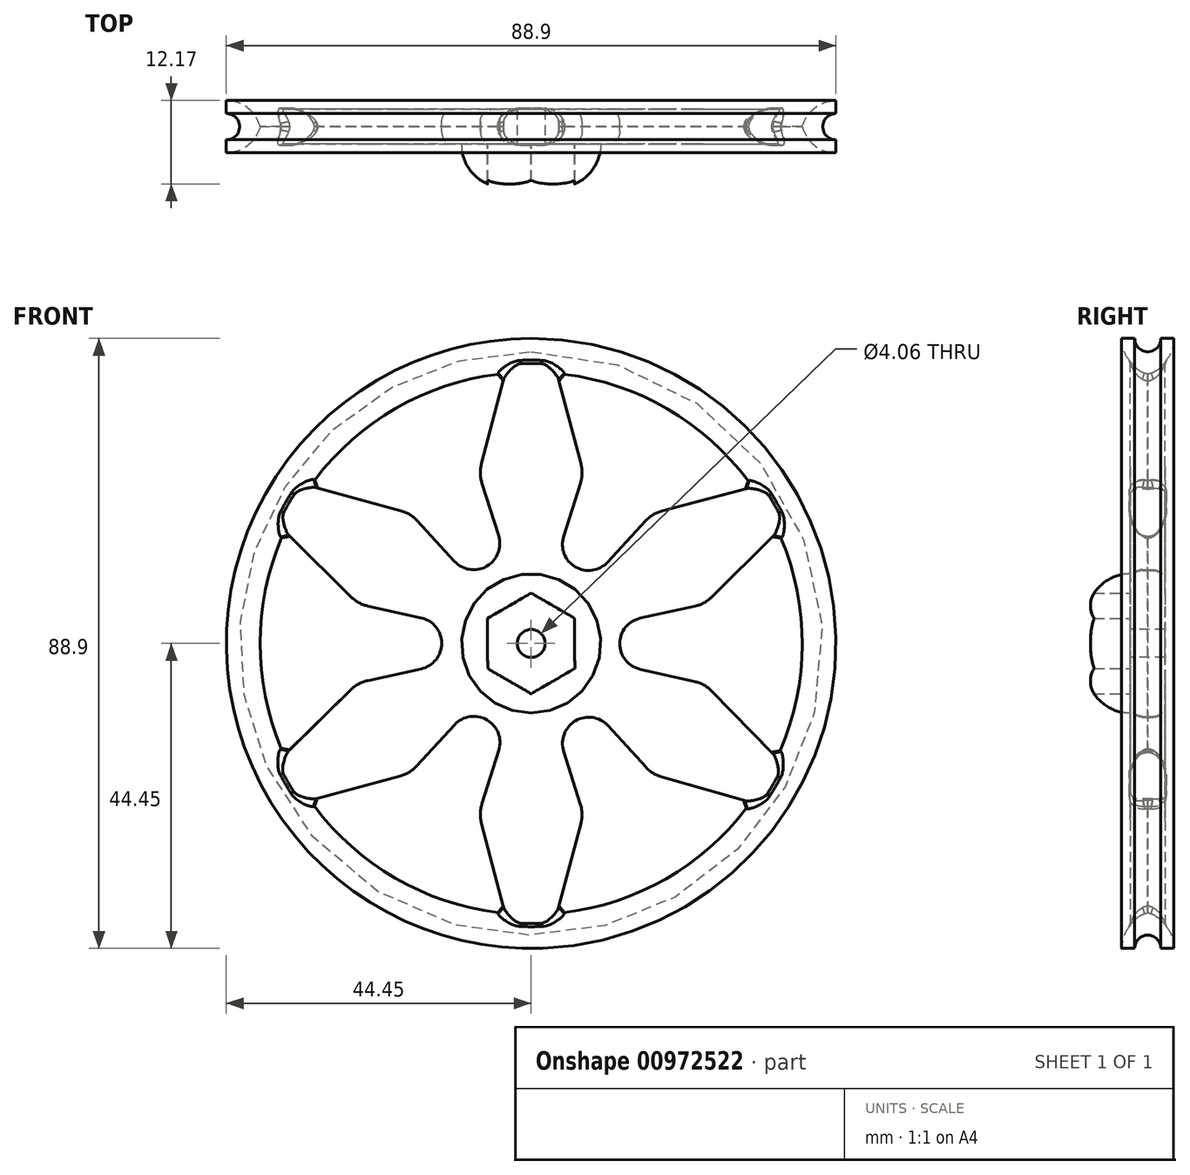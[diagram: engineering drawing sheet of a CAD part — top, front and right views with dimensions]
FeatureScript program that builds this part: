
annotation { "Feature Type Name" : "Feature", "Feature Type Description" : "" }
export const myFeature = defineFeature(function(context is Context, id is Id, definition is map)
    precondition{}
    {
        {
            var Q0;
            Q0=qCreatedBy(makeId("Top.planeOp"),FACE);
            var sketch = newSketch(context, id + "F0", { "sketchPlane" : qUnion([Q0])});
            skLineSegment(sketch, "E0", {"start": v(0, 0) * mm, "end": v(0, 3.8) * mm});
            skLineSegment(sketch, "E1", {"start": v(0, 3.8) * mm, "end": v(0, 0) * mm});
            skLineSegment(sketch, "E2", {"start": v(0, 0) * mm, "end": v(0, -3.8) * mm});
            skLineSegment(sketch, "E3", {"start": v(39.37, 3.8) * mm, "end": v(44.45, 3.8) * mm});
            skLineSegment(sketch, "E4", {"start": v(44.45, -3.8) * mm, "end": v(39.37, -3.8) * mm});
            skLineSegment(sketch, "E5", {"start": v(39.37, 3.8) * mm, "end": v(39.37, 0) * mm});
            skLineSegment(sketch, "E6", {"start": v(39.37, -3.8) * mm, "end": v(39.37, 0) * mm});
            skLineSegment(sketch, "E7", {"start": v(44.45, -1.9) * mm, "end": v(44.45, -3.8) * mm});
            skLineSegment(sketch, "E8", {"start": v(44.45, 3.8) * mm, "end": v(44.45, 1.9) * mm});
            skArc(sketch, "E9", {"start": v(44.45, 1.9) * mm, "mid": v(42.51, 0) * mm, "end": v(44.45, -1.9) * mm});
            skSolve(sketch);
        }
        {
            var Q0;
            Q0=makeQuery(id+"F0.imprint","IMPRINT",FACE,{"disambiguationData":[TD([[makeQuery(id+"F0.imprint","IMPRINT",EDGE,{"derivedFrom":sQuery(id+"F0.wireOp",EDGE,"E3")}),-1.0]])]});
            var Q1;
            Q1=sQuery(id+"F0.wireOp",EDGE,"E1");
            revolve(context, id + "F1", {"surfaceOperationType" : NewSurfaceOperationType.NEW, "entities" : qUnion([Q0]), "axis" : qUnion([Q1]), "revolveType" : RevolveType.FULL});
        }
        {
            var Q0;
            Q0=qCreatedBy(makeId("Front.planeOp"),FACE);
            var sketch = newSketch(context, id + "F2", { "sketchPlane" : qUnion([Q0])});
            skLineSegment(sketch, "E10.0", {"start": v(0, 7.33) * mm, "end": v(6.35, 3.67) * mm});
            skLineSegment(sketch, "E10.1", {"start": v(6.35, 3.67) * mm, "end": v(6.35, -3.67) * mm});
            skLineSegment(sketch, "E10.2", {"start": v(6.35, -3.67) * mm, "end": v(0, -7.33) * mm});
            skLineSegment(sketch, "E10.3", {"start": v(0, -7.33) * mm, "end": v(-6.35, -3.67) * mm});
            skLineSegment(sketch, "E10.4", {"start": v(-6.35, -3.67) * mm, "end": v(-6.35, 3.67) * mm});
            skLineSegment(sketch, "E10.5", {"start": v(-6.35, 3.67) * mm, "end": v(0, 7.33) * mm});
            skCircle(sketch, "E11", {"center": v(0, 0) * mm, "radius": 10.16 * mm});
            skCircle(sketch, "E12", {"center": v(0, 0) * mm, "radius": 39.4 * mm});
            skLineSegment(sketch, "E13", {"start": v(25.3, 5.74) * mm, "end": v(15.9, 3.68) * mm});
            skLineSegment(sketch, "E14", {"start": v(-7.62, 24.77) * mm, "end": v(-3.81, 39.22) * mm});
            skLineSegment(sketch, "E15", {"start": v(7.62, 24.77) * mm, "end": v(3.8, 39.22) * mm});
            skLineSegment(sketch, "E16", {"start": v(17.7, 18.96) * mm, "end": v(32.16, 22.77) * mm});
            skLineSegment(sketch, "E17", {"start": v(-17.57, 18.94) * mm, "end": v(-32.06, 22.91) * mm});
            skLineSegment(sketch, "E18", {"start": v(-25.19, 5.74) * mm, "end": v(-35.87, 16.31) * mm});
            skLineSegment(sketch, "E19", {"start": v(-25.29, -5.73) * mm, "end": v(-35.92, -16.2) * mm});
            skLineSegment(sketch, "E20", {"start": v(-32.13, -22.82) * mm, "end": v(-17.72, -18.96) * mm});
            skLineSegment(sketch, "E21", {"start": v(25.3, 5.74) * mm, "end": v(35.9, 16.26) * mm});
            skLineSegment(sketch, "E22", {"start": v(-17.57, 18.94) * mm, "end": v(-11.2, 11.98) * mm});
            skLineSegment(sketch, "E23", {"start": v(-7.62, 24.77) * mm, "end": v(-4.75, 15.7) * mm});
            skArc(sketch, "E24.filletArc", {"start": v(-11.2, 11.98) * mm, "mid": v(-6.48, 11.25) * mm, "end": v(-4.75, 15.7) * mm});
            skLineSegment(sketch, "E25", {"start": v(7.62, 24.77) * mm, "end": v(4.73, 15.59) * mm});
            skLineSegment(sketch, "E26", {"start": v(11.17, 11.86) * mm, "end": v(17.7, 18.96) * mm});
            skArc(sketch, "E27.filletArc", {"start": v(4.73, 15.59) * mm, "mid": v(6.46, 11.15) * mm, "end": v(11.17, 11.86) * mm});
            skLineSegment(sketch, "E28", {"start": v(17.68, -19.09) * mm, "end": v(31.9, -23.13) * mm});
            skLineSegment(sketch, "E29", {"start": v(25.3, -5.89) * mm, "end": v(35.76, -16.56) * mm});
            skLineSegment(sketch, "E30", {"start": v(25.3, -5.89) * mm, "end": v(15.88, -3.76) * mm});
            skLineSegment(sketch, "E31", {"start": v(11.2, -11.99) * mm, "end": v(17.68, -19.09) * mm});
            skLineSegment(sketch, "E32", {"start": v(7.62, -24.8) * mm, "end": v(4.75, -15.7) * mm});
            skLineSegment(sketch, "E33", {"start": v(-4.72, -15.57) * mm, "end": v(-7.62, -24.8) * mm});
            skLineSegment(sketch, "E34", {"start": v(-7.62, -24.8) * mm, "end": v(-3.81, -39.22) * mm});
            skLineSegment(sketch, "E35", {"start": v(7.62, -24.8) * mm, "end": v(3.81, -39.22) * mm});
            skLineSegment(sketch, "E36", {"start": v(-25.19, 5.74) * mm, "end": v(-16.04, 3.74) * mm});
            skLineSegment(sketch, "E37", {"start": v(-17.72, -18.96) * mm, "end": v(-11.16, -11.85) * mm});
            skLineSegment(sketch, "E38", {"start": v(-16.04, -3.7) * mm, "end": v(-25.29, -5.73) * mm});
            skArc(sketch, "E39.filletArc", {"start": v(-16.04, -3.7) * mm, "mid": v(-13.05, 0.02) * mm, "end": v(-16.04, 3.74) * mm});
            skArc(sketch, "E40.filletArc", {"start": v(-4.72, -15.57) * mm, "mid": v(-6.45, -11.14) * mm, "end": v(-11.16, -11.85) * mm});
            skArc(sketch, "E41.filletArc", {"start": v(11.2, -11.99) * mm, "mid": v(6.48, -11.26) * mm, "end": v(4.75, -15.7) * mm});
            skArc(sketch, "E42.filletArc", {"start": v(15.9, 3.68) * mm, "mid": v(12.91, -0.03) * mm, "end": v(15.88, -3.76) * mm});
            skSolve(sketch);
        }
        {
            var Q0;
            Q0=makeQuery(id+"F2.imprint","IMPRINT",FACE,{"disambiguationData":[TD([[makeQuery(id+"F2.imprint","IMPRINT",EDGE,{"derivedFrom":sQuery(id+"F2.wireOp",EDGE,"E11")}),-1.0]])]});
            var Q1;
            Q1=makeQuery(id+"F2.imprint","IMPRINT",FACE,{"disambiguationData":[TD([[makeQuery(id+"F2.imprint","IMPRINT",EDGE,{"derivedFrom":sQuery(id+"F2.wireOp",EDGE,"E10.0")}),-1.0]])]});
            extrude(context, id + "F3", {"entities" : qUnion([Q0, Q1]), "endBound" : BoundingType.SYMMETRIC, "depth" : 5.08 * mm, "offsetDistance" : 25.4 * mm});
        }
        {
            var Q0;
            Q0=qCreatedBy(makeId("Front.planeOp"),FACE);
            var sketch = newSketch(context, id + "F4", { "sketchPlane" : qUnion([Q0])});
            skCircle(sketch, "E43", {"center": v(0, 0) * mm, "radius": 10.16 * mm});
            skLineSegment(sketch, "E44.0", {"start": v(6.35, -3.66) * mm, "end": v(0, -7.33) * mm});
            skLineSegment(sketch, "E44.1", {"start": v(0, -7.33) * mm, "end": v(-6.35, -3.67) * mm});
            skLineSegment(sketch, "E44.2", {"start": v(-6.35, -3.67) * mm, "end": v(-6.35, 3.66) * mm});
            skLineSegment(sketch, "E44.3", {"start": v(-6.35, 3.66) * mm, "end": v(0, 7.33) * mm});
            skLineSegment(sketch, "E44.4", {"start": v(0, 7.33) * mm, "end": v(6.35, 3.67) * mm});
            skLineSegment(sketch, "E44.5", {"start": v(6.35, 3.67) * mm, "end": v(6.35, -3.66) * mm});
            skSolve(sketch);
        }
        {
            var Q0;
            Q0=makeQuery(id+"F4.imprint","IMPRINT",FACE,{"disambiguationData":[TD([[makeQuery(id+"F4.imprint","IMPRINT",EDGE,{"derivedFrom":sQuery(id+"F4.wireOp",EDGE,"E43")}),1.0]])]});
            extrude(context, id + "F5", {"entities" : qUnion([Q0]), "depth" : 8.9 * mm, "offsetDistance" : 25.4 * mm});
        }
        {
            var Q0;
            Q0=makeQuery(id+"F5.opExtrude","CAP_FACE",FACE,{"disambiguationData":[OSD([sQuery(id+"F4.wireOp",EDGE,"E43"),sQuery(id+"F4.wireOp",EDGE,"E44.0"),sQuery(id+"F4.wireOp",EDGE,"E44.1"),sQuery(id+"F4.wireOp",EDGE,"E44.2"),sQuery(id+"F4.wireOp",EDGE,"E44.3"),sQuery(id+"F4.wireOp",EDGE,"E44.4"),sQuery(id+"F4.wireOp",EDGE,"E44.5")])],"isStart":true});
            extrude(context, id + "F6", {"entities" : qUnion([Q0]), "depth" : 2.54 * mm, "offsetDistance" : 25.4 * mm});
        }
        {
            var Q0;
            Q0=makeQuery(id+"F1.opRevolve","SWEPT_BODY",BODY,{"disambiguationData":[OSD([sQuery(id+"F0.wireOp",EDGE,"E3"),sQuery(id+"F0.wireOp",EDGE,"E4"),sQuery(id+"F0.wireOp",EDGE,"E5"),sQuery(id+"F0.wireOp",EDGE,"E6"),sQuery(id+"F0.wireOp",EDGE,"E7"),sQuery(id+"F0.wireOp",EDGE,"E8"),sQuery(id+"F0.wireOp",EDGE,"E9")])]});
            var Q1;
            Q1=makeQuery(id+"F3.opExtrude","SWEPT_BODY",BODY,{"disambiguationData":[OSD([sQuery(id+"F2.wireOp",EDGE,"E11"),sQuery(id+"F2.wireOp",EDGE,"E12"),sQuery(id+"F2.wireOp",EDGE,"E13"),sQuery(id+"F2.wireOp",EDGE,"E14"),sQuery(id+"F2.wireOp",EDGE,"E15"),sQuery(id+"F2.wireOp",EDGE,"E16"),sQuery(id+"F2.wireOp",EDGE,"E17"),sQuery(id+"F2.wireOp",EDGE,"E18"),sQuery(id+"F2.wireOp",EDGE,"E19"),sQuery(id+"F2.wireOp",EDGE,"E20"),sQuery(id+"F2.wireOp",EDGE,"E21"),sQuery(id+"F2.wireOp",EDGE,"E22"),sQuery(id+"F2.wireOp",EDGE,"E23"),sQuery(id+"F2.wireOp",EDGE,"E24.filletArc"),sQuery(id+"F2.wireOp",EDGE,"E25"),sQuery(id+"F2.wireOp",EDGE,"E26"),sQuery(id+"F2.wireOp",EDGE,"E27.filletArc"),sQuery(id+"F2.wireOp",EDGE,"E28"),sQuery(id+"F2.wireOp",EDGE,"E29"),sQuery(id+"F2.wireOp",EDGE,"E30"),sQuery(id+"F2.wireOp",EDGE,"E31"),sQuery(id+"F2.wireOp",EDGE,"E32"),sQuery(id+"F2.wireOp",EDGE,"E33"),sQuery(id+"F2.wireOp",EDGE,"E34"),sQuery(id+"F2.wireOp",EDGE,"E35"),sQuery(id+"F2.wireOp",EDGE,"E36"),sQuery(id+"F2.wireOp",EDGE,"E37"),sQuery(id+"F2.wireOp",EDGE,"E38"),sQuery(id+"F2.wireOp",EDGE,"E39.filletArc"),sQuery(id+"F2.wireOp",EDGE,"E40.filletArc"),sQuery(id+"F2.wireOp",EDGE,"E41.filletArc"),sQuery(id+"F2.wireOp",EDGE,"E42.filletArc")])]});
            var Q2;
            Q2=makeQuery(id+"F3.opExtrude","SWEPT_BODY",BODY,{"disambiguationData":[OSD([sQuery(id+"F2.wireOp",EDGE,"E10.0"),sQuery(id+"F2.wireOp",EDGE,"E10.1"),sQuery(id+"F2.wireOp",EDGE,"E10.2"),sQuery(id+"F2.wireOp",EDGE,"E10.3"),sQuery(id+"F2.wireOp",EDGE,"E10.4"),sQuery(id+"F2.wireOp",EDGE,"E10.5")])]});
            var Q3;
            Q3=makeQuery(id+"F5.opExtrude","SWEPT_BODY",BODY,{"disambiguationData":[OSD([sQuery(id+"F4.wireOp",EDGE,"E43"),sQuery(id+"F4.wireOp",EDGE,"E44.0"),sQuery(id+"F4.wireOp",EDGE,"E44.1"),sQuery(id+"F4.wireOp",EDGE,"E44.2"),sQuery(id+"F4.wireOp",EDGE,"E44.3"),sQuery(id+"F4.wireOp",EDGE,"E44.4"),sQuery(id+"F4.wireOp",EDGE,"E44.5")])]});
            var Q4;
            Q4=makeQuery(id+"F6.opExtrude","SWEPT_BODY",BODY,{"disambiguationData":[OSD([sQuery(id+"F4.wireOp",EDGE,"E43"),sQuery(id+"F4.wireOp",EDGE,"E44.0"),sQuery(id+"F4.wireOp",EDGE,"E44.1"),sQuery(id+"F4.wireOp",EDGE,"E44.2"),sQuery(id+"F4.wireOp",EDGE,"E44.3"),sQuery(id+"F4.wireOp",EDGE,"E44.4"),sQuery(id+"F4.wireOp",EDGE,"E44.5")])]});
            booleanBodies(context, id + "F7", {"operationType" : BooleanOperationType.UNION, "tools" : qUnion([Q0, Q1, Q2, Q3, Q4])});
        }
        {
            var Q0;
            Q0=makeQuery(id+"F5.opExtrude","CAP_EDGE",EDGE,{"disambiguationData":[OSD([sQuery(id+"F4.wireOp",EDGE,"E43")])],"isStart":false});
            fillet(context, id + "F8", {"entities" : qUnion([Q0]), "radius" : 6.35 * mm, "tangentPropagation" : true, "allowEdgeOverflow" : false});
        }
        {
            var Q0;
            Q0=makeQuery(id+"F3.opExtrude","CAP_FACE",FACE,{"disambiguationData":[OSD([sQuery(id+"F2.wireOp",EDGE,"E11"),sQuery(id+"F2.wireOp",EDGE,"E12"),sQuery(id+"F2.wireOp",EDGE,"E13"),sQuery(id+"F2.wireOp",EDGE,"E14"),sQuery(id+"F2.wireOp",EDGE,"E15"),sQuery(id+"F2.wireOp",EDGE,"E16"),sQuery(id+"F2.wireOp",EDGE,"E17"),sQuery(id+"F2.wireOp",EDGE,"E18"),sQuery(id+"F2.wireOp",EDGE,"E19"),sQuery(id+"F2.wireOp",EDGE,"E20"),sQuery(id+"F2.wireOp",EDGE,"E21"),sQuery(id+"F2.wireOp",EDGE,"E22"),sQuery(id+"F2.wireOp",EDGE,"E23"),sQuery(id+"F2.wireOp",EDGE,"E24.filletArc"),sQuery(id+"F2.wireOp",EDGE,"E25"),sQuery(id+"F2.wireOp",EDGE,"E26"),sQuery(id+"F2.wireOp",EDGE,"E27.filletArc"),sQuery(id+"F2.wireOp",EDGE,"E28"),sQuery(id+"F2.wireOp",EDGE,"E29"),sQuery(id+"F2.wireOp",EDGE,"E30"),sQuery(id+"F2.wireOp",EDGE,"E31"),sQuery(id+"F2.wireOp",EDGE,"E32"),sQuery(id+"F2.wireOp",EDGE,"E33"),sQuery(id+"F2.wireOp",EDGE,"E34"),sQuery(id+"F2.wireOp",EDGE,"E35"),sQuery(id+"F2.wireOp",EDGE,"E36"),sQuery(id+"F2.wireOp",EDGE,"E37"),sQuery(id+"F2.wireOp",EDGE,"E38"),sQuery(id+"F2.wireOp",EDGE,"E39.filletArc"),sQuery(id+"F2.wireOp",EDGE,"E40.filletArc"),sQuery(id+"F2.wireOp",EDGE,"E41.filletArc"),sQuery(id+"F2.wireOp",EDGE,"E42.filletArc")])],"isStart":false});
            var sketch = newSketch(context, id + "F9", { "sketchPlane" : qUnion([Q0])});
            skPoint(sketch, "E45", {"position": v(0, 0) * mm});
            skSolve(sketch);
        }
        {
            var Q0;
            Q0=sQuery(id+"F9.wireOp",VERTEX,"E45");
            var Q1;
            Q1=makeQuery(id+"F1.opRevolve","SWEPT_BODY",BODY,{"disambiguationData":[OSD([sQuery(id+"F0.wireOp",EDGE,"E3"),sQuery(id+"F0.wireOp",EDGE,"E4"),sQuery(id+"F0.wireOp",EDGE,"E5"),sQuery(id+"F0.wireOp",EDGE,"E6"),sQuery(id+"F0.wireOp",EDGE,"E7"),sQuery(id+"F0.wireOp",EDGE,"E8"),sQuery(id+"F0.wireOp",EDGE,"E9")])]});
            hole(context, id + "F10", {"style" : HoleStyle.SIMPLE, "endStyle" : HoleEndStyle.THROUGH, "holeDiameter" : 4.06 * mm, "majorDiameter" : 6.35 * mm, "isTappedThrough" : true, "tappedDepth" : 12.7 * mm, "tapClearance" : 3, "locations" : qUnion([Q0]), "scope" : qUnion([Q1])});
        }
        {
            var Q0;
            Q0=makeQuery(id+"F3.opExtrude","SWEPT_EDGE",EDGE,{"disambiguationData":[OSD([sQuery(id+"F2.wireOp",EDGE,"E17"),sQuery(id+"F2.wireOp",EDGE,"E22")])]});
            var Q1;
            Q1=makeQuery(id+"F3.opExtrude","SWEPT_EDGE",EDGE,{"disambiguationData":[OSD([sQuery(id+"F2.wireOp",EDGE,"E18"),sQuery(id+"F2.wireOp",EDGE,"E36")])]});
            var Q2;
            Q2=makeQuery(id+"F3.opExtrude","SWEPT_EDGE",EDGE,{"disambiguationData":[OSD([sQuery(id+"F2.wireOp",EDGE,"E14"),sQuery(id+"F2.wireOp",EDGE,"E23")])]});
            var Q3;
            Q3=makeQuery(id+"F3.opExtrude","SWEPT_EDGE",EDGE,{"disambiguationData":[OSD([sQuery(id+"F2.wireOp",EDGE,"E15"),sQuery(id+"F2.wireOp",EDGE,"E25")])]});
            var Q4;
            Q4=makeQuery(id+"F3.opExtrude","SWEPT_EDGE",EDGE,{"disambiguationData":[OSD([sQuery(id+"F2.wireOp",EDGE,"E13"),sQuery(id+"F2.wireOp",EDGE,"E21")])]});
            var Q5;
            Q5=makeQuery(id+"F3.opExtrude","SWEPT_EDGE",EDGE,{"disambiguationData":[OSD([sQuery(id+"F2.wireOp",EDGE,"E16"),sQuery(id+"F2.wireOp",EDGE,"E26")])]});
            var Q6;
            Q6=makeQuery(id+"F3.opExtrude","SWEPT_EDGE",EDGE,{"disambiguationData":[OSD([sQuery(id+"F2.wireOp",EDGE,"E29"),sQuery(id+"F2.wireOp",EDGE,"E30")])]});
            var Q7;
            Q7=makeQuery(id+"F3.opExtrude","SWEPT_EDGE",EDGE,{"disambiguationData":[OSD([sQuery(id+"F2.wireOp",EDGE,"E28"),sQuery(id+"F2.wireOp",EDGE,"E31")])]});
            var Q8;
            Q8=makeQuery(id+"F3.opExtrude","SWEPT_EDGE",EDGE,{"disambiguationData":[OSD([sQuery(id+"F2.wireOp",EDGE,"E32"),sQuery(id+"F2.wireOp",EDGE,"E35")])]});
            var Q9;
            Q9=makeQuery(id+"F3.opExtrude","SWEPT_EDGE",EDGE,{"disambiguationData":[OSD([sQuery(id+"F2.wireOp",EDGE,"E19"),sQuery(id+"F2.wireOp",EDGE,"E38")])]});
            var Q10;
            Q10=makeQuery(id+"F3.opExtrude","SWEPT_EDGE",EDGE,{"disambiguationData":[OSD([sQuery(id+"F2.wireOp",EDGE,"E20"),sQuery(id+"F2.wireOp",EDGE,"E37")])]});
            var Q11;
            Q11=makeQuery(id+"F3.opExtrude","SWEPT_EDGE",EDGE,{"disambiguationData":[OSD([sQuery(id+"F2.wireOp",EDGE,"E33"),sQuery(id+"F2.wireOp",EDGE,"E34")])]});
            fillet(context, id + "F11", {"entities" : qUnion([Q0, Q1, Q2, Q3, Q4, Q5, Q6, Q7, Q8, Q9, Q10, Q11]), "radius" : 5.08 * mm, "tangentPropagation" : true, "allowEdgeOverflow" : false});
        }
        {
            var Q0;
            Q0=makeQuery(id+"F3.opExtrude","CAP_EDGE",EDGE,{"disambiguationData":[OSD([sQuery(id+"F2.wireOp",EDGE,"E17")])],"isStart":false});
            var Q1;
            Q1=makeQuery(id+"F3.opExtrude","CAP_EDGE",EDGE,{"disambiguationData":[OSD([sQuery(id+"F2.wireOp",EDGE,"E18")])],"isStart":false});
            var Q2;
            Q2=makeQuery(id+"F3.opExtrude","CAP_EDGE",EDGE,{"disambiguationData":[OSD([sQuery(id+"F2.wireOp",EDGE,"E37")])],"isStart":false});
            var Q3;
            Q3=makeQuery(id+"F3.opExtrude","CAP_EDGE",EDGE,{"disambiguationData":[OSD([sQuery(id+"F2.wireOp",EDGE,"E34")])],"isStart":false});
            var Q4;
            Q4=makeQuery(id+"F3.opExtrude","CAP_EDGE",EDGE,{"disambiguationData":[OSD([sQuery(id+"F2.wireOp",EDGE,"E35")])],"isStart":false});
            var Q5;
            Q5=makeQuery(id+"F3.opExtrude","CAP_EDGE",EDGE,{"disambiguationData":[OSD([sQuery(id+"F2.wireOp",EDGE,"E21")])],"isStart":false});
            var Q6;
            Q6=makeQuery(id+"F3.opExtrude","CAP_EDGE",EDGE,{"disambiguationData":[OSD([sQuery(id+"F2.wireOp",EDGE,"E15")])],"isStart":false});
            var Q7;
            {var subQ0=sQuery(id+"F2.wireOp",EDGE,"E14");Q7=makeQuery(id+"Fk14XMOrtsRoLGN_1.opChamfer","BLEND_EDGE",EDGE,{"blendedFrom":[makeQuery(id+"F7.opBoolean","INTERSECT",EDGE,{"derivedFrom":[makeQuery(id+"F1.opRevolve","SWEPT_FACE",FACE,{"disambiguationData":[OSD([sQuery(id+"F0.wireOp",EDGE,"E5"),sQuery(id+"F0.wireOp",EDGE,"E6")])]}),makeQuery(id+"F3.opExtrude","SWEPT_FACE",FACE,{"disambiguationData":[OSD([subQ0])]})]}),makeQuery(id+"F3.opExtrude","CAP_FACE",FACE,{"disambiguationData":[OSD([sQuery(id+"F2.wireOp",EDGE,"E11"),sQuery(id+"F2.wireOp",EDGE,"E12"),sQuery(id+"F2.wireOp",EDGE,"E13"),subQ0,sQuery(id+"F2.wireOp",EDGE,"E15"),sQuery(id+"F2.wireOp",EDGE,"E16"),sQuery(id+"F2.wireOp",EDGE,"E17"),sQuery(id+"F2.wireOp",EDGE,"E18"),sQuery(id+"F2.wireOp",EDGE,"E19"),sQuery(id+"F2.wireOp",EDGE,"E20"),sQuery(id+"F2.wireOp",EDGE,"E21"),sQuery(id+"F2.wireOp",EDGE,"E22"),sQuery(id+"F2.wireOp",EDGE,"E23"),sQuery(id+"F2.wireOp",EDGE,"E24.filletArc"),sQuery(id+"F2.wireOp",EDGE,"E25"),sQuery(id+"F2.wireOp",EDGE,"E26"),sQuery(id+"F2.wireOp",EDGE,"E27.filletArc"),sQuery(id+"F2.wireOp",EDGE,"E28"),sQuery(id+"F2.wireOp",EDGE,"E29"),sQuery(id+"F2.wireOp",EDGE,"E30"),sQuery(id+"F2.wireOp",EDGE,"E31"),sQuery(id+"F2.wireOp",EDGE,"E32"),sQuery(id+"F2.wireOp",EDGE,"E33"),sQuery(id+"F2.wireOp",EDGE,"E34"),sQuery(id+"F2.wireOp",EDGE,"E35"),sQuery(id+"F2.wireOp",EDGE,"E36"),sQuery(id+"F2.wireOp",EDGE,"E37"),sQuery(id+"F2.wireOp",EDGE,"E38"),sQuery(id+"F2.wireOp",EDGE,"E39.filletArc"),sQuery(id+"F2.wireOp",EDGE,"E40.filletArc"),sQuery(id+"F2.wireOp",EDGE,"E41.filletArc"),sQuery(id+"F2.wireOp",EDGE,"E42.filletArc")])],"isStart":false})],"blendedInto":[makeQuery(id+"F3.opExtrude","CAP_FACE",FACE,{"disambiguationData":[OSD([sQuery(id+"F2.wireOp",EDGE,"E11"),sQuery(id+"F2.wireOp",EDGE,"E12"),sQuery(id+"F2.wireOp",EDGE,"E13"),subQ0,sQuery(id+"F2.wireOp",EDGE,"E15"),sQuery(id+"F2.wireOp",EDGE,"E16"),sQuery(id+"F2.wireOp",EDGE,"E17"),sQuery(id+"F2.wireOp",EDGE,"E18"),sQuery(id+"F2.wireOp",EDGE,"E19"),sQuery(id+"F2.wireOp",EDGE,"E20"),sQuery(id+"F2.wireOp",EDGE,"E21"),sQuery(id+"F2.wireOp",EDGE,"E22"),sQuery(id+"F2.wireOp",EDGE,"E23"),sQuery(id+"F2.wireOp",EDGE,"E24.filletArc"),sQuery(id+"F2.wireOp",EDGE,"E25"),sQuery(id+"F2.wireOp",EDGE,"E26"),sQuery(id+"F2.wireOp",EDGE,"E27.filletArc"),sQuery(id+"F2.wireOp",EDGE,"E28"),sQuery(id+"F2.wireOp",EDGE,"E29"),sQuery(id+"F2.wireOp",EDGE,"E30"),sQuery(id+"F2.wireOp",EDGE,"E31"),sQuery(id+"F2.wireOp",EDGE,"E32"),sQuery(id+"F2.wireOp",EDGE,"E33"),sQuery(id+"F2.wireOp",EDGE,"E34"),sQuery(id+"F2.wireOp",EDGE,"E35"),sQuery(id+"F2.wireOp",EDGE,"E36"),sQuery(id+"F2.wireOp",EDGE,"E37"),sQuery(id+"F2.wireOp",EDGE,"E38"),sQuery(id+"F2.wireOp",EDGE,"E39.filletArc"),sQuery(id+"F2.wireOp",EDGE,"E40.filletArc"),sQuery(id+"F2.wireOp",EDGE,"E41.filletArc"),sQuery(id+"F2.wireOp",EDGE,"E42.filletArc")])],"isStart":false})]});}
            var Q8;
            {var subQ0=sQuery(id+"F2.wireOp",EDGE,"E15");Q8=makeQuery(id+"Fk14XMOrtsRoLGN_1.opChamfer","BLEND_EDGE",EDGE,{"blendedFrom":[makeQuery(id+"F7.opBoolean","INTERSECT",EDGE,{"derivedFrom":[makeQuery(id+"F1.opRevolve","SWEPT_FACE",FACE,{"disambiguationData":[OSD([sQuery(id+"F0.wireOp",EDGE,"E5"),sQuery(id+"F0.wireOp",EDGE,"E6")])]}),makeQuery(id+"F3.opExtrude","SWEPT_FACE",FACE,{"disambiguationData":[OSD([subQ0])]})]}),makeQuery(id+"F3.opExtrude","CAP_FACE",FACE,{"disambiguationData":[OSD([sQuery(id+"F2.wireOp",EDGE,"E11"),sQuery(id+"F2.wireOp",EDGE,"E12"),sQuery(id+"F2.wireOp",EDGE,"E13"),sQuery(id+"F2.wireOp",EDGE,"E14"),subQ0,sQuery(id+"F2.wireOp",EDGE,"E16"),sQuery(id+"F2.wireOp",EDGE,"E17"),sQuery(id+"F2.wireOp",EDGE,"E18"),sQuery(id+"F2.wireOp",EDGE,"E19"),sQuery(id+"F2.wireOp",EDGE,"E20"),sQuery(id+"F2.wireOp",EDGE,"E21"),sQuery(id+"F2.wireOp",EDGE,"E22"),sQuery(id+"F2.wireOp",EDGE,"E23"),sQuery(id+"F2.wireOp",EDGE,"E24.filletArc"),sQuery(id+"F2.wireOp",EDGE,"E25"),sQuery(id+"F2.wireOp",EDGE,"E26"),sQuery(id+"F2.wireOp",EDGE,"E27.filletArc"),sQuery(id+"F2.wireOp",EDGE,"E28"),sQuery(id+"F2.wireOp",EDGE,"E29"),sQuery(id+"F2.wireOp",EDGE,"E30"),sQuery(id+"F2.wireOp",EDGE,"E31"),sQuery(id+"F2.wireOp",EDGE,"E32"),sQuery(id+"F2.wireOp",EDGE,"E33"),sQuery(id+"F2.wireOp",EDGE,"E34"),sQuery(id+"F2.wireOp",EDGE,"E35"),sQuery(id+"F2.wireOp",EDGE,"E36"),sQuery(id+"F2.wireOp",EDGE,"E37"),sQuery(id+"F2.wireOp",EDGE,"E38"),sQuery(id+"F2.wireOp",EDGE,"E39.filletArc"),sQuery(id+"F2.wireOp",EDGE,"E40.filletArc"),sQuery(id+"F2.wireOp",EDGE,"E41.filletArc"),sQuery(id+"F2.wireOp",EDGE,"E42.filletArc")])],"isStart":false})],"blendedInto":[makeQuery(id+"F3.opExtrude","CAP_FACE",FACE,{"disambiguationData":[OSD([sQuery(id+"F2.wireOp",EDGE,"E11"),sQuery(id+"F2.wireOp",EDGE,"E12"),sQuery(id+"F2.wireOp",EDGE,"E13"),sQuery(id+"F2.wireOp",EDGE,"E14"),subQ0,sQuery(id+"F2.wireOp",EDGE,"E16"),sQuery(id+"F2.wireOp",EDGE,"E17"),sQuery(id+"F2.wireOp",EDGE,"E18"),sQuery(id+"F2.wireOp",EDGE,"E19"),sQuery(id+"F2.wireOp",EDGE,"E20"),sQuery(id+"F2.wireOp",EDGE,"E21"),sQuery(id+"F2.wireOp",EDGE,"E22"),sQuery(id+"F2.wireOp",EDGE,"E23"),sQuery(id+"F2.wireOp",EDGE,"E24.filletArc"),sQuery(id+"F2.wireOp",EDGE,"E25"),sQuery(id+"F2.wireOp",EDGE,"E26"),sQuery(id+"F2.wireOp",EDGE,"E27.filletArc"),sQuery(id+"F2.wireOp",EDGE,"E28"),sQuery(id+"F2.wireOp",EDGE,"E29"),sQuery(id+"F2.wireOp",EDGE,"E30"),sQuery(id+"F2.wireOp",EDGE,"E31"),sQuery(id+"F2.wireOp",EDGE,"E32"),sQuery(id+"F2.wireOp",EDGE,"E33"),sQuery(id+"F2.wireOp",EDGE,"E34"),sQuery(id+"F2.wireOp",EDGE,"E35"),sQuery(id+"F2.wireOp",EDGE,"E36"),sQuery(id+"F2.wireOp",EDGE,"E37"),sQuery(id+"F2.wireOp",EDGE,"E38"),sQuery(id+"F2.wireOp",EDGE,"E39.filletArc"),sQuery(id+"F2.wireOp",EDGE,"E40.filletArc"),sQuery(id+"F2.wireOp",EDGE,"E41.filletArc"),sQuery(id+"F2.wireOp",EDGE,"E42.filletArc")])],"isStart":false})]});}
            var Q9;
            {var subQ0=sQuery(id+"F2.wireOp",EDGE,"E21");Q9=makeQuery(id+"Fk14XMOrtsRoLGN_1.opChamfer","BLEND_EDGE",EDGE,{"blendedFrom":[makeQuery(id+"F7.opBoolean","INTERSECT",EDGE,{"derivedFrom":[makeQuery(id+"F1.opRevolve","SWEPT_FACE",FACE,{"disambiguationData":[OSD([sQuery(id+"F0.wireOp",EDGE,"E5"),sQuery(id+"F0.wireOp",EDGE,"E6")])]}),makeQuery(id+"F3.opExtrude","SWEPT_FACE",FACE,{"disambiguationData":[OSD([subQ0])]})]}),makeQuery(id+"F3.opExtrude","CAP_FACE",FACE,{"disambiguationData":[OSD([sQuery(id+"F2.wireOp",EDGE,"E11"),sQuery(id+"F2.wireOp",EDGE,"E12"),sQuery(id+"F2.wireOp",EDGE,"E13"),sQuery(id+"F2.wireOp",EDGE,"E14"),sQuery(id+"F2.wireOp",EDGE,"E15"),sQuery(id+"F2.wireOp",EDGE,"E16"),sQuery(id+"F2.wireOp",EDGE,"E17"),sQuery(id+"F2.wireOp",EDGE,"E18"),sQuery(id+"F2.wireOp",EDGE,"E19"),sQuery(id+"F2.wireOp",EDGE,"E20"),subQ0,sQuery(id+"F2.wireOp",EDGE,"E22"),sQuery(id+"F2.wireOp",EDGE,"E23"),sQuery(id+"F2.wireOp",EDGE,"E24.filletArc"),sQuery(id+"F2.wireOp",EDGE,"E25"),sQuery(id+"F2.wireOp",EDGE,"E26"),sQuery(id+"F2.wireOp",EDGE,"E27.filletArc"),sQuery(id+"F2.wireOp",EDGE,"E28"),sQuery(id+"F2.wireOp",EDGE,"E29"),sQuery(id+"F2.wireOp",EDGE,"E30"),sQuery(id+"F2.wireOp",EDGE,"E31"),sQuery(id+"F2.wireOp",EDGE,"E32"),sQuery(id+"F2.wireOp",EDGE,"E33"),sQuery(id+"F2.wireOp",EDGE,"E34"),sQuery(id+"F2.wireOp",EDGE,"E35"),sQuery(id+"F2.wireOp",EDGE,"E36"),sQuery(id+"F2.wireOp",EDGE,"E37"),sQuery(id+"F2.wireOp",EDGE,"E38"),sQuery(id+"F2.wireOp",EDGE,"E39.filletArc"),sQuery(id+"F2.wireOp",EDGE,"E40.filletArc"),sQuery(id+"F2.wireOp",EDGE,"E41.filletArc"),sQuery(id+"F2.wireOp",EDGE,"E42.filletArc")])],"isStart":false})],"blendedInto":[makeQuery(id+"F3.opExtrude","CAP_FACE",FACE,{"disambiguationData":[OSD([sQuery(id+"F2.wireOp",EDGE,"E11"),sQuery(id+"F2.wireOp",EDGE,"E12"),sQuery(id+"F2.wireOp",EDGE,"E13"),sQuery(id+"F2.wireOp",EDGE,"E14"),sQuery(id+"F2.wireOp",EDGE,"E15"),sQuery(id+"F2.wireOp",EDGE,"E16"),sQuery(id+"F2.wireOp",EDGE,"E17"),sQuery(id+"F2.wireOp",EDGE,"E18"),sQuery(id+"F2.wireOp",EDGE,"E19"),sQuery(id+"F2.wireOp",EDGE,"E20"),subQ0,sQuery(id+"F2.wireOp",EDGE,"E22"),sQuery(id+"F2.wireOp",EDGE,"E23"),sQuery(id+"F2.wireOp",EDGE,"E24.filletArc"),sQuery(id+"F2.wireOp",EDGE,"E25"),sQuery(id+"F2.wireOp",EDGE,"E26"),sQuery(id+"F2.wireOp",EDGE,"E27.filletArc"),sQuery(id+"F2.wireOp",EDGE,"E28"),sQuery(id+"F2.wireOp",EDGE,"E29"),sQuery(id+"F2.wireOp",EDGE,"E30"),sQuery(id+"F2.wireOp",EDGE,"E31"),sQuery(id+"F2.wireOp",EDGE,"E32"),sQuery(id+"F2.wireOp",EDGE,"E33"),sQuery(id+"F2.wireOp",EDGE,"E34"),sQuery(id+"F2.wireOp",EDGE,"E35"),sQuery(id+"F2.wireOp",EDGE,"E36"),sQuery(id+"F2.wireOp",EDGE,"E37"),sQuery(id+"F2.wireOp",EDGE,"E38"),sQuery(id+"F2.wireOp",EDGE,"E39.filletArc"),sQuery(id+"F2.wireOp",EDGE,"E40.filletArc"),sQuery(id+"F2.wireOp",EDGE,"E41.filletArc"),sQuery(id+"F2.wireOp",EDGE,"E42.filletArc")])],"isStart":false})]});}
            var Q10;
            {var subQ0=sQuery(id+"F2.wireOp",EDGE,"E16");Q10=makeQuery(id+"Fk14XMOrtsRoLGN_1.opChamfer","BLEND_EDGE",EDGE,{"blendedFrom":[makeQuery(id+"F7.opBoolean","INTERSECT",EDGE,{"derivedFrom":[makeQuery(id+"F1.opRevolve","SWEPT_FACE",FACE,{"disambiguationData":[OSD([sQuery(id+"F0.wireOp",EDGE,"E5"),sQuery(id+"F0.wireOp",EDGE,"E6")])]}),makeQuery(id+"F3.opExtrude","SWEPT_FACE",FACE,{"disambiguationData":[OSD([subQ0])]})]}),makeQuery(id+"F3.opExtrude","CAP_FACE",FACE,{"disambiguationData":[OSD([sQuery(id+"F2.wireOp",EDGE,"E11"),sQuery(id+"F2.wireOp",EDGE,"E12"),sQuery(id+"F2.wireOp",EDGE,"E13"),sQuery(id+"F2.wireOp",EDGE,"E14"),sQuery(id+"F2.wireOp",EDGE,"E15"),subQ0,sQuery(id+"F2.wireOp",EDGE,"E17"),sQuery(id+"F2.wireOp",EDGE,"E18"),sQuery(id+"F2.wireOp",EDGE,"E19"),sQuery(id+"F2.wireOp",EDGE,"E20"),sQuery(id+"F2.wireOp",EDGE,"E21"),sQuery(id+"F2.wireOp",EDGE,"E22"),sQuery(id+"F2.wireOp",EDGE,"E23"),sQuery(id+"F2.wireOp",EDGE,"E24.filletArc"),sQuery(id+"F2.wireOp",EDGE,"E25"),sQuery(id+"F2.wireOp",EDGE,"E26"),sQuery(id+"F2.wireOp",EDGE,"E27.filletArc"),sQuery(id+"F2.wireOp",EDGE,"E28"),sQuery(id+"F2.wireOp",EDGE,"E29"),sQuery(id+"F2.wireOp",EDGE,"E30"),sQuery(id+"F2.wireOp",EDGE,"E31"),sQuery(id+"F2.wireOp",EDGE,"E32"),sQuery(id+"F2.wireOp",EDGE,"E33"),sQuery(id+"F2.wireOp",EDGE,"E34"),sQuery(id+"F2.wireOp",EDGE,"E35"),sQuery(id+"F2.wireOp",EDGE,"E36"),sQuery(id+"F2.wireOp",EDGE,"E37"),sQuery(id+"F2.wireOp",EDGE,"E38"),sQuery(id+"F2.wireOp",EDGE,"E39.filletArc"),sQuery(id+"F2.wireOp",EDGE,"E40.filletArc"),sQuery(id+"F2.wireOp",EDGE,"E41.filletArc"),sQuery(id+"F2.wireOp",EDGE,"E42.filletArc")])],"isStart":false})],"blendedInto":[makeQuery(id+"F3.opExtrude","CAP_FACE",FACE,{"disambiguationData":[OSD([sQuery(id+"F2.wireOp",EDGE,"E11"),sQuery(id+"F2.wireOp",EDGE,"E12"),sQuery(id+"F2.wireOp",EDGE,"E13"),sQuery(id+"F2.wireOp",EDGE,"E14"),sQuery(id+"F2.wireOp",EDGE,"E15"),subQ0,sQuery(id+"F2.wireOp",EDGE,"E17"),sQuery(id+"F2.wireOp",EDGE,"E18"),sQuery(id+"F2.wireOp",EDGE,"E19"),sQuery(id+"F2.wireOp",EDGE,"E20"),sQuery(id+"F2.wireOp",EDGE,"E21"),sQuery(id+"F2.wireOp",EDGE,"E22"),sQuery(id+"F2.wireOp",EDGE,"E23"),sQuery(id+"F2.wireOp",EDGE,"E24.filletArc"),sQuery(id+"F2.wireOp",EDGE,"E25"),sQuery(id+"F2.wireOp",EDGE,"E26"),sQuery(id+"F2.wireOp",EDGE,"E27.filletArc"),sQuery(id+"F2.wireOp",EDGE,"E28"),sQuery(id+"F2.wireOp",EDGE,"E29"),sQuery(id+"F2.wireOp",EDGE,"E30"),sQuery(id+"F2.wireOp",EDGE,"E31"),sQuery(id+"F2.wireOp",EDGE,"E32"),sQuery(id+"F2.wireOp",EDGE,"E33"),sQuery(id+"F2.wireOp",EDGE,"E34"),sQuery(id+"F2.wireOp",EDGE,"E35"),sQuery(id+"F2.wireOp",EDGE,"E36"),sQuery(id+"F2.wireOp",EDGE,"E37"),sQuery(id+"F2.wireOp",EDGE,"E38"),sQuery(id+"F2.wireOp",EDGE,"E39.filletArc"),sQuery(id+"F2.wireOp",EDGE,"E40.filletArc"),sQuery(id+"F2.wireOp",EDGE,"E41.filletArc"),sQuery(id+"F2.wireOp",EDGE,"E42.filletArc")])],"isStart":false})]});}
            var Q11;
            {var subQ0=sQuery(id+"F2.wireOp",EDGE,"E29");Q11=makeQuery(id+"Fk14XMOrtsRoLGN_1.opChamfer","BLEND_EDGE",EDGE,{"blendedFrom":[makeQuery(id+"F7.opBoolean","INTERSECT",EDGE,{"derivedFrom":[makeQuery(id+"F1.opRevolve","SWEPT_FACE",FACE,{"disambiguationData":[OSD([sQuery(id+"F0.wireOp",EDGE,"E5"),sQuery(id+"F0.wireOp",EDGE,"E6")])]}),makeQuery(id+"F3.opExtrude","SWEPT_FACE",FACE,{"disambiguationData":[OSD([subQ0])]})]}),makeQuery(id+"F3.opExtrude","CAP_FACE",FACE,{"disambiguationData":[OSD([sQuery(id+"F2.wireOp",EDGE,"E11"),sQuery(id+"F2.wireOp",EDGE,"E12"),sQuery(id+"F2.wireOp",EDGE,"E13"),sQuery(id+"F2.wireOp",EDGE,"E14"),sQuery(id+"F2.wireOp",EDGE,"E15"),sQuery(id+"F2.wireOp",EDGE,"E16"),sQuery(id+"F2.wireOp",EDGE,"E17"),sQuery(id+"F2.wireOp",EDGE,"E18"),sQuery(id+"F2.wireOp",EDGE,"E19"),sQuery(id+"F2.wireOp",EDGE,"E20"),sQuery(id+"F2.wireOp",EDGE,"E21"),sQuery(id+"F2.wireOp",EDGE,"E22"),sQuery(id+"F2.wireOp",EDGE,"E23"),sQuery(id+"F2.wireOp",EDGE,"E24.filletArc"),sQuery(id+"F2.wireOp",EDGE,"E25"),sQuery(id+"F2.wireOp",EDGE,"E26"),sQuery(id+"F2.wireOp",EDGE,"E27.filletArc"),sQuery(id+"F2.wireOp",EDGE,"E28"),subQ0,sQuery(id+"F2.wireOp",EDGE,"E30"),sQuery(id+"F2.wireOp",EDGE,"E31"),sQuery(id+"F2.wireOp",EDGE,"E32"),sQuery(id+"F2.wireOp",EDGE,"E33"),sQuery(id+"F2.wireOp",EDGE,"E34"),sQuery(id+"F2.wireOp",EDGE,"E35"),sQuery(id+"F2.wireOp",EDGE,"E36"),sQuery(id+"F2.wireOp",EDGE,"E37"),sQuery(id+"F2.wireOp",EDGE,"E38"),sQuery(id+"F2.wireOp",EDGE,"E39.filletArc"),sQuery(id+"F2.wireOp",EDGE,"E40.filletArc"),sQuery(id+"F2.wireOp",EDGE,"E41.filletArc"),sQuery(id+"F2.wireOp",EDGE,"E42.filletArc")])],"isStart":false})],"blendedInto":[makeQuery(id+"F3.opExtrude","CAP_FACE",FACE,{"disambiguationData":[OSD([sQuery(id+"F2.wireOp",EDGE,"E11"),sQuery(id+"F2.wireOp",EDGE,"E12"),sQuery(id+"F2.wireOp",EDGE,"E13"),sQuery(id+"F2.wireOp",EDGE,"E14"),sQuery(id+"F2.wireOp",EDGE,"E15"),sQuery(id+"F2.wireOp",EDGE,"E16"),sQuery(id+"F2.wireOp",EDGE,"E17"),sQuery(id+"F2.wireOp",EDGE,"E18"),sQuery(id+"F2.wireOp",EDGE,"E19"),sQuery(id+"F2.wireOp",EDGE,"E20"),sQuery(id+"F2.wireOp",EDGE,"E21"),sQuery(id+"F2.wireOp",EDGE,"E22"),sQuery(id+"F2.wireOp",EDGE,"E23"),sQuery(id+"F2.wireOp",EDGE,"E24.filletArc"),sQuery(id+"F2.wireOp",EDGE,"E25"),sQuery(id+"F2.wireOp",EDGE,"E26"),sQuery(id+"F2.wireOp",EDGE,"E27.filletArc"),sQuery(id+"F2.wireOp",EDGE,"E28"),subQ0,sQuery(id+"F2.wireOp",EDGE,"E30"),sQuery(id+"F2.wireOp",EDGE,"E31"),sQuery(id+"F2.wireOp",EDGE,"E32"),sQuery(id+"F2.wireOp",EDGE,"E33"),sQuery(id+"F2.wireOp",EDGE,"E34"),sQuery(id+"F2.wireOp",EDGE,"E35"),sQuery(id+"F2.wireOp",EDGE,"E36"),sQuery(id+"F2.wireOp",EDGE,"E37"),sQuery(id+"F2.wireOp",EDGE,"E38"),sQuery(id+"F2.wireOp",EDGE,"E39.filletArc"),sQuery(id+"F2.wireOp",EDGE,"E40.filletArc"),sQuery(id+"F2.wireOp",EDGE,"E41.filletArc"),sQuery(id+"F2.wireOp",EDGE,"E42.filletArc")])],"isStart":false})]});}
            var Q12;
            {var subQ0=sQuery(id+"F2.wireOp",EDGE,"E28");Q12=makeQuery(id+"Fk14XMOrtsRoLGN_1.opChamfer","BLEND_EDGE",EDGE,{"blendedFrom":[makeQuery(id+"F7.opBoolean","INTERSECT",EDGE,{"derivedFrom":[makeQuery(id+"F1.opRevolve","SWEPT_FACE",FACE,{"disambiguationData":[OSD([sQuery(id+"F0.wireOp",EDGE,"E5"),sQuery(id+"F0.wireOp",EDGE,"E6")])]}),makeQuery(id+"F3.opExtrude","SWEPT_FACE",FACE,{"disambiguationData":[OSD([subQ0])]})]}),makeQuery(id+"F3.opExtrude","CAP_FACE",FACE,{"disambiguationData":[OSD([sQuery(id+"F2.wireOp",EDGE,"E11"),sQuery(id+"F2.wireOp",EDGE,"E12"),sQuery(id+"F2.wireOp",EDGE,"E13"),sQuery(id+"F2.wireOp",EDGE,"E14"),sQuery(id+"F2.wireOp",EDGE,"E15"),sQuery(id+"F2.wireOp",EDGE,"E16"),sQuery(id+"F2.wireOp",EDGE,"E17"),sQuery(id+"F2.wireOp",EDGE,"E18"),sQuery(id+"F2.wireOp",EDGE,"E19"),sQuery(id+"F2.wireOp",EDGE,"E20"),sQuery(id+"F2.wireOp",EDGE,"E21"),sQuery(id+"F2.wireOp",EDGE,"E22"),sQuery(id+"F2.wireOp",EDGE,"E23"),sQuery(id+"F2.wireOp",EDGE,"E24.filletArc"),sQuery(id+"F2.wireOp",EDGE,"E25"),sQuery(id+"F2.wireOp",EDGE,"E26"),sQuery(id+"F2.wireOp",EDGE,"E27.filletArc"),subQ0,sQuery(id+"F2.wireOp",EDGE,"E29"),sQuery(id+"F2.wireOp",EDGE,"E30"),sQuery(id+"F2.wireOp",EDGE,"E31"),sQuery(id+"F2.wireOp",EDGE,"E32"),sQuery(id+"F2.wireOp",EDGE,"E33"),sQuery(id+"F2.wireOp",EDGE,"E34"),sQuery(id+"F2.wireOp",EDGE,"E35"),sQuery(id+"F2.wireOp",EDGE,"E36"),sQuery(id+"F2.wireOp",EDGE,"E37"),sQuery(id+"F2.wireOp",EDGE,"E38"),sQuery(id+"F2.wireOp",EDGE,"E39.filletArc"),sQuery(id+"F2.wireOp",EDGE,"E40.filletArc"),sQuery(id+"F2.wireOp",EDGE,"E41.filletArc"),sQuery(id+"F2.wireOp",EDGE,"E42.filletArc")])],"isStart":false})],"blendedInto":[makeQuery(id+"F3.opExtrude","CAP_FACE",FACE,{"disambiguationData":[OSD([sQuery(id+"F2.wireOp",EDGE,"E11"),sQuery(id+"F2.wireOp",EDGE,"E12"),sQuery(id+"F2.wireOp",EDGE,"E13"),sQuery(id+"F2.wireOp",EDGE,"E14"),sQuery(id+"F2.wireOp",EDGE,"E15"),sQuery(id+"F2.wireOp",EDGE,"E16"),sQuery(id+"F2.wireOp",EDGE,"E17"),sQuery(id+"F2.wireOp",EDGE,"E18"),sQuery(id+"F2.wireOp",EDGE,"E19"),sQuery(id+"F2.wireOp",EDGE,"E20"),sQuery(id+"F2.wireOp",EDGE,"E21"),sQuery(id+"F2.wireOp",EDGE,"E22"),sQuery(id+"F2.wireOp",EDGE,"E23"),sQuery(id+"F2.wireOp",EDGE,"E24.filletArc"),sQuery(id+"F2.wireOp",EDGE,"E25"),sQuery(id+"F2.wireOp",EDGE,"E26"),sQuery(id+"F2.wireOp",EDGE,"E27.filletArc"),subQ0,sQuery(id+"F2.wireOp",EDGE,"E29"),sQuery(id+"F2.wireOp",EDGE,"E30"),sQuery(id+"F2.wireOp",EDGE,"E31"),sQuery(id+"F2.wireOp",EDGE,"E32"),sQuery(id+"F2.wireOp",EDGE,"E33"),sQuery(id+"F2.wireOp",EDGE,"E34"),sQuery(id+"F2.wireOp",EDGE,"E35"),sQuery(id+"F2.wireOp",EDGE,"E36"),sQuery(id+"F2.wireOp",EDGE,"E37"),sQuery(id+"F2.wireOp",EDGE,"E38"),sQuery(id+"F2.wireOp",EDGE,"E39.filletArc"),sQuery(id+"F2.wireOp",EDGE,"E40.filletArc"),sQuery(id+"F2.wireOp",EDGE,"E41.filletArc"),sQuery(id+"F2.wireOp",EDGE,"E42.filletArc")])],"isStart":false})]});}
            var Q13;
            {var subQ0=sQuery(id+"F2.wireOp",EDGE,"E35");Q13=makeQuery(id+"Fk14XMOrtsRoLGN_1.opChamfer","BLEND_EDGE",EDGE,{"blendedFrom":[makeQuery(id+"F7.opBoolean","INTERSECT",EDGE,{"derivedFrom":[makeQuery(id+"F1.opRevolve","SWEPT_FACE",FACE,{"disambiguationData":[OSD([sQuery(id+"F0.wireOp",EDGE,"E5"),sQuery(id+"F0.wireOp",EDGE,"E6")])]}),makeQuery(id+"F3.opExtrude","SWEPT_FACE",FACE,{"disambiguationData":[OSD([subQ0])]})]}),makeQuery(id+"F3.opExtrude","CAP_FACE",FACE,{"disambiguationData":[OSD([sQuery(id+"F2.wireOp",EDGE,"E11"),sQuery(id+"F2.wireOp",EDGE,"E12"),sQuery(id+"F2.wireOp",EDGE,"E13"),sQuery(id+"F2.wireOp",EDGE,"E14"),sQuery(id+"F2.wireOp",EDGE,"E15"),sQuery(id+"F2.wireOp",EDGE,"E16"),sQuery(id+"F2.wireOp",EDGE,"E17"),sQuery(id+"F2.wireOp",EDGE,"E18"),sQuery(id+"F2.wireOp",EDGE,"E19"),sQuery(id+"F2.wireOp",EDGE,"E20"),sQuery(id+"F2.wireOp",EDGE,"E21"),sQuery(id+"F2.wireOp",EDGE,"E22"),sQuery(id+"F2.wireOp",EDGE,"E23"),sQuery(id+"F2.wireOp",EDGE,"E24.filletArc"),sQuery(id+"F2.wireOp",EDGE,"E25"),sQuery(id+"F2.wireOp",EDGE,"E26"),sQuery(id+"F2.wireOp",EDGE,"E27.filletArc"),sQuery(id+"F2.wireOp",EDGE,"E28"),sQuery(id+"F2.wireOp",EDGE,"E29"),sQuery(id+"F2.wireOp",EDGE,"E30"),sQuery(id+"F2.wireOp",EDGE,"E31"),sQuery(id+"F2.wireOp",EDGE,"E32"),sQuery(id+"F2.wireOp",EDGE,"E33"),sQuery(id+"F2.wireOp",EDGE,"E34"),subQ0,sQuery(id+"F2.wireOp",EDGE,"E36"),sQuery(id+"F2.wireOp",EDGE,"E37"),sQuery(id+"F2.wireOp",EDGE,"E38"),sQuery(id+"F2.wireOp",EDGE,"E39.filletArc"),sQuery(id+"F2.wireOp",EDGE,"E40.filletArc"),sQuery(id+"F2.wireOp",EDGE,"E41.filletArc"),sQuery(id+"F2.wireOp",EDGE,"E42.filletArc")])],"isStart":false})],"blendedInto":[makeQuery(id+"F3.opExtrude","CAP_FACE",FACE,{"disambiguationData":[OSD([sQuery(id+"F2.wireOp",EDGE,"E11"),sQuery(id+"F2.wireOp",EDGE,"E12"),sQuery(id+"F2.wireOp",EDGE,"E13"),sQuery(id+"F2.wireOp",EDGE,"E14"),sQuery(id+"F2.wireOp",EDGE,"E15"),sQuery(id+"F2.wireOp",EDGE,"E16"),sQuery(id+"F2.wireOp",EDGE,"E17"),sQuery(id+"F2.wireOp",EDGE,"E18"),sQuery(id+"F2.wireOp",EDGE,"E19"),sQuery(id+"F2.wireOp",EDGE,"E20"),sQuery(id+"F2.wireOp",EDGE,"E21"),sQuery(id+"F2.wireOp",EDGE,"E22"),sQuery(id+"F2.wireOp",EDGE,"E23"),sQuery(id+"F2.wireOp",EDGE,"E24.filletArc"),sQuery(id+"F2.wireOp",EDGE,"E25"),sQuery(id+"F2.wireOp",EDGE,"E26"),sQuery(id+"F2.wireOp",EDGE,"E27.filletArc"),sQuery(id+"F2.wireOp",EDGE,"E28"),sQuery(id+"F2.wireOp",EDGE,"E29"),sQuery(id+"F2.wireOp",EDGE,"E30"),sQuery(id+"F2.wireOp",EDGE,"E31"),sQuery(id+"F2.wireOp",EDGE,"E32"),sQuery(id+"F2.wireOp",EDGE,"E33"),sQuery(id+"F2.wireOp",EDGE,"E34"),subQ0,sQuery(id+"F2.wireOp",EDGE,"E36"),sQuery(id+"F2.wireOp",EDGE,"E37"),sQuery(id+"F2.wireOp",EDGE,"E38"),sQuery(id+"F2.wireOp",EDGE,"E39.filletArc"),sQuery(id+"F2.wireOp",EDGE,"E40.filletArc"),sQuery(id+"F2.wireOp",EDGE,"E41.filletArc"),sQuery(id+"F2.wireOp",EDGE,"E42.filletArc")])],"isStart":false})]});}
            var Q14;
            {var subQ0=sQuery(id+"F2.wireOp",EDGE,"E34");Q14=makeQuery(id+"Fk14XMOrtsRoLGN_1.opChamfer","BLEND_EDGE",EDGE,{"blendedFrom":[makeQuery(id+"F7.opBoolean","INTERSECT",EDGE,{"derivedFrom":[makeQuery(id+"F1.opRevolve","SWEPT_FACE",FACE,{"disambiguationData":[OSD([sQuery(id+"F0.wireOp",EDGE,"E5"),sQuery(id+"F0.wireOp",EDGE,"E6")])]}),makeQuery(id+"F3.opExtrude","SWEPT_FACE",FACE,{"disambiguationData":[OSD([subQ0])]})]}),makeQuery(id+"F3.opExtrude","CAP_FACE",FACE,{"disambiguationData":[OSD([sQuery(id+"F2.wireOp",EDGE,"E11"),sQuery(id+"F2.wireOp",EDGE,"E12"),sQuery(id+"F2.wireOp",EDGE,"E13"),sQuery(id+"F2.wireOp",EDGE,"E14"),sQuery(id+"F2.wireOp",EDGE,"E15"),sQuery(id+"F2.wireOp",EDGE,"E16"),sQuery(id+"F2.wireOp",EDGE,"E17"),sQuery(id+"F2.wireOp",EDGE,"E18"),sQuery(id+"F2.wireOp",EDGE,"E19"),sQuery(id+"F2.wireOp",EDGE,"E20"),sQuery(id+"F2.wireOp",EDGE,"E21"),sQuery(id+"F2.wireOp",EDGE,"E22"),sQuery(id+"F2.wireOp",EDGE,"E23"),sQuery(id+"F2.wireOp",EDGE,"E24.filletArc"),sQuery(id+"F2.wireOp",EDGE,"E25"),sQuery(id+"F2.wireOp",EDGE,"E26"),sQuery(id+"F2.wireOp",EDGE,"E27.filletArc"),sQuery(id+"F2.wireOp",EDGE,"E28"),sQuery(id+"F2.wireOp",EDGE,"E29"),sQuery(id+"F2.wireOp",EDGE,"E30"),sQuery(id+"F2.wireOp",EDGE,"E31"),sQuery(id+"F2.wireOp",EDGE,"E32"),sQuery(id+"F2.wireOp",EDGE,"E33"),subQ0,sQuery(id+"F2.wireOp",EDGE,"E35"),sQuery(id+"F2.wireOp",EDGE,"E36"),sQuery(id+"F2.wireOp",EDGE,"E37"),sQuery(id+"F2.wireOp",EDGE,"E38"),sQuery(id+"F2.wireOp",EDGE,"E39.filletArc"),sQuery(id+"F2.wireOp",EDGE,"E40.filletArc"),sQuery(id+"F2.wireOp",EDGE,"E41.filletArc"),sQuery(id+"F2.wireOp",EDGE,"E42.filletArc")])],"isStart":false})],"blendedInto":[makeQuery(id+"F3.opExtrude","CAP_FACE",FACE,{"disambiguationData":[OSD([sQuery(id+"F2.wireOp",EDGE,"E11"),sQuery(id+"F2.wireOp",EDGE,"E12"),sQuery(id+"F2.wireOp",EDGE,"E13"),sQuery(id+"F2.wireOp",EDGE,"E14"),sQuery(id+"F2.wireOp",EDGE,"E15"),sQuery(id+"F2.wireOp",EDGE,"E16"),sQuery(id+"F2.wireOp",EDGE,"E17"),sQuery(id+"F2.wireOp",EDGE,"E18"),sQuery(id+"F2.wireOp",EDGE,"E19"),sQuery(id+"F2.wireOp",EDGE,"E20"),sQuery(id+"F2.wireOp",EDGE,"E21"),sQuery(id+"F2.wireOp",EDGE,"E22"),sQuery(id+"F2.wireOp",EDGE,"E23"),sQuery(id+"F2.wireOp",EDGE,"E24.filletArc"),sQuery(id+"F2.wireOp",EDGE,"E25"),sQuery(id+"F2.wireOp",EDGE,"E26"),sQuery(id+"F2.wireOp",EDGE,"E27.filletArc"),sQuery(id+"F2.wireOp",EDGE,"E28"),sQuery(id+"F2.wireOp",EDGE,"E29"),sQuery(id+"F2.wireOp",EDGE,"E30"),sQuery(id+"F2.wireOp",EDGE,"E31"),sQuery(id+"F2.wireOp",EDGE,"E32"),sQuery(id+"F2.wireOp",EDGE,"E33"),subQ0,sQuery(id+"F2.wireOp",EDGE,"E35"),sQuery(id+"F2.wireOp",EDGE,"E36"),sQuery(id+"F2.wireOp",EDGE,"E37"),sQuery(id+"F2.wireOp",EDGE,"E38"),sQuery(id+"F2.wireOp",EDGE,"E39.filletArc"),sQuery(id+"F2.wireOp",EDGE,"E40.filletArc"),sQuery(id+"F2.wireOp",EDGE,"E41.filletArc"),sQuery(id+"F2.wireOp",EDGE,"E42.filletArc")])],"isStart":false})]});}
            var Q15;
            Q15=makeQuery(id+"F3.opExtrude","CAP_EDGE",EDGE,{"disambiguationData":[OSD([sQuery(id+"F2.wireOp",EDGE,"E20")])],"isStart":false});
            var Q16;
            {var subQ0=sQuery(id+"F2.wireOp",EDGE,"E20");Q16=makeQuery(id+"Fk14XMOrtsRoLGN_1.opChamfer","BLEND_EDGE",EDGE,{"blendedFrom":[makeQuery(id+"F7.opBoolean","INTERSECT",EDGE,{"derivedFrom":[makeQuery(id+"F1.opRevolve","SWEPT_FACE",FACE,{"disambiguationData":[OSD([sQuery(id+"F0.wireOp",EDGE,"E5"),sQuery(id+"F0.wireOp",EDGE,"E6")])]}),makeQuery(id+"F3.opExtrude","SWEPT_FACE",FACE,{"disambiguationData":[OSD([subQ0])]})]}),makeQuery(id+"F3.opExtrude","CAP_FACE",FACE,{"disambiguationData":[OSD([sQuery(id+"F2.wireOp",EDGE,"E11"),sQuery(id+"F2.wireOp",EDGE,"E12"),sQuery(id+"F2.wireOp",EDGE,"E13"),sQuery(id+"F2.wireOp",EDGE,"E14"),sQuery(id+"F2.wireOp",EDGE,"E15"),sQuery(id+"F2.wireOp",EDGE,"E16"),sQuery(id+"F2.wireOp",EDGE,"E17"),sQuery(id+"F2.wireOp",EDGE,"E18"),sQuery(id+"F2.wireOp",EDGE,"E19"),subQ0,sQuery(id+"F2.wireOp",EDGE,"E21"),sQuery(id+"F2.wireOp",EDGE,"E22"),sQuery(id+"F2.wireOp",EDGE,"E23"),sQuery(id+"F2.wireOp",EDGE,"E24.filletArc"),sQuery(id+"F2.wireOp",EDGE,"E25"),sQuery(id+"F2.wireOp",EDGE,"E26"),sQuery(id+"F2.wireOp",EDGE,"E27.filletArc"),sQuery(id+"F2.wireOp",EDGE,"E28"),sQuery(id+"F2.wireOp",EDGE,"E29"),sQuery(id+"F2.wireOp",EDGE,"E30"),sQuery(id+"F2.wireOp",EDGE,"E31"),sQuery(id+"F2.wireOp",EDGE,"E32"),sQuery(id+"F2.wireOp",EDGE,"E33"),sQuery(id+"F2.wireOp",EDGE,"E34"),sQuery(id+"F2.wireOp",EDGE,"E35"),sQuery(id+"F2.wireOp",EDGE,"E36"),sQuery(id+"F2.wireOp",EDGE,"E37"),sQuery(id+"F2.wireOp",EDGE,"E38"),sQuery(id+"F2.wireOp",EDGE,"E39.filletArc"),sQuery(id+"F2.wireOp",EDGE,"E40.filletArc"),sQuery(id+"F2.wireOp",EDGE,"E41.filletArc"),sQuery(id+"F2.wireOp",EDGE,"E42.filletArc")])],"isStart":false})],"blendedInto":[makeQuery(id+"F3.opExtrude","CAP_FACE",FACE,{"disambiguationData":[OSD([sQuery(id+"F2.wireOp",EDGE,"E11"),sQuery(id+"F2.wireOp",EDGE,"E12"),sQuery(id+"F2.wireOp",EDGE,"E13"),sQuery(id+"F2.wireOp",EDGE,"E14"),sQuery(id+"F2.wireOp",EDGE,"E15"),sQuery(id+"F2.wireOp",EDGE,"E16"),sQuery(id+"F2.wireOp",EDGE,"E17"),sQuery(id+"F2.wireOp",EDGE,"E18"),sQuery(id+"F2.wireOp",EDGE,"E19"),subQ0,sQuery(id+"F2.wireOp",EDGE,"E21"),sQuery(id+"F2.wireOp",EDGE,"E22"),sQuery(id+"F2.wireOp",EDGE,"E23"),sQuery(id+"F2.wireOp",EDGE,"E24.filletArc"),sQuery(id+"F2.wireOp",EDGE,"E25"),sQuery(id+"F2.wireOp",EDGE,"E26"),sQuery(id+"F2.wireOp",EDGE,"E27.filletArc"),sQuery(id+"F2.wireOp",EDGE,"E28"),sQuery(id+"F2.wireOp",EDGE,"E29"),sQuery(id+"F2.wireOp",EDGE,"E30"),sQuery(id+"F2.wireOp",EDGE,"E31"),sQuery(id+"F2.wireOp",EDGE,"E32"),sQuery(id+"F2.wireOp",EDGE,"E33"),sQuery(id+"F2.wireOp",EDGE,"E34"),sQuery(id+"F2.wireOp",EDGE,"E35"),sQuery(id+"F2.wireOp",EDGE,"E36"),sQuery(id+"F2.wireOp",EDGE,"E37"),sQuery(id+"F2.wireOp",EDGE,"E38"),sQuery(id+"F2.wireOp",EDGE,"E39.filletArc"),sQuery(id+"F2.wireOp",EDGE,"E40.filletArc"),sQuery(id+"F2.wireOp",EDGE,"E41.filletArc"),sQuery(id+"F2.wireOp",EDGE,"E42.filletArc")])],"isStart":false})]});}
            var Q17;
            {var subQ0=sQuery(id+"F2.wireOp",EDGE,"E19");Q17=makeQuery(id+"Fk14XMOrtsRoLGN_1.opChamfer","BLEND_EDGE",EDGE,{"blendedFrom":[makeQuery(id+"F7.opBoolean","INTERSECT",EDGE,{"derivedFrom":[makeQuery(id+"F1.opRevolve","SWEPT_FACE",FACE,{"disambiguationData":[OSD([sQuery(id+"F0.wireOp",EDGE,"E5"),sQuery(id+"F0.wireOp",EDGE,"E6")])]}),makeQuery(id+"F3.opExtrude","SWEPT_FACE",FACE,{"disambiguationData":[OSD([subQ0])]})]}),makeQuery(id+"F3.opExtrude","CAP_FACE",FACE,{"disambiguationData":[OSD([sQuery(id+"F2.wireOp",EDGE,"E11"),sQuery(id+"F2.wireOp",EDGE,"E12"),sQuery(id+"F2.wireOp",EDGE,"E13"),sQuery(id+"F2.wireOp",EDGE,"E14"),sQuery(id+"F2.wireOp",EDGE,"E15"),sQuery(id+"F2.wireOp",EDGE,"E16"),sQuery(id+"F2.wireOp",EDGE,"E17"),sQuery(id+"F2.wireOp",EDGE,"E18"),subQ0,sQuery(id+"F2.wireOp",EDGE,"E20"),sQuery(id+"F2.wireOp",EDGE,"E21"),sQuery(id+"F2.wireOp",EDGE,"E22"),sQuery(id+"F2.wireOp",EDGE,"E23"),sQuery(id+"F2.wireOp",EDGE,"E24.filletArc"),sQuery(id+"F2.wireOp",EDGE,"E25"),sQuery(id+"F2.wireOp",EDGE,"E26"),sQuery(id+"F2.wireOp",EDGE,"E27.filletArc"),sQuery(id+"F2.wireOp",EDGE,"E28"),sQuery(id+"F2.wireOp",EDGE,"E29"),sQuery(id+"F2.wireOp",EDGE,"E30"),sQuery(id+"F2.wireOp",EDGE,"E31"),sQuery(id+"F2.wireOp",EDGE,"E32"),sQuery(id+"F2.wireOp",EDGE,"E33"),sQuery(id+"F2.wireOp",EDGE,"E34"),sQuery(id+"F2.wireOp",EDGE,"E35"),sQuery(id+"F2.wireOp",EDGE,"E36"),sQuery(id+"F2.wireOp",EDGE,"E37"),sQuery(id+"F2.wireOp",EDGE,"E38"),sQuery(id+"F2.wireOp",EDGE,"E39.filletArc"),sQuery(id+"F2.wireOp",EDGE,"E40.filletArc"),sQuery(id+"F2.wireOp",EDGE,"E41.filletArc"),sQuery(id+"F2.wireOp",EDGE,"E42.filletArc")])],"isStart":false})],"blendedInto":[makeQuery(id+"F3.opExtrude","CAP_FACE",FACE,{"disambiguationData":[OSD([sQuery(id+"F2.wireOp",EDGE,"E11"),sQuery(id+"F2.wireOp",EDGE,"E12"),sQuery(id+"F2.wireOp",EDGE,"E13"),sQuery(id+"F2.wireOp",EDGE,"E14"),sQuery(id+"F2.wireOp",EDGE,"E15"),sQuery(id+"F2.wireOp",EDGE,"E16"),sQuery(id+"F2.wireOp",EDGE,"E17"),sQuery(id+"F2.wireOp",EDGE,"E18"),subQ0,sQuery(id+"F2.wireOp",EDGE,"E20"),sQuery(id+"F2.wireOp",EDGE,"E21"),sQuery(id+"F2.wireOp",EDGE,"E22"),sQuery(id+"F2.wireOp",EDGE,"E23"),sQuery(id+"F2.wireOp",EDGE,"E24.filletArc"),sQuery(id+"F2.wireOp",EDGE,"E25"),sQuery(id+"F2.wireOp",EDGE,"E26"),sQuery(id+"F2.wireOp",EDGE,"E27.filletArc"),sQuery(id+"F2.wireOp",EDGE,"E28"),sQuery(id+"F2.wireOp",EDGE,"E29"),sQuery(id+"F2.wireOp",EDGE,"E30"),sQuery(id+"F2.wireOp",EDGE,"E31"),sQuery(id+"F2.wireOp",EDGE,"E32"),sQuery(id+"F2.wireOp",EDGE,"E33"),sQuery(id+"F2.wireOp",EDGE,"E34"),sQuery(id+"F2.wireOp",EDGE,"E35"),sQuery(id+"F2.wireOp",EDGE,"E36"),sQuery(id+"F2.wireOp",EDGE,"E37"),sQuery(id+"F2.wireOp",EDGE,"E38"),sQuery(id+"F2.wireOp",EDGE,"E39.filletArc"),sQuery(id+"F2.wireOp",EDGE,"E40.filletArc"),sQuery(id+"F2.wireOp",EDGE,"E41.filletArc"),sQuery(id+"F2.wireOp",EDGE,"E42.filletArc")])],"isStart":false})]});}
            var Q18;
            {var subQ0=sQuery(id+"F2.wireOp",EDGE,"E18");Q18=makeQuery(id+"Fk14XMOrtsRoLGN_1.opChamfer","BLEND_EDGE",EDGE,{"blendedFrom":[makeQuery(id+"F7.opBoolean","INTERSECT",EDGE,{"derivedFrom":[makeQuery(id+"F1.opRevolve","SWEPT_FACE",FACE,{"disambiguationData":[OSD([sQuery(id+"F0.wireOp",EDGE,"E5"),sQuery(id+"F0.wireOp",EDGE,"E6")])]}),makeQuery(id+"F3.opExtrude","SWEPT_FACE",FACE,{"disambiguationData":[OSD([subQ0])]})]}),makeQuery(id+"F3.opExtrude","CAP_FACE",FACE,{"disambiguationData":[OSD([sQuery(id+"F2.wireOp",EDGE,"E11"),sQuery(id+"F2.wireOp",EDGE,"E12"),sQuery(id+"F2.wireOp",EDGE,"E13"),sQuery(id+"F2.wireOp",EDGE,"E14"),sQuery(id+"F2.wireOp",EDGE,"E15"),sQuery(id+"F2.wireOp",EDGE,"E16"),sQuery(id+"F2.wireOp",EDGE,"E17"),subQ0,sQuery(id+"F2.wireOp",EDGE,"E19"),sQuery(id+"F2.wireOp",EDGE,"E20"),sQuery(id+"F2.wireOp",EDGE,"E21"),sQuery(id+"F2.wireOp",EDGE,"E22"),sQuery(id+"F2.wireOp",EDGE,"E23"),sQuery(id+"F2.wireOp",EDGE,"E24.filletArc"),sQuery(id+"F2.wireOp",EDGE,"E25"),sQuery(id+"F2.wireOp",EDGE,"E26"),sQuery(id+"F2.wireOp",EDGE,"E27.filletArc"),sQuery(id+"F2.wireOp",EDGE,"E28"),sQuery(id+"F2.wireOp",EDGE,"E29"),sQuery(id+"F2.wireOp",EDGE,"E30"),sQuery(id+"F2.wireOp",EDGE,"E31"),sQuery(id+"F2.wireOp",EDGE,"E32"),sQuery(id+"F2.wireOp",EDGE,"E33"),sQuery(id+"F2.wireOp",EDGE,"E34"),sQuery(id+"F2.wireOp",EDGE,"E35"),sQuery(id+"F2.wireOp",EDGE,"E36"),sQuery(id+"F2.wireOp",EDGE,"E37"),sQuery(id+"F2.wireOp",EDGE,"E38"),sQuery(id+"F2.wireOp",EDGE,"E39.filletArc"),sQuery(id+"F2.wireOp",EDGE,"E40.filletArc"),sQuery(id+"F2.wireOp",EDGE,"E41.filletArc"),sQuery(id+"F2.wireOp",EDGE,"E42.filletArc")])],"isStart":false})],"blendedInto":[makeQuery(id+"F3.opExtrude","CAP_FACE",FACE,{"disambiguationData":[OSD([sQuery(id+"F2.wireOp",EDGE,"E11"),sQuery(id+"F2.wireOp",EDGE,"E12"),sQuery(id+"F2.wireOp",EDGE,"E13"),sQuery(id+"F2.wireOp",EDGE,"E14"),sQuery(id+"F2.wireOp",EDGE,"E15"),sQuery(id+"F2.wireOp",EDGE,"E16"),sQuery(id+"F2.wireOp",EDGE,"E17"),subQ0,sQuery(id+"F2.wireOp",EDGE,"E19"),sQuery(id+"F2.wireOp",EDGE,"E20"),sQuery(id+"F2.wireOp",EDGE,"E21"),sQuery(id+"F2.wireOp",EDGE,"E22"),sQuery(id+"F2.wireOp",EDGE,"E23"),sQuery(id+"F2.wireOp",EDGE,"E24.filletArc"),sQuery(id+"F2.wireOp",EDGE,"E25"),sQuery(id+"F2.wireOp",EDGE,"E26"),sQuery(id+"F2.wireOp",EDGE,"E27.filletArc"),sQuery(id+"F2.wireOp",EDGE,"E28"),sQuery(id+"F2.wireOp",EDGE,"E29"),sQuery(id+"F2.wireOp",EDGE,"E30"),sQuery(id+"F2.wireOp",EDGE,"E31"),sQuery(id+"F2.wireOp",EDGE,"E32"),sQuery(id+"F2.wireOp",EDGE,"E33"),sQuery(id+"F2.wireOp",EDGE,"E34"),sQuery(id+"F2.wireOp",EDGE,"E35"),sQuery(id+"F2.wireOp",EDGE,"E36"),sQuery(id+"F2.wireOp",EDGE,"E37"),sQuery(id+"F2.wireOp",EDGE,"E38"),sQuery(id+"F2.wireOp",EDGE,"E39.filletArc"),sQuery(id+"F2.wireOp",EDGE,"E40.filletArc"),sQuery(id+"F2.wireOp",EDGE,"E41.filletArc"),sQuery(id+"F2.wireOp",EDGE,"E42.filletArc")])],"isStart":false})]});}
            var Q19;
            Q19=makeQuery(id+"F3.opExtrude","CAP_EDGE",EDGE,{"disambiguationData":[OSD([sQuery(id+"F2.wireOp",EDGE,"E14")])],"isStart":true});
            var Q20;
            Q20=makeQuery(id+"F3.opExtrude","CAP_EDGE",EDGE,{"disambiguationData":[OSD([sQuery(id+"F2.wireOp",EDGE,"E36")])],"isStart":true});
            var Q21;
            Q21=makeQuery(id+"F3.opExtrude","CAP_EDGE",EDGE,{"disambiguationData":[OSD([sQuery(id+"F2.wireOp",EDGE,"E20")])],"isStart":true});
            var Q22;
            Q22=makeQuery(id+"F3.opExtrude","CAP_EDGE",EDGE,{"disambiguationData":[OSD([sQuery(id+"F2.wireOp",EDGE,"E33")])],"isStart":true});
            var Q23;
            Q23=makeQuery(id+"F3.opExtrude","CAP_EDGE",EDGE,{"disambiguationData":[OSD([sQuery(id+"F2.wireOp",EDGE,"E31")])],"isStart":true});
            var Q24;
            Q24=makeQuery(id+"F3.opExtrude","CAP_EDGE",EDGE,{"disambiguationData":[OSD([sQuery(id+"F2.wireOp",EDGE,"E34")])],"isStart":true});
            var Q25;
            Q25=makeQuery(id+"F3.opExtrude","CAP_EDGE",EDGE,{"disambiguationData":[OSD([sQuery(id+"F2.wireOp",EDGE,"E30")])],"isStart":true});
            var Q26;
            Q26=makeQuery(id+"F3.opExtrude","CAP_EDGE",EDGE,{"disambiguationData":[OSD([sQuery(id+"F2.wireOp",EDGE,"E25")])],"isStart":true});
            var Q27;
            {var subQ0=sQuery(id+"F2.wireOp",EDGE,"E19");Q27=makeQuery(id+"Fk14XMOrtsRoLGN_1.opChamfer","BLEND_EDGE",EDGE,{"blendedFrom":[makeQuery(id+"F7.opBoolean","INTERSECT",EDGE,{"derivedFrom":[makeQuery(id+"F1.opRevolve","SWEPT_FACE",FACE,{"disambiguationData":[OSD([sQuery(id+"F0.wireOp",EDGE,"E5"),sQuery(id+"F0.wireOp",EDGE,"E6")])]}),makeQuery(id+"F3.opExtrude","SWEPT_FACE",FACE,{"disambiguationData":[OSD([subQ0])]})]}),makeQuery(id+"F7.opBoolean","MERGE",FACE,{"derivedFrom":[makeQuery(id+"F3.opExtrude","CAP_FACE",FACE,{"disambiguationData":[OSD([sQuery(id+"F2.wireOp",EDGE,"E10.0"),sQuery(id+"F2.wireOp",EDGE,"E10.1"),sQuery(id+"F2.wireOp",EDGE,"E10.2"),sQuery(id+"F2.wireOp",EDGE,"E10.3"),sQuery(id+"F2.wireOp",EDGE,"E10.4"),sQuery(id+"F2.wireOp",EDGE,"E10.5")])],"isStart":true}),makeQuery(id+"F3.opExtrude","CAP_FACE",FACE,{"disambiguationData":[OSD([sQuery(id+"F2.wireOp",EDGE,"E11"),sQuery(id+"F2.wireOp",EDGE,"E12"),sQuery(id+"F2.wireOp",EDGE,"E13"),sQuery(id+"F2.wireOp",EDGE,"E14"),sQuery(id+"F2.wireOp",EDGE,"E15"),sQuery(id+"F2.wireOp",EDGE,"E16"),sQuery(id+"F2.wireOp",EDGE,"E17"),sQuery(id+"F2.wireOp",EDGE,"E18"),subQ0,sQuery(id+"F2.wireOp",EDGE,"E20"),sQuery(id+"F2.wireOp",EDGE,"E21"),sQuery(id+"F2.wireOp",EDGE,"E22"),sQuery(id+"F2.wireOp",EDGE,"E23"),sQuery(id+"F2.wireOp",EDGE,"E24.filletArc"),sQuery(id+"F2.wireOp",EDGE,"E25"),sQuery(id+"F2.wireOp",EDGE,"E26"),sQuery(id+"F2.wireOp",EDGE,"E27.filletArc"),sQuery(id+"F2.wireOp",EDGE,"E28"),sQuery(id+"F2.wireOp",EDGE,"E29"),sQuery(id+"F2.wireOp",EDGE,"E30"),sQuery(id+"F2.wireOp",EDGE,"E31"),sQuery(id+"F2.wireOp",EDGE,"E32"),sQuery(id+"F2.wireOp",EDGE,"E33"),sQuery(id+"F2.wireOp",EDGE,"E34"),sQuery(id+"F2.wireOp",EDGE,"E35"),sQuery(id+"F2.wireOp",EDGE,"E36"),sQuery(id+"F2.wireOp",EDGE,"E37"),sQuery(id+"F2.wireOp",EDGE,"E38"),sQuery(id+"F2.wireOp",EDGE,"E39.filletArc"),sQuery(id+"F2.wireOp",EDGE,"E40.filletArc"),sQuery(id+"F2.wireOp",EDGE,"E41.filletArc"),sQuery(id+"F2.wireOp",EDGE,"E42.filletArc")])],"isStart":true}),makeQuery(id+"F6.opExtrude","CAP_FACE",FACE,{"disambiguationData":[OSD([sQuery(id+"F4.wireOp",EDGE,"E43"),sQuery(id+"F4.wireOp",EDGE,"E44.0"),sQuery(id+"F4.wireOp",EDGE,"E44.1"),sQuery(id+"F4.wireOp",EDGE,"E44.2"),sQuery(id+"F4.wireOp",EDGE,"E44.3"),sQuery(id+"F4.wireOp",EDGE,"E44.4"),sQuery(id+"F4.wireOp",EDGE,"E44.5")])],"isStart":false})]})],"blendedInto":[makeQuery(id+"F7.opBoolean","MERGE",FACE,{"derivedFrom":[makeQuery(id+"F3.opExtrude","CAP_FACE",FACE,{"disambiguationData":[OSD([sQuery(id+"F2.wireOp",EDGE,"E10.0"),sQuery(id+"F2.wireOp",EDGE,"E10.1"),sQuery(id+"F2.wireOp",EDGE,"E10.2"),sQuery(id+"F2.wireOp",EDGE,"E10.3"),sQuery(id+"F2.wireOp",EDGE,"E10.4"),sQuery(id+"F2.wireOp",EDGE,"E10.5")])],"isStart":true}),makeQuery(id+"F3.opExtrude","CAP_FACE",FACE,{"disambiguationData":[OSD([sQuery(id+"F2.wireOp",EDGE,"E11"),sQuery(id+"F2.wireOp",EDGE,"E12"),sQuery(id+"F2.wireOp",EDGE,"E13"),sQuery(id+"F2.wireOp",EDGE,"E14"),sQuery(id+"F2.wireOp",EDGE,"E15"),sQuery(id+"F2.wireOp",EDGE,"E16"),sQuery(id+"F2.wireOp",EDGE,"E17"),sQuery(id+"F2.wireOp",EDGE,"E18"),subQ0,sQuery(id+"F2.wireOp",EDGE,"E20"),sQuery(id+"F2.wireOp",EDGE,"E21"),sQuery(id+"F2.wireOp",EDGE,"E22"),sQuery(id+"F2.wireOp",EDGE,"E23"),sQuery(id+"F2.wireOp",EDGE,"E24.filletArc"),sQuery(id+"F2.wireOp",EDGE,"E25"),sQuery(id+"F2.wireOp",EDGE,"E26"),sQuery(id+"F2.wireOp",EDGE,"E27.filletArc"),sQuery(id+"F2.wireOp",EDGE,"E28"),sQuery(id+"F2.wireOp",EDGE,"E29"),sQuery(id+"F2.wireOp",EDGE,"E30"),sQuery(id+"F2.wireOp",EDGE,"E31"),sQuery(id+"F2.wireOp",EDGE,"E32"),sQuery(id+"F2.wireOp",EDGE,"E33"),sQuery(id+"F2.wireOp",EDGE,"E34"),sQuery(id+"F2.wireOp",EDGE,"E35"),sQuery(id+"F2.wireOp",EDGE,"E36"),sQuery(id+"F2.wireOp",EDGE,"E37"),sQuery(id+"F2.wireOp",EDGE,"E38"),sQuery(id+"F2.wireOp",EDGE,"E39.filletArc"),sQuery(id+"F2.wireOp",EDGE,"E40.filletArc"),sQuery(id+"F2.wireOp",EDGE,"E41.filletArc"),sQuery(id+"F2.wireOp",EDGE,"E42.filletArc")])],"isStart":true}),makeQuery(id+"F6.opExtrude","CAP_FACE",FACE,{"disambiguationData":[OSD([sQuery(id+"F4.wireOp",EDGE,"E43"),sQuery(id+"F4.wireOp",EDGE,"E44.0"),sQuery(id+"F4.wireOp",EDGE,"E44.1"),sQuery(id+"F4.wireOp",EDGE,"E44.2"),sQuery(id+"F4.wireOp",EDGE,"E44.3"),sQuery(id+"F4.wireOp",EDGE,"E44.4"),sQuery(id+"F4.wireOp",EDGE,"E44.5")])],"isStart":false})]})]});}
            var Q28;
            {var subQ0=sQuery(id+"F2.wireOp",EDGE,"E20");Q28=makeQuery(id+"Fk14XMOrtsRoLGN_1.opChamfer","BLEND_EDGE",EDGE,{"blendedFrom":[makeQuery(id+"F7.opBoolean","INTERSECT",EDGE,{"derivedFrom":[makeQuery(id+"F1.opRevolve","SWEPT_FACE",FACE,{"disambiguationData":[OSD([sQuery(id+"F0.wireOp",EDGE,"E5"),sQuery(id+"F0.wireOp",EDGE,"E6")])]}),makeQuery(id+"F3.opExtrude","SWEPT_FACE",FACE,{"disambiguationData":[OSD([subQ0])]})]}),makeQuery(id+"F7.opBoolean","MERGE",FACE,{"derivedFrom":[makeQuery(id+"F3.opExtrude","CAP_FACE",FACE,{"disambiguationData":[OSD([sQuery(id+"F2.wireOp",EDGE,"E10.0"),sQuery(id+"F2.wireOp",EDGE,"E10.1"),sQuery(id+"F2.wireOp",EDGE,"E10.2"),sQuery(id+"F2.wireOp",EDGE,"E10.3"),sQuery(id+"F2.wireOp",EDGE,"E10.4"),sQuery(id+"F2.wireOp",EDGE,"E10.5")])],"isStart":true}),makeQuery(id+"F3.opExtrude","CAP_FACE",FACE,{"disambiguationData":[OSD([sQuery(id+"F2.wireOp",EDGE,"E11"),sQuery(id+"F2.wireOp",EDGE,"E12"),sQuery(id+"F2.wireOp",EDGE,"E13"),sQuery(id+"F2.wireOp",EDGE,"E14"),sQuery(id+"F2.wireOp",EDGE,"E15"),sQuery(id+"F2.wireOp",EDGE,"E16"),sQuery(id+"F2.wireOp",EDGE,"E17"),sQuery(id+"F2.wireOp",EDGE,"E18"),sQuery(id+"F2.wireOp",EDGE,"E19"),subQ0,sQuery(id+"F2.wireOp",EDGE,"E21"),sQuery(id+"F2.wireOp",EDGE,"E22"),sQuery(id+"F2.wireOp",EDGE,"E23"),sQuery(id+"F2.wireOp",EDGE,"E24.filletArc"),sQuery(id+"F2.wireOp",EDGE,"E25"),sQuery(id+"F2.wireOp",EDGE,"E26"),sQuery(id+"F2.wireOp",EDGE,"E27.filletArc"),sQuery(id+"F2.wireOp",EDGE,"E28"),sQuery(id+"F2.wireOp",EDGE,"E29"),sQuery(id+"F2.wireOp",EDGE,"E30"),sQuery(id+"F2.wireOp",EDGE,"E31"),sQuery(id+"F2.wireOp",EDGE,"E32"),sQuery(id+"F2.wireOp",EDGE,"E33"),sQuery(id+"F2.wireOp",EDGE,"E34"),sQuery(id+"F2.wireOp",EDGE,"E35"),sQuery(id+"F2.wireOp",EDGE,"E36"),sQuery(id+"F2.wireOp",EDGE,"E37"),sQuery(id+"F2.wireOp",EDGE,"E38"),sQuery(id+"F2.wireOp",EDGE,"E39.filletArc"),sQuery(id+"F2.wireOp",EDGE,"E40.filletArc"),sQuery(id+"F2.wireOp",EDGE,"E41.filletArc"),sQuery(id+"F2.wireOp",EDGE,"E42.filletArc")])],"isStart":true}),makeQuery(id+"F6.opExtrude","CAP_FACE",FACE,{"disambiguationData":[OSD([sQuery(id+"F4.wireOp",EDGE,"E43"),sQuery(id+"F4.wireOp",EDGE,"E44.0"),sQuery(id+"F4.wireOp",EDGE,"E44.1"),sQuery(id+"F4.wireOp",EDGE,"E44.2"),sQuery(id+"F4.wireOp",EDGE,"E44.3"),sQuery(id+"F4.wireOp",EDGE,"E44.4"),sQuery(id+"F4.wireOp",EDGE,"E44.5")])],"isStart":false})]})],"blendedInto":[makeQuery(id+"F7.opBoolean","MERGE",FACE,{"derivedFrom":[makeQuery(id+"F3.opExtrude","CAP_FACE",FACE,{"disambiguationData":[OSD([sQuery(id+"F2.wireOp",EDGE,"E10.0"),sQuery(id+"F2.wireOp",EDGE,"E10.1"),sQuery(id+"F2.wireOp",EDGE,"E10.2"),sQuery(id+"F2.wireOp",EDGE,"E10.3"),sQuery(id+"F2.wireOp",EDGE,"E10.4"),sQuery(id+"F2.wireOp",EDGE,"E10.5")])],"isStart":true}),makeQuery(id+"F3.opExtrude","CAP_FACE",FACE,{"disambiguationData":[OSD([sQuery(id+"F2.wireOp",EDGE,"E11"),sQuery(id+"F2.wireOp",EDGE,"E12"),sQuery(id+"F2.wireOp",EDGE,"E13"),sQuery(id+"F2.wireOp",EDGE,"E14"),sQuery(id+"F2.wireOp",EDGE,"E15"),sQuery(id+"F2.wireOp",EDGE,"E16"),sQuery(id+"F2.wireOp",EDGE,"E17"),sQuery(id+"F2.wireOp",EDGE,"E18"),sQuery(id+"F2.wireOp",EDGE,"E19"),subQ0,sQuery(id+"F2.wireOp",EDGE,"E21"),sQuery(id+"F2.wireOp",EDGE,"E22"),sQuery(id+"F2.wireOp",EDGE,"E23"),sQuery(id+"F2.wireOp",EDGE,"E24.filletArc"),sQuery(id+"F2.wireOp",EDGE,"E25"),sQuery(id+"F2.wireOp",EDGE,"E26"),sQuery(id+"F2.wireOp",EDGE,"E27.filletArc"),sQuery(id+"F2.wireOp",EDGE,"E28"),sQuery(id+"F2.wireOp",EDGE,"E29"),sQuery(id+"F2.wireOp",EDGE,"E30"),sQuery(id+"F2.wireOp",EDGE,"E31"),sQuery(id+"F2.wireOp",EDGE,"E32"),sQuery(id+"F2.wireOp",EDGE,"E33"),sQuery(id+"F2.wireOp",EDGE,"E34"),sQuery(id+"F2.wireOp",EDGE,"E35"),sQuery(id+"F2.wireOp",EDGE,"E36"),sQuery(id+"F2.wireOp",EDGE,"E37"),sQuery(id+"F2.wireOp",EDGE,"E38"),sQuery(id+"F2.wireOp",EDGE,"E39.filletArc"),sQuery(id+"F2.wireOp",EDGE,"E40.filletArc"),sQuery(id+"F2.wireOp",EDGE,"E41.filletArc"),sQuery(id+"F2.wireOp",EDGE,"E42.filletArc")])],"isStart":true}),makeQuery(id+"F6.opExtrude","CAP_FACE",FACE,{"disambiguationData":[OSD([sQuery(id+"F4.wireOp",EDGE,"E43"),sQuery(id+"F4.wireOp",EDGE,"E44.0"),sQuery(id+"F4.wireOp",EDGE,"E44.1"),sQuery(id+"F4.wireOp",EDGE,"E44.2"),sQuery(id+"F4.wireOp",EDGE,"E44.3"),sQuery(id+"F4.wireOp",EDGE,"E44.4"),sQuery(id+"F4.wireOp",EDGE,"E44.5")])],"isStart":false})]})]});}
            var Q29;
            {var subQ0=sQuery(id+"F2.wireOp",EDGE,"E18");Q29=makeQuery(id+"Fk14XMOrtsRoLGN_1.opChamfer","BLEND_EDGE",EDGE,{"blendedFrom":[makeQuery(id+"F7.opBoolean","INTERSECT",EDGE,{"derivedFrom":[makeQuery(id+"F1.opRevolve","SWEPT_FACE",FACE,{"disambiguationData":[OSD([sQuery(id+"F0.wireOp",EDGE,"E5"),sQuery(id+"F0.wireOp",EDGE,"E6")])]}),makeQuery(id+"F3.opExtrude","SWEPT_FACE",FACE,{"disambiguationData":[OSD([subQ0])]})]}),makeQuery(id+"F7.opBoolean","MERGE",FACE,{"derivedFrom":[makeQuery(id+"F3.opExtrude","CAP_FACE",FACE,{"disambiguationData":[OSD([sQuery(id+"F2.wireOp",EDGE,"E10.0"),sQuery(id+"F2.wireOp",EDGE,"E10.1"),sQuery(id+"F2.wireOp",EDGE,"E10.2"),sQuery(id+"F2.wireOp",EDGE,"E10.3"),sQuery(id+"F2.wireOp",EDGE,"E10.4"),sQuery(id+"F2.wireOp",EDGE,"E10.5")])],"isStart":true}),makeQuery(id+"F3.opExtrude","CAP_FACE",FACE,{"disambiguationData":[OSD([sQuery(id+"F2.wireOp",EDGE,"E11"),sQuery(id+"F2.wireOp",EDGE,"E12"),sQuery(id+"F2.wireOp",EDGE,"E13"),sQuery(id+"F2.wireOp",EDGE,"E14"),sQuery(id+"F2.wireOp",EDGE,"E15"),sQuery(id+"F2.wireOp",EDGE,"E16"),sQuery(id+"F2.wireOp",EDGE,"E17"),subQ0,sQuery(id+"F2.wireOp",EDGE,"E19"),sQuery(id+"F2.wireOp",EDGE,"E20"),sQuery(id+"F2.wireOp",EDGE,"E21"),sQuery(id+"F2.wireOp",EDGE,"E22"),sQuery(id+"F2.wireOp",EDGE,"E23"),sQuery(id+"F2.wireOp",EDGE,"E24.filletArc"),sQuery(id+"F2.wireOp",EDGE,"E25"),sQuery(id+"F2.wireOp",EDGE,"E26"),sQuery(id+"F2.wireOp",EDGE,"E27.filletArc"),sQuery(id+"F2.wireOp",EDGE,"E28"),sQuery(id+"F2.wireOp",EDGE,"E29"),sQuery(id+"F2.wireOp",EDGE,"E30"),sQuery(id+"F2.wireOp",EDGE,"E31"),sQuery(id+"F2.wireOp",EDGE,"E32"),sQuery(id+"F2.wireOp",EDGE,"E33"),sQuery(id+"F2.wireOp",EDGE,"E34"),sQuery(id+"F2.wireOp",EDGE,"E35"),sQuery(id+"F2.wireOp",EDGE,"E36"),sQuery(id+"F2.wireOp",EDGE,"E37"),sQuery(id+"F2.wireOp",EDGE,"E38"),sQuery(id+"F2.wireOp",EDGE,"E39.filletArc"),sQuery(id+"F2.wireOp",EDGE,"E40.filletArc"),sQuery(id+"F2.wireOp",EDGE,"E41.filletArc"),sQuery(id+"F2.wireOp",EDGE,"E42.filletArc")])],"isStart":true}),makeQuery(id+"F6.opExtrude","CAP_FACE",FACE,{"disambiguationData":[OSD([sQuery(id+"F4.wireOp",EDGE,"E43"),sQuery(id+"F4.wireOp",EDGE,"E44.0"),sQuery(id+"F4.wireOp",EDGE,"E44.1"),sQuery(id+"F4.wireOp",EDGE,"E44.2"),sQuery(id+"F4.wireOp",EDGE,"E44.3"),sQuery(id+"F4.wireOp",EDGE,"E44.4"),sQuery(id+"F4.wireOp",EDGE,"E44.5")])],"isStart":false})]})],"blendedInto":[makeQuery(id+"F7.opBoolean","MERGE",FACE,{"derivedFrom":[makeQuery(id+"F3.opExtrude","CAP_FACE",FACE,{"disambiguationData":[OSD([sQuery(id+"F2.wireOp",EDGE,"E10.0"),sQuery(id+"F2.wireOp",EDGE,"E10.1"),sQuery(id+"F2.wireOp",EDGE,"E10.2"),sQuery(id+"F2.wireOp",EDGE,"E10.3"),sQuery(id+"F2.wireOp",EDGE,"E10.4"),sQuery(id+"F2.wireOp",EDGE,"E10.5")])],"isStart":true}),makeQuery(id+"F3.opExtrude","CAP_FACE",FACE,{"disambiguationData":[OSD([sQuery(id+"F2.wireOp",EDGE,"E11"),sQuery(id+"F2.wireOp",EDGE,"E12"),sQuery(id+"F2.wireOp",EDGE,"E13"),sQuery(id+"F2.wireOp",EDGE,"E14"),sQuery(id+"F2.wireOp",EDGE,"E15"),sQuery(id+"F2.wireOp",EDGE,"E16"),sQuery(id+"F2.wireOp",EDGE,"E17"),subQ0,sQuery(id+"F2.wireOp",EDGE,"E19"),sQuery(id+"F2.wireOp",EDGE,"E20"),sQuery(id+"F2.wireOp",EDGE,"E21"),sQuery(id+"F2.wireOp",EDGE,"E22"),sQuery(id+"F2.wireOp",EDGE,"E23"),sQuery(id+"F2.wireOp",EDGE,"E24.filletArc"),sQuery(id+"F2.wireOp",EDGE,"E25"),sQuery(id+"F2.wireOp",EDGE,"E26"),sQuery(id+"F2.wireOp",EDGE,"E27.filletArc"),sQuery(id+"F2.wireOp",EDGE,"E28"),sQuery(id+"F2.wireOp",EDGE,"E29"),sQuery(id+"F2.wireOp",EDGE,"E30"),sQuery(id+"F2.wireOp",EDGE,"E31"),sQuery(id+"F2.wireOp",EDGE,"E32"),sQuery(id+"F2.wireOp",EDGE,"E33"),sQuery(id+"F2.wireOp",EDGE,"E34"),sQuery(id+"F2.wireOp",EDGE,"E35"),sQuery(id+"F2.wireOp",EDGE,"E36"),sQuery(id+"F2.wireOp",EDGE,"E37"),sQuery(id+"F2.wireOp",EDGE,"E38"),sQuery(id+"F2.wireOp",EDGE,"E39.filletArc"),sQuery(id+"F2.wireOp",EDGE,"E40.filletArc"),sQuery(id+"F2.wireOp",EDGE,"E41.filletArc"),sQuery(id+"F2.wireOp",EDGE,"E42.filletArc")])],"isStart":true}),makeQuery(id+"F6.opExtrude","CAP_FACE",FACE,{"disambiguationData":[OSD([sQuery(id+"F4.wireOp",EDGE,"E43"),sQuery(id+"F4.wireOp",EDGE,"E44.0"),sQuery(id+"F4.wireOp",EDGE,"E44.1"),sQuery(id+"F4.wireOp",EDGE,"E44.2"),sQuery(id+"F4.wireOp",EDGE,"E44.3"),sQuery(id+"F4.wireOp",EDGE,"E44.4"),sQuery(id+"F4.wireOp",EDGE,"E44.5")])],"isStart":false})]})]});}
            var Q30;
            {var subQ0=sQuery(id+"F2.wireOp",EDGE,"E17");Q30=makeQuery(id+"Fk14XMOrtsRoLGN_1.opChamfer","BLEND_EDGE",EDGE,{"blendedFrom":[makeQuery(id+"F7.opBoolean","INTERSECT",EDGE,{"derivedFrom":[makeQuery(id+"F1.opRevolve","SWEPT_FACE",FACE,{"disambiguationData":[OSD([sQuery(id+"F0.wireOp",EDGE,"E5"),sQuery(id+"F0.wireOp",EDGE,"E6")])]}),makeQuery(id+"F3.opExtrude","SWEPT_FACE",FACE,{"disambiguationData":[OSD([subQ0])]})]}),makeQuery(id+"F7.opBoolean","MERGE",FACE,{"derivedFrom":[makeQuery(id+"F3.opExtrude","CAP_FACE",FACE,{"disambiguationData":[OSD([sQuery(id+"F2.wireOp",EDGE,"E10.0"),sQuery(id+"F2.wireOp",EDGE,"E10.1"),sQuery(id+"F2.wireOp",EDGE,"E10.2"),sQuery(id+"F2.wireOp",EDGE,"E10.3"),sQuery(id+"F2.wireOp",EDGE,"E10.4"),sQuery(id+"F2.wireOp",EDGE,"E10.5")])],"isStart":true}),makeQuery(id+"F3.opExtrude","CAP_FACE",FACE,{"disambiguationData":[OSD([sQuery(id+"F2.wireOp",EDGE,"E11"),sQuery(id+"F2.wireOp",EDGE,"E12"),sQuery(id+"F2.wireOp",EDGE,"E13"),sQuery(id+"F2.wireOp",EDGE,"E14"),sQuery(id+"F2.wireOp",EDGE,"E15"),sQuery(id+"F2.wireOp",EDGE,"E16"),subQ0,sQuery(id+"F2.wireOp",EDGE,"E18"),sQuery(id+"F2.wireOp",EDGE,"E19"),sQuery(id+"F2.wireOp",EDGE,"E20"),sQuery(id+"F2.wireOp",EDGE,"E21"),sQuery(id+"F2.wireOp",EDGE,"E22"),sQuery(id+"F2.wireOp",EDGE,"E23"),sQuery(id+"F2.wireOp",EDGE,"E24.filletArc"),sQuery(id+"F2.wireOp",EDGE,"E25"),sQuery(id+"F2.wireOp",EDGE,"E26"),sQuery(id+"F2.wireOp",EDGE,"E27.filletArc"),sQuery(id+"F2.wireOp",EDGE,"E28"),sQuery(id+"F2.wireOp",EDGE,"E29"),sQuery(id+"F2.wireOp",EDGE,"E30"),sQuery(id+"F2.wireOp",EDGE,"E31"),sQuery(id+"F2.wireOp",EDGE,"E32"),sQuery(id+"F2.wireOp",EDGE,"E33"),sQuery(id+"F2.wireOp",EDGE,"E34"),sQuery(id+"F2.wireOp",EDGE,"E35"),sQuery(id+"F2.wireOp",EDGE,"E36"),sQuery(id+"F2.wireOp",EDGE,"E37"),sQuery(id+"F2.wireOp",EDGE,"E38"),sQuery(id+"F2.wireOp",EDGE,"E39.filletArc"),sQuery(id+"F2.wireOp",EDGE,"E40.filletArc"),sQuery(id+"F2.wireOp",EDGE,"E41.filletArc"),sQuery(id+"F2.wireOp",EDGE,"E42.filletArc")])],"isStart":true}),makeQuery(id+"F6.opExtrude","CAP_FACE",FACE,{"disambiguationData":[OSD([sQuery(id+"F4.wireOp",EDGE,"E43"),sQuery(id+"F4.wireOp",EDGE,"E44.0"),sQuery(id+"F4.wireOp",EDGE,"E44.1"),sQuery(id+"F4.wireOp",EDGE,"E44.2"),sQuery(id+"F4.wireOp",EDGE,"E44.3"),sQuery(id+"F4.wireOp",EDGE,"E44.4"),sQuery(id+"F4.wireOp",EDGE,"E44.5")])],"isStart":false})]})],"blendedInto":[makeQuery(id+"F7.opBoolean","MERGE",FACE,{"derivedFrom":[makeQuery(id+"F3.opExtrude","CAP_FACE",FACE,{"disambiguationData":[OSD([sQuery(id+"F2.wireOp",EDGE,"E10.0"),sQuery(id+"F2.wireOp",EDGE,"E10.1"),sQuery(id+"F2.wireOp",EDGE,"E10.2"),sQuery(id+"F2.wireOp",EDGE,"E10.3"),sQuery(id+"F2.wireOp",EDGE,"E10.4"),sQuery(id+"F2.wireOp",EDGE,"E10.5")])],"isStart":true}),makeQuery(id+"F3.opExtrude","CAP_FACE",FACE,{"disambiguationData":[OSD([sQuery(id+"F2.wireOp",EDGE,"E11"),sQuery(id+"F2.wireOp",EDGE,"E12"),sQuery(id+"F2.wireOp",EDGE,"E13"),sQuery(id+"F2.wireOp",EDGE,"E14"),sQuery(id+"F2.wireOp",EDGE,"E15"),sQuery(id+"F2.wireOp",EDGE,"E16"),subQ0,sQuery(id+"F2.wireOp",EDGE,"E18"),sQuery(id+"F2.wireOp",EDGE,"E19"),sQuery(id+"F2.wireOp",EDGE,"E20"),sQuery(id+"F2.wireOp",EDGE,"E21"),sQuery(id+"F2.wireOp",EDGE,"E22"),sQuery(id+"F2.wireOp",EDGE,"E23"),sQuery(id+"F2.wireOp",EDGE,"E24.filletArc"),sQuery(id+"F2.wireOp",EDGE,"E25"),sQuery(id+"F2.wireOp",EDGE,"E26"),sQuery(id+"F2.wireOp",EDGE,"E27.filletArc"),sQuery(id+"F2.wireOp",EDGE,"E28"),sQuery(id+"F2.wireOp",EDGE,"E29"),sQuery(id+"F2.wireOp",EDGE,"E30"),sQuery(id+"F2.wireOp",EDGE,"E31"),sQuery(id+"F2.wireOp",EDGE,"E32"),sQuery(id+"F2.wireOp",EDGE,"E33"),sQuery(id+"F2.wireOp",EDGE,"E34"),sQuery(id+"F2.wireOp",EDGE,"E35"),sQuery(id+"F2.wireOp",EDGE,"E36"),sQuery(id+"F2.wireOp",EDGE,"E37"),sQuery(id+"F2.wireOp",EDGE,"E38"),sQuery(id+"F2.wireOp",EDGE,"E39.filletArc"),sQuery(id+"F2.wireOp",EDGE,"E40.filletArc"),sQuery(id+"F2.wireOp",EDGE,"E41.filletArc"),sQuery(id+"F2.wireOp",EDGE,"E42.filletArc")])],"isStart":true}),makeQuery(id+"F6.opExtrude","CAP_FACE",FACE,{"disambiguationData":[OSD([sQuery(id+"F4.wireOp",EDGE,"E43"),sQuery(id+"F4.wireOp",EDGE,"E44.0"),sQuery(id+"F4.wireOp",EDGE,"E44.1"),sQuery(id+"F4.wireOp",EDGE,"E44.2"),sQuery(id+"F4.wireOp",EDGE,"E44.3"),sQuery(id+"F4.wireOp",EDGE,"E44.4"),sQuery(id+"F4.wireOp",EDGE,"E44.5")])],"isStart":false})]})]});}
            var Q31;
            {var subQ0=sQuery(id+"F2.wireOp",EDGE,"E16");Q31=makeQuery(id+"Fk14XMOrtsRoLGN_1.opChamfer","BLEND_EDGE",EDGE,{"blendedFrom":[makeQuery(id+"F7.opBoolean","INTERSECT",EDGE,{"derivedFrom":[makeQuery(id+"F1.opRevolve","SWEPT_FACE",FACE,{"disambiguationData":[OSD([sQuery(id+"F0.wireOp",EDGE,"E5"),sQuery(id+"F0.wireOp",EDGE,"E6")])]}),makeQuery(id+"F3.opExtrude","SWEPT_FACE",FACE,{"disambiguationData":[OSD([subQ0])]})]}),makeQuery(id+"F7.opBoolean","MERGE",FACE,{"derivedFrom":[makeQuery(id+"F3.opExtrude","CAP_FACE",FACE,{"disambiguationData":[OSD([sQuery(id+"F2.wireOp",EDGE,"E10.0"),sQuery(id+"F2.wireOp",EDGE,"E10.1"),sQuery(id+"F2.wireOp",EDGE,"E10.2"),sQuery(id+"F2.wireOp",EDGE,"E10.3"),sQuery(id+"F2.wireOp",EDGE,"E10.4"),sQuery(id+"F2.wireOp",EDGE,"E10.5")])],"isStart":true}),makeQuery(id+"F3.opExtrude","CAP_FACE",FACE,{"disambiguationData":[OSD([sQuery(id+"F2.wireOp",EDGE,"E11"),sQuery(id+"F2.wireOp",EDGE,"E12"),sQuery(id+"F2.wireOp",EDGE,"E13"),sQuery(id+"F2.wireOp",EDGE,"E14"),sQuery(id+"F2.wireOp",EDGE,"E15"),subQ0,sQuery(id+"F2.wireOp",EDGE,"E17"),sQuery(id+"F2.wireOp",EDGE,"E18"),sQuery(id+"F2.wireOp",EDGE,"E19"),sQuery(id+"F2.wireOp",EDGE,"E20"),sQuery(id+"F2.wireOp",EDGE,"E21"),sQuery(id+"F2.wireOp",EDGE,"E22"),sQuery(id+"F2.wireOp",EDGE,"E23"),sQuery(id+"F2.wireOp",EDGE,"E24.filletArc"),sQuery(id+"F2.wireOp",EDGE,"E25"),sQuery(id+"F2.wireOp",EDGE,"E26"),sQuery(id+"F2.wireOp",EDGE,"E27.filletArc"),sQuery(id+"F2.wireOp",EDGE,"E28"),sQuery(id+"F2.wireOp",EDGE,"E29"),sQuery(id+"F2.wireOp",EDGE,"E30"),sQuery(id+"F2.wireOp",EDGE,"E31"),sQuery(id+"F2.wireOp",EDGE,"E32"),sQuery(id+"F2.wireOp",EDGE,"E33"),sQuery(id+"F2.wireOp",EDGE,"E34"),sQuery(id+"F2.wireOp",EDGE,"E35"),sQuery(id+"F2.wireOp",EDGE,"E36"),sQuery(id+"F2.wireOp",EDGE,"E37"),sQuery(id+"F2.wireOp",EDGE,"E38"),sQuery(id+"F2.wireOp",EDGE,"E39.filletArc"),sQuery(id+"F2.wireOp",EDGE,"E40.filletArc"),sQuery(id+"F2.wireOp",EDGE,"E41.filletArc"),sQuery(id+"F2.wireOp",EDGE,"E42.filletArc")])],"isStart":true}),makeQuery(id+"F6.opExtrude","CAP_FACE",FACE,{"disambiguationData":[OSD([sQuery(id+"F4.wireOp",EDGE,"E43"),sQuery(id+"F4.wireOp",EDGE,"E44.0"),sQuery(id+"F4.wireOp",EDGE,"E44.1"),sQuery(id+"F4.wireOp",EDGE,"E44.2"),sQuery(id+"F4.wireOp",EDGE,"E44.3"),sQuery(id+"F4.wireOp",EDGE,"E44.4"),sQuery(id+"F4.wireOp",EDGE,"E44.5")])],"isStart":false})]})],"blendedInto":[makeQuery(id+"F7.opBoolean","MERGE",FACE,{"derivedFrom":[makeQuery(id+"F3.opExtrude","CAP_FACE",FACE,{"disambiguationData":[OSD([sQuery(id+"F2.wireOp",EDGE,"E10.0"),sQuery(id+"F2.wireOp",EDGE,"E10.1"),sQuery(id+"F2.wireOp",EDGE,"E10.2"),sQuery(id+"F2.wireOp",EDGE,"E10.3"),sQuery(id+"F2.wireOp",EDGE,"E10.4"),sQuery(id+"F2.wireOp",EDGE,"E10.5")])],"isStart":true}),makeQuery(id+"F3.opExtrude","CAP_FACE",FACE,{"disambiguationData":[OSD([sQuery(id+"F2.wireOp",EDGE,"E11"),sQuery(id+"F2.wireOp",EDGE,"E12"),sQuery(id+"F2.wireOp",EDGE,"E13"),sQuery(id+"F2.wireOp",EDGE,"E14"),sQuery(id+"F2.wireOp",EDGE,"E15"),subQ0,sQuery(id+"F2.wireOp",EDGE,"E17"),sQuery(id+"F2.wireOp",EDGE,"E18"),sQuery(id+"F2.wireOp",EDGE,"E19"),sQuery(id+"F2.wireOp",EDGE,"E20"),sQuery(id+"F2.wireOp",EDGE,"E21"),sQuery(id+"F2.wireOp",EDGE,"E22"),sQuery(id+"F2.wireOp",EDGE,"E23"),sQuery(id+"F2.wireOp",EDGE,"E24.filletArc"),sQuery(id+"F2.wireOp",EDGE,"E25"),sQuery(id+"F2.wireOp",EDGE,"E26"),sQuery(id+"F2.wireOp",EDGE,"E27.filletArc"),sQuery(id+"F2.wireOp",EDGE,"E28"),sQuery(id+"F2.wireOp",EDGE,"E29"),sQuery(id+"F2.wireOp",EDGE,"E30"),sQuery(id+"F2.wireOp",EDGE,"E31"),sQuery(id+"F2.wireOp",EDGE,"E32"),sQuery(id+"F2.wireOp",EDGE,"E33"),sQuery(id+"F2.wireOp",EDGE,"E34"),sQuery(id+"F2.wireOp",EDGE,"E35"),sQuery(id+"F2.wireOp",EDGE,"E36"),sQuery(id+"F2.wireOp",EDGE,"E37"),sQuery(id+"F2.wireOp",EDGE,"E38"),sQuery(id+"F2.wireOp",EDGE,"E39.filletArc"),sQuery(id+"F2.wireOp",EDGE,"E40.filletArc"),sQuery(id+"F2.wireOp",EDGE,"E41.filletArc"),sQuery(id+"F2.wireOp",EDGE,"E42.filletArc")])],"isStart":true}),makeQuery(id+"F6.opExtrude","CAP_FACE",FACE,{"disambiguationData":[OSD([sQuery(id+"F4.wireOp",EDGE,"E43"),sQuery(id+"F4.wireOp",EDGE,"E44.0"),sQuery(id+"F4.wireOp",EDGE,"E44.1"),sQuery(id+"F4.wireOp",EDGE,"E44.2"),sQuery(id+"F4.wireOp",EDGE,"E44.3"),sQuery(id+"F4.wireOp",EDGE,"E44.4"),sQuery(id+"F4.wireOp",EDGE,"E44.5")])],"isStart":false})]})]});}
            var Q32;
            {var subQ0=sQuery(id+"F2.wireOp",EDGE,"E21");Q32=makeQuery(id+"Fk14XMOrtsRoLGN_1.opChamfer","BLEND_EDGE",EDGE,{"blendedFrom":[makeQuery(id+"F7.opBoolean","INTERSECT",EDGE,{"derivedFrom":[makeQuery(id+"F1.opRevolve","SWEPT_FACE",FACE,{"disambiguationData":[OSD([sQuery(id+"F0.wireOp",EDGE,"E5"),sQuery(id+"F0.wireOp",EDGE,"E6")])]}),makeQuery(id+"F3.opExtrude","SWEPT_FACE",FACE,{"disambiguationData":[OSD([subQ0])]})]}),makeQuery(id+"F7.opBoolean","MERGE",FACE,{"derivedFrom":[makeQuery(id+"F3.opExtrude","CAP_FACE",FACE,{"disambiguationData":[OSD([sQuery(id+"F2.wireOp",EDGE,"E10.0"),sQuery(id+"F2.wireOp",EDGE,"E10.1"),sQuery(id+"F2.wireOp",EDGE,"E10.2"),sQuery(id+"F2.wireOp",EDGE,"E10.3"),sQuery(id+"F2.wireOp",EDGE,"E10.4"),sQuery(id+"F2.wireOp",EDGE,"E10.5")])],"isStart":true}),makeQuery(id+"F3.opExtrude","CAP_FACE",FACE,{"disambiguationData":[OSD([sQuery(id+"F2.wireOp",EDGE,"E11"),sQuery(id+"F2.wireOp",EDGE,"E12"),sQuery(id+"F2.wireOp",EDGE,"E13"),sQuery(id+"F2.wireOp",EDGE,"E14"),sQuery(id+"F2.wireOp",EDGE,"E15"),sQuery(id+"F2.wireOp",EDGE,"E16"),sQuery(id+"F2.wireOp",EDGE,"E17"),sQuery(id+"F2.wireOp",EDGE,"E18"),sQuery(id+"F2.wireOp",EDGE,"E19"),sQuery(id+"F2.wireOp",EDGE,"E20"),subQ0,sQuery(id+"F2.wireOp",EDGE,"E22"),sQuery(id+"F2.wireOp",EDGE,"E23"),sQuery(id+"F2.wireOp",EDGE,"E24.filletArc"),sQuery(id+"F2.wireOp",EDGE,"E25"),sQuery(id+"F2.wireOp",EDGE,"E26"),sQuery(id+"F2.wireOp",EDGE,"E27.filletArc"),sQuery(id+"F2.wireOp",EDGE,"E28"),sQuery(id+"F2.wireOp",EDGE,"E29"),sQuery(id+"F2.wireOp",EDGE,"E30"),sQuery(id+"F2.wireOp",EDGE,"E31"),sQuery(id+"F2.wireOp",EDGE,"E32"),sQuery(id+"F2.wireOp",EDGE,"E33"),sQuery(id+"F2.wireOp",EDGE,"E34"),sQuery(id+"F2.wireOp",EDGE,"E35"),sQuery(id+"F2.wireOp",EDGE,"E36"),sQuery(id+"F2.wireOp",EDGE,"E37"),sQuery(id+"F2.wireOp",EDGE,"E38"),sQuery(id+"F2.wireOp",EDGE,"E39.filletArc"),sQuery(id+"F2.wireOp",EDGE,"E40.filletArc"),sQuery(id+"F2.wireOp",EDGE,"E41.filletArc"),sQuery(id+"F2.wireOp",EDGE,"E42.filletArc")])],"isStart":true}),makeQuery(id+"F6.opExtrude","CAP_FACE",FACE,{"disambiguationData":[OSD([sQuery(id+"F4.wireOp",EDGE,"E43"),sQuery(id+"F4.wireOp",EDGE,"E44.0"),sQuery(id+"F4.wireOp",EDGE,"E44.1"),sQuery(id+"F4.wireOp",EDGE,"E44.2"),sQuery(id+"F4.wireOp",EDGE,"E44.3"),sQuery(id+"F4.wireOp",EDGE,"E44.4"),sQuery(id+"F4.wireOp",EDGE,"E44.5")])],"isStart":false})]})],"blendedInto":[makeQuery(id+"F7.opBoolean","MERGE",FACE,{"derivedFrom":[makeQuery(id+"F3.opExtrude","CAP_FACE",FACE,{"disambiguationData":[OSD([sQuery(id+"F2.wireOp",EDGE,"E10.0"),sQuery(id+"F2.wireOp",EDGE,"E10.1"),sQuery(id+"F2.wireOp",EDGE,"E10.2"),sQuery(id+"F2.wireOp",EDGE,"E10.3"),sQuery(id+"F2.wireOp",EDGE,"E10.4"),sQuery(id+"F2.wireOp",EDGE,"E10.5")])],"isStart":true}),makeQuery(id+"F3.opExtrude","CAP_FACE",FACE,{"disambiguationData":[OSD([sQuery(id+"F2.wireOp",EDGE,"E11"),sQuery(id+"F2.wireOp",EDGE,"E12"),sQuery(id+"F2.wireOp",EDGE,"E13"),sQuery(id+"F2.wireOp",EDGE,"E14"),sQuery(id+"F2.wireOp",EDGE,"E15"),sQuery(id+"F2.wireOp",EDGE,"E16"),sQuery(id+"F2.wireOp",EDGE,"E17"),sQuery(id+"F2.wireOp",EDGE,"E18"),sQuery(id+"F2.wireOp",EDGE,"E19"),sQuery(id+"F2.wireOp",EDGE,"E20"),subQ0,sQuery(id+"F2.wireOp",EDGE,"E22"),sQuery(id+"F2.wireOp",EDGE,"E23"),sQuery(id+"F2.wireOp",EDGE,"E24.filletArc"),sQuery(id+"F2.wireOp",EDGE,"E25"),sQuery(id+"F2.wireOp",EDGE,"E26"),sQuery(id+"F2.wireOp",EDGE,"E27.filletArc"),sQuery(id+"F2.wireOp",EDGE,"E28"),sQuery(id+"F2.wireOp",EDGE,"E29"),sQuery(id+"F2.wireOp",EDGE,"E30"),sQuery(id+"F2.wireOp",EDGE,"E31"),sQuery(id+"F2.wireOp",EDGE,"E32"),sQuery(id+"F2.wireOp",EDGE,"E33"),sQuery(id+"F2.wireOp",EDGE,"E34"),sQuery(id+"F2.wireOp",EDGE,"E35"),sQuery(id+"F2.wireOp",EDGE,"E36"),sQuery(id+"F2.wireOp",EDGE,"E37"),sQuery(id+"F2.wireOp",EDGE,"E38"),sQuery(id+"F2.wireOp",EDGE,"E39.filletArc"),sQuery(id+"F2.wireOp",EDGE,"E40.filletArc"),sQuery(id+"F2.wireOp",EDGE,"E41.filletArc"),sQuery(id+"F2.wireOp",EDGE,"E42.filletArc")])],"isStart":true}),makeQuery(id+"F6.opExtrude","CAP_FACE",FACE,{"disambiguationData":[OSD([sQuery(id+"F4.wireOp",EDGE,"E43"),sQuery(id+"F4.wireOp",EDGE,"E44.0"),sQuery(id+"F4.wireOp",EDGE,"E44.1"),sQuery(id+"F4.wireOp",EDGE,"E44.2"),sQuery(id+"F4.wireOp",EDGE,"E44.3"),sQuery(id+"F4.wireOp",EDGE,"E44.4"),sQuery(id+"F4.wireOp",EDGE,"E44.5")])],"isStart":false})]})]});}
            var Q33;
            {var subQ0=sQuery(id+"F2.wireOp",EDGE,"E15");Q33=makeQuery(id+"Fk14XMOrtsRoLGN_1.opChamfer","BLEND_EDGE",EDGE,{"blendedFrom":[makeQuery(id+"F7.opBoolean","INTERSECT",EDGE,{"derivedFrom":[makeQuery(id+"F1.opRevolve","SWEPT_FACE",FACE,{"disambiguationData":[OSD([sQuery(id+"F0.wireOp",EDGE,"E5"),sQuery(id+"F0.wireOp",EDGE,"E6")])]}),makeQuery(id+"F3.opExtrude","SWEPT_FACE",FACE,{"disambiguationData":[OSD([subQ0])]})]}),makeQuery(id+"F7.opBoolean","MERGE",FACE,{"derivedFrom":[makeQuery(id+"F3.opExtrude","CAP_FACE",FACE,{"disambiguationData":[OSD([sQuery(id+"F2.wireOp",EDGE,"E10.0"),sQuery(id+"F2.wireOp",EDGE,"E10.1"),sQuery(id+"F2.wireOp",EDGE,"E10.2"),sQuery(id+"F2.wireOp",EDGE,"E10.3"),sQuery(id+"F2.wireOp",EDGE,"E10.4"),sQuery(id+"F2.wireOp",EDGE,"E10.5")])],"isStart":true}),makeQuery(id+"F3.opExtrude","CAP_FACE",FACE,{"disambiguationData":[OSD([sQuery(id+"F2.wireOp",EDGE,"E11"),sQuery(id+"F2.wireOp",EDGE,"E12"),sQuery(id+"F2.wireOp",EDGE,"E13"),sQuery(id+"F2.wireOp",EDGE,"E14"),subQ0,sQuery(id+"F2.wireOp",EDGE,"E16"),sQuery(id+"F2.wireOp",EDGE,"E17"),sQuery(id+"F2.wireOp",EDGE,"E18"),sQuery(id+"F2.wireOp",EDGE,"E19"),sQuery(id+"F2.wireOp",EDGE,"E20"),sQuery(id+"F2.wireOp",EDGE,"E21"),sQuery(id+"F2.wireOp",EDGE,"E22"),sQuery(id+"F2.wireOp",EDGE,"E23"),sQuery(id+"F2.wireOp",EDGE,"E24.filletArc"),sQuery(id+"F2.wireOp",EDGE,"E25"),sQuery(id+"F2.wireOp",EDGE,"E26"),sQuery(id+"F2.wireOp",EDGE,"E27.filletArc"),sQuery(id+"F2.wireOp",EDGE,"E28"),sQuery(id+"F2.wireOp",EDGE,"E29"),sQuery(id+"F2.wireOp",EDGE,"E30"),sQuery(id+"F2.wireOp",EDGE,"E31"),sQuery(id+"F2.wireOp",EDGE,"E32"),sQuery(id+"F2.wireOp",EDGE,"E33"),sQuery(id+"F2.wireOp",EDGE,"E34"),sQuery(id+"F2.wireOp",EDGE,"E35"),sQuery(id+"F2.wireOp",EDGE,"E36"),sQuery(id+"F2.wireOp",EDGE,"E37"),sQuery(id+"F2.wireOp",EDGE,"E38"),sQuery(id+"F2.wireOp",EDGE,"E39.filletArc"),sQuery(id+"F2.wireOp",EDGE,"E40.filletArc"),sQuery(id+"F2.wireOp",EDGE,"E41.filletArc"),sQuery(id+"F2.wireOp",EDGE,"E42.filletArc")])],"isStart":true}),makeQuery(id+"F6.opExtrude","CAP_FACE",FACE,{"disambiguationData":[OSD([sQuery(id+"F4.wireOp",EDGE,"E43"),sQuery(id+"F4.wireOp",EDGE,"E44.0"),sQuery(id+"F4.wireOp",EDGE,"E44.1"),sQuery(id+"F4.wireOp",EDGE,"E44.2"),sQuery(id+"F4.wireOp",EDGE,"E44.3"),sQuery(id+"F4.wireOp",EDGE,"E44.4"),sQuery(id+"F4.wireOp",EDGE,"E44.5")])],"isStart":false})]})],"blendedInto":[makeQuery(id+"F7.opBoolean","MERGE",FACE,{"derivedFrom":[makeQuery(id+"F3.opExtrude","CAP_FACE",FACE,{"disambiguationData":[OSD([sQuery(id+"F2.wireOp",EDGE,"E10.0"),sQuery(id+"F2.wireOp",EDGE,"E10.1"),sQuery(id+"F2.wireOp",EDGE,"E10.2"),sQuery(id+"F2.wireOp",EDGE,"E10.3"),sQuery(id+"F2.wireOp",EDGE,"E10.4"),sQuery(id+"F2.wireOp",EDGE,"E10.5")])],"isStart":true}),makeQuery(id+"F3.opExtrude","CAP_FACE",FACE,{"disambiguationData":[OSD([sQuery(id+"F2.wireOp",EDGE,"E11"),sQuery(id+"F2.wireOp",EDGE,"E12"),sQuery(id+"F2.wireOp",EDGE,"E13"),sQuery(id+"F2.wireOp",EDGE,"E14"),subQ0,sQuery(id+"F2.wireOp",EDGE,"E16"),sQuery(id+"F2.wireOp",EDGE,"E17"),sQuery(id+"F2.wireOp",EDGE,"E18"),sQuery(id+"F2.wireOp",EDGE,"E19"),sQuery(id+"F2.wireOp",EDGE,"E20"),sQuery(id+"F2.wireOp",EDGE,"E21"),sQuery(id+"F2.wireOp",EDGE,"E22"),sQuery(id+"F2.wireOp",EDGE,"E23"),sQuery(id+"F2.wireOp",EDGE,"E24.filletArc"),sQuery(id+"F2.wireOp",EDGE,"E25"),sQuery(id+"F2.wireOp",EDGE,"E26"),sQuery(id+"F2.wireOp",EDGE,"E27.filletArc"),sQuery(id+"F2.wireOp",EDGE,"E28"),sQuery(id+"F2.wireOp",EDGE,"E29"),sQuery(id+"F2.wireOp",EDGE,"E30"),sQuery(id+"F2.wireOp",EDGE,"E31"),sQuery(id+"F2.wireOp",EDGE,"E32"),sQuery(id+"F2.wireOp",EDGE,"E33"),sQuery(id+"F2.wireOp",EDGE,"E34"),sQuery(id+"F2.wireOp",EDGE,"E35"),sQuery(id+"F2.wireOp",EDGE,"E36"),sQuery(id+"F2.wireOp",EDGE,"E37"),sQuery(id+"F2.wireOp",EDGE,"E38"),sQuery(id+"F2.wireOp",EDGE,"E39.filletArc"),sQuery(id+"F2.wireOp",EDGE,"E40.filletArc"),sQuery(id+"F2.wireOp",EDGE,"E41.filletArc"),sQuery(id+"F2.wireOp",EDGE,"E42.filletArc")])],"isStart":true}),makeQuery(id+"F6.opExtrude","CAP_FACE",FACE,{"disambiguationData":[OSD([sQuery(id+"F4.wireOp",EDGE,"E43"),sQuery(id+"F4.wireOp",EDGE,"E44.0"),sQuery(id+"F4.wireOp",EDGE,"E44.1"),sQuery(id+"F4.wireOp",EDGE,"E44.2"),sQuery(id+"F4.wireOp",EDGE,"E44.3"),sQuery(id+"F4.wireOp",EDGE,"E44.4"),sQuery(id+"F4.wireOp",EDGE,"E44.5")])],"isStart":false})]})]});}
            var Q34;
            {var subQ0=sQuery(id+"F2.wireOp",EDGE,"E34");Q34=makeQuery(id+"Fk14XMOrtsRoLGN_1.opChamfer","BLEND_EDGE",EDGE,{"blendedFrom":[makeQuery(id+"F7.opBoolean","INTERSECT",EDGE,{"derivedFrom":[makeQuery(id+"F1.opRevolve","SWEPT_FACE",FACE,{"disambiguationData":[OSD([sQuery(id+"F0.wireOp",EDGE,"E5"),sQuery(id+"F0.wireOp",EDGE,"E6")])]}),makeQuery(id+"F3.opExtrude","SWEPT_FACE",FACE,{"disambiguationData":[OSD([subQ0])]})]}),makeQuery(id+"F7.opBoolean","MERGE",FACE,{"derivedFrom":[makeQuery(id+"F3.opExtrude","CAP_FACE",FACE,{"disambiguationData":[OSD([sQuery(id+"F2.wireOp",EDGE,"E10.0"),sQuery(id+"F2.wireOp",EDGE,"E10.1"),sQuery(id+"F2.wireOp",EDGE,"E10.2"),sQuery(id+"F2.wireOp",EDGE,"E10.3"),sQuery(id+"F2.wireOp",EDGE,"E10.4"),sQuery(id+"F2.wireOp",EDGE,"E10.5")])],"isStart":true}),makeQuery(id+"F3.opExtrude","CAP_FACE",FACE,{"disambiguationData":[OSD([sQuery(id+"F2.wireOp",EDGE,"E11"),sQuery(id+"F2.wireOp",EDGE,"E12"),sQuery(id+"F2.wireOp",EDGE,"E13"),sQuery(id+"F2.wireOp",EDGE,"E14"),sQuery(id+"F2.wireOp",EDGE,"E15"),sQuery(id+"F2.wireOp",EDGE,"E16"),sQuery(id+"F2.wireOp",EDGE,"E17"),sQuery(id+"F2.wireOp",EDGE,"E18"),sQuery(id+"F2.wireOp",EDGE,"E19"),sQuery(id+"F2.wireOp",EDGE,"E20"),sQuery(id+"F2.wireOp",EDGE,"E21"),sQuery(id+"F2.wireOp",EDGE,"E22"),sQuery(id+"F2.wireOp",EDGE,"E23"),sQuery(id+"F2.wireOp",EDGE,"E24.filletArc"),sQuery(id+"F2.wireOp",EDGE,"E25"),sQuery(id+"F2.wireOp",EDGE,"E26"),sQuery(id+"F2.wireOp",EDGE,"E27.filletArc"),sQuery(id+"F2.wireOp",EDGE,"E28"),sQuery(id+"F2.wireOp",EDGE,"E29"),sQuery(id+"F2.wireOp",EDGE,"E30"),sQuery(id+"F2.wireOp",EDGE,"E31"),sQuery(id+"F2.wireOp",EDGE,"E32"),sQuery(id+"F2.wireOp",EDGE,"E33"),subQ0,sQuery(id+"F2.wireOp",EDGE,"E35"),sQuery(id+"F2.wireOp",EDGE,"E36"),sQuery(id+"F2.wireOp",EDGE,"E37"),sQuery(id+"F2.wireOp",EDGE,"E38"),sQuery(id+"F2.wireOp",EDGE,"E39.filletArc"),sQuery(id+"F2.wireOp",EDGE,"E40.filletArc"),sQuery(id+"F2.wireOp",EDGE,"E41.filletArc"),sQuery(id+"F2.wireOp",EDGE,"E42.filletArc")])],"isStart":true}),makeQuery(id+"F6.opExtrude","CAP_FACE",FACE,{"disambiguationData":[OSD([sQuery(id+"F4.wireOp",EDGE,"E43"),sQuery(id+"F4.wireOp",EDGE,"E44.0"),sQuery(id+"F4.wireOp",EDGE,"E44.1"),sQuery(id+"F4.wireOp",EDGE,"E44.2"),sQuery(id+"F4.wireOp",EDGE,"E44.3"),sQuery(id+"F4.wireOp",EDGE,"E44.4"),sQuery(id+"F4.wireOp",EDGE,"E44.5")])],"isStart":false})]})],"blendedInto":[makeQuery(id+"F7.opBoolean","MERGE",FACE,{"derivedFrom":[makeQuery(id+"F3.opExtrude","CAP_FACE",FACE,{"disambiguationData":[OSD([sQuery(id+"F2.wireOp",EDGE,"E10.0"),sQuery(id+"F2.wireOp",EDGE,"E10.1"),sQuery(id+"F2.wireOp",EDGE,"E10.2"),sQuery(id+"F2.wireOp",EDGE,"E10.3"),sQuery(id+"F2.wireOp",EDGE,"E10.4"),sQuery(id+"F2.wireOp",EDGE,"E10.5")])],"isStart":true}),makeQuery(id+"F3.opExtrude","CAP_FACE",FACE,{"disambiguationData":[OSD([sQuery(id+"F2.wireOp",EDGE,"E11"),sQuery(id+"F2.wireOp",EDGE,"E12"),sQuery(id+"F2.wireOp",EDGE,"E13"),sQuery(id+"F2.wireOp",EDGE,"E14"),sQuery(id+"F2.wireOp",EDGE,"E15"),sQuery(id+"F2.wireOp",EDGE,"E16"),sQuery(id+"F2.wireOp",EDGE,"E17"),sQuery(id+"F2.wireOp",EDGE,"E18"),sQuery(id+"F2.wireOp",EDGE,"E19"),sQuery(id+"F2.wireOp",EDGE,"E20"),sQuery(id+"F2.wireOp",EDGE,"E21"),sQuery(id+"F2.wireOp",EDGE,"E22"),sQuery(id+"F2.wireOp",EDGE,"E23"),sQuery(id+"F2.wireOp",EDGE,"E24.filletArc"),sQuery(id+"F2.wireOp",EDGE,"E25"),sQuery(id+"F2.wireOp",EDGE,"E26"),sQuery(id+"F2.wireOp",EDGE,"E27.filletArc"),sQuery(id+"F2.wireOp",EDGE,"E28"),sQuery(id+"F2.wireOp",EDGE,"E29"),sQuery(id+"F2.wireOp",EDGE,"E30"),sQuery(id+"F2.wireOp",EDGE,"E31"),sQuery(id+"F2.wireOp",EDGE,"E32"),sQuery(id+"F2.wireOp",EDGE,"E33"),subQ0,sQuery(id+"F2.wireOp",EDGE,"E35"),sQuery(id+"F2.wireOp",EDGE,"E36"),sQuery(id+"F2.wireOp",EDGE,"E37"),sQuery(id+"F2.wireOp",EDGE,"E38"),sQuery(id+"F2.wireOp",EDGE,"E39.filletArc"),sQuery(id+"F2.wireOp",EDGE,"E40.filletArc"),sQuery(id+"F2.wireOp",EDGE,"E41.filletArc"),sQuery(id+"F2.wireOp",EDGE,"E42.filletArc")])],"isStart":true}),makeQuery(id+"F6.opExtrude","CAP_FACE",FACE,{"disambiguationData":[OSD([sQuery(id+"F4.wireOp",EDGE,"E43"),sQuery(id+"F4.wireOp",EDGE,"E44.0"),sQuery(id+"F4.wireOp",EDGE,"E44.1"),sQuery(id+"F4.wireOp",EDGE,"E44.2"),sQuery(id+"F4.wireOp",EDGE,"E44.3"),sQuery(id+"F4.wireOp",EDGE,"E44.4"),sQuery(id+"F4.wireOp",EDGE,"E44.5")])],"isStart":false})]})]});}
            var Q35;
            {var subQ0=sQuery(id+"F2.wireOp",EDGE,"E35");Q35=makeQuery(id+"Fk14XMOrtsRoLGN_1.opChamfer","BLEND_EDGE",EDGE,{"blendedFrom":[makeQuery(id+"F7.opBoolean","INTERSECT",EDGE,{"derivedFrom":[makeQuery(id+"F1.opRevolve","SWEPT_FACE",FACE,{"disambiguationData":[OSD([sQuery(id+"F0.wireOp",EDGE,"E5"),sQuery(id+"F0.wireOp",EDGE,"E6")])]}),makeQuery(id+"F3.opExtrude","SWEPT_FACE",FACE,{"disambiguationData":[OSD([subQ0])]})]}),makeQuery(id+"F7.opBoolean","MERGE",FACE,{"derivedFrom":[makeQuery(id+"F3.opExtrude","CAP_FACE",FACE,{"disambiguationData":[OSD([sQuery(id+"F2.wireOp",EDGE,"E10.0"),sQuery(id+"F2.wireOp",EDGE,"E10.1"),sQuery(id+"F2.wireOp",EDGE,"E10.2"),sQuery(id+"F2.wireOp",EDGE,"E10.3"),sQuery(id+"F2.wireOp",EDGE,"E10.4"),sQuery(id+"F2.wireOp",EDGE,"E10.5")])],"isStart":true}),makeQuery(id+"F3.opExtrude","CAP_FACE",FACE,{"disambiguationData":[OSD([sQuery(id+"F2.wireOp",EDGE,"E11"),sQuery(id+"F2.wireOp",EDGE,"E12"),sQuery(id+"F2.wireOp",EDGE,"E13"),sQuery(id+"F2.wireOp",EDGE,"E14"),sQuery(id+"F2.wireOp",EDGE,"E15"),sQuery(id+"F2.wireOp",EDGE,"E16"),sQuery(id+"F2.wireOp",EDGE,"E17"),sQuery(id+"F2.wireOp",EDGE,"E18"),sQuery(id+"F2.wireOp",EDGE,"E19"),sQuery(id+"F2.wireOp",EDGE,"E20"),sQuery(id+"F2.wireOp",EDGE,"E21"),sQuery(id+"F2.wireOp",EDGE,"E22"),sQuery(id+"F2.wireOp",EDGE,"E23"),sQuery(id+"F2.wireOp",EDGE,"E24.filletArc"),sQuery(id+"F2.wireOp",EDGE,"E25"),sQuery(id+"F2.wireOp",EDGE,"E26"),sQuery(id+"F2.wireOp",EDGE,"E27.filletArc"),sQuery(id+"F2.wireOp",EDGE,"E28"),sQuery(id+"F2.wireOp",EDGE,"E29"),sQuery(id+"F2.wireOp",EDGE,"E30"),sQuery(id+"F2.wireOp",EDGE,"E31"),sQuery(id+"F2.wireOp",EDGE,"E32"),sQuery(id+"F2.wireOp",EDGE,"E33"),sQuery(id+"F2.wireOp",EDGE,"E34"),subQ0,sQuery(id+"F2.wireOp",EDGE,"E36"),sQuery(id+"F2.wireOp",EDGE,"E37"),sQuery(id+"F2.wireOp",EDGE,"E38"),sQuery(id+"F2.wireOp",EDGE,"E39.filletArc"),sQuery(id+"F2.wireOp",EDGE,"E40.filletArc"),sQuery(id+"F2.wireOp",EDGE,"E41.filletArc"),sQuery(id+"F2.wireOp",EDGE,"E42.filletArc")])],"isStart":true}),makeQuery(id+"F6.opExtrude","CAP_FACE",FACE,{"disambiguationData":[OSD([sQuery(id+"F4.wireOp",EDGE,"E43"),sQuery(id+"F4.wireOp",EDGE,"E44.0"),sQuery(id+"F4.wireOp",EDGE,"E44.1"),sQuery(id+"F4.wireOp",EDGE,"E44.2"),sQuery(id+"F4.wireOp",EDGE,"E44.3"),sQuery(id+"F4.wireOp",EDGE,"E44.4"),sQuery(id+"F4.wireOp",EDGE,"E44.5")])],"isStart":false})]})],"blendedInto":[makeQuery(id+"F7.opBoolean","MERGE",FACE,{"derivedFrom":[makeQuery(id+"F3.opExtrude","CAP_FACE",FACE,{"disambiguationData":[OSD([sQuery(id+"F2.wireOp",EDGE,"E10.0"),sQuery(id+"F2.wireOp",EDGE,"E10.1"),sQuery(id+"F2.wireOp",EDGE,"E10.2"),sQuery(id+"F2.wireOp",EDGE,"E10.3"),sQuery(id+"F2.wireOp",EDGE,"E10.4"),sQuery(id+"F2.wireOp",EDGE,"E10.5")])],"isStart":true}),makeQuery(id+"F3.opExtrude","CAP_FACE",FACE,{"disambiguationData":[OSD([sQuery(id+"F2.wireOp",EDGE,"E11"),sQuery(id+"F2.wireOp",EDGE,"E12"),sQuery(id+"F2.wireOp",EDGE,"E13"),sQuery(id+"F2.wireOp",EDGE,"E14"),sQuery(id+"F2.wireOp",EDGE,"E15"),sQuery(id+"F2.wireOp",EDGE,"E16"),sQuery(id+"F2.wireOp",EDGE,"E17"),sQuery(id+"F2.wireOp",EDGE,"E18"),sQuery(id+"F2.wireOp",EDGE,"E19"),sQuery(id+"F2.wireOp",EDGE,"E20"),sQuery(id+"F2.wireOp",EDGE,"E21"),sQuery(id+"F2.wireOp",EDGE,"E22"),sQuery(id+"F2.wireOp",EDGE,"E23"),sQuery(id+"F2.wireOp",EDGE,"E24.filletArc"),sQuery(id+"F2.wireOp",EDGE,"E25"),sQuery(id+"F2.wireOp",EDGE,"E26"),sQuery(id+"F2.wireOp",EDGE,"E27.filletArc"),sQuery(id+"F2.wireOp",EDGE,"E28"),sQuery(id+"F2.wireOp",EDGE,"E29"),sQuery(id+"F2.wireOp",EDGE,"E30"),sQuery(id+"F2.wireOp",EDGE,"E31"),sQuery(id+"F2.wireOp",EDGE,"E32"),sQuery(id+"F2.wireOp",EDGE,"E33"),sQuery(id+"F2.wireOp",EDGE,"E34"),subQ0,sQuery(id+"F2.wireOp",EDGE,"E36"),sQuery(id+"F2.wireOp",EDGE,"E37"),sQuery(id+"F2.wireOp",EDGE,"E38"),sQuery(id+"F2.wireOp",EDGE,"E39.filletArc"),sQuery(id+"F2.wireOp",EDGE,"E40.filletArc"),sQuery(id+"F2.wireOp",EDGE,"E41.filletArc"),sQuery(id+"F2.wireOp",EDGE,"E42.filletArc")])],"isStart":true}),makeQuery(id+"F6.opExtrude","CAP_FACE",FACE,{"disambiguationData":[OSD([sQuery(id+"F4.wireOp",EDGE,"E43"),sQuery(id+"F4.wireOp",EDGE,"E44.0"),sQuery(id+"F4.wireOp",EDGE,"E44.1"),sQuery(id+"F4.wireOp",EDGE,"E44.2"),sQuery(id+"F4.wireOp",EDGE,"E44.3"),sQuery(id+"F4.wireOp",EDGE,"E44.4"),sQuery(id+"F4.wireOp",EDGE,"E44.5")])],"isStart":false})]})]});}
            var Q36;
            {var subQ0=sQuery(id+"F2.wireOp",EDGE,"E29");Q36=makeQuery(id+"Fk14XMOrtsRoLGN_1.opChamfer","BLEND_EDGE",EDGE,{"blendedFrom":[makeQuery(id+"F7.opBoolean","INTERSECT",EDGE,{"derivedFrom":[makeQuery(id+"F1.opRevolve","SWEPT_FACE",FACE,{"disambiguationData":[OSD([sQuery(id+"F0.wireOp",EDGE,"E5"),sQuery(id+"F0.wireOp",EDGE,"E6")])]}),makeQuery(id+"F3.opExtrude","SWEPT_FACE",FACE,{"disambiguationData":[OSD([subQ0])]})]}),makeQuery(id+"F7.opBoolean","MERGE",FACE,{"derivedFrom":[makeQuery(id+"F3.opExtrude","CAP_FACE",FACE,{"disambiguationData":[OSD([sQuery(id+"F2.wireOp",EDGE,"E10.0"),sQuery(id+"F2.wireOp",EDGE,"E10.1"),sQuery(id+"F2.wireOp",EDGE,"E10.2"),sQuery(id+"F2.wireOp",EDGE,"E10.3"),sQuery(id+"F2.wireOp",EDGE,"E10.4"),sQuery(id+"F2.wireOp",EDGE,"E10.5")])],"isStart":true}),makeQuery(id+"F3.opExtrude","CAP_FACE",FACE,{"disambiguationData":[OSD([sQuery(id+"F2.wireOp",EDGE,"E11"),sQuery(id+"F2.wireOp",EDGE,"E12"),sQuery(id+"F2.wireOp",EDGE,"E13"),sQuery(id+"F2.wireOp",EDGE,"E14"),sQuery(id+"F2.wireOp",EDGE,"E15"),sQuery(id+"F2.wireOp",EDGE,"E16"),sQuery(id+"F2.wireOp",EDGE,"E17"),sQuery(id+"F2.wireOp",EDGE,"E18"),sQuery(id+"F2.wireOp",EDGE,"E19"),sQuery(id+"F2.wireOp",EDGE,"E20"),sQuery(id+"F2.wireOp",EDGE,"E21"),sQuery(id+"F2.wireOp",EDGE,"E22"),sQuery(id+"F2.wireOp",EDGE,"E23"),sQuery(id+"F2.wireOp",EDGE,"E24.filletArc"),sQuery(id+"F2.wireOp",EDGE,"E25"),sQuery(id+"F2.wireOp",EDGE,"E26"),sQuery(id+"F2.wireOp",EDGE,"E27.filletArc"),sQuery(id+"F2.wireOp",EDGE,"E28"),subQ0,sQuery(id+"F2.wireOp",EDGE,"E30"),sQuery(id+"F2.wireOp",EDGE,"E31"),sQuery(id+"F2.wireOp",EDGE,"E32"),sQuery(id+"F2.wireOp",EDGE,"E33"),sQuery(id+"F2.wireOp",EDGE,"E34"),sQuery(id+"F2.wireOp",EDGE,"E35"),sQuery(id+"F2.wireOp",EDGE,"E36"),sQuery(id+"F2.wireOp",EDGE,"E37"),sQuery(id+"F2.wireOp",EDGE,"E38"),sQuery(id+"F2.wireOp",EDGE,"E39.filletArc"),sQuery(id+"F2.wireOp",EDGE,"E40.filletArc"),sQuery(id+"F2.wireOp",EDGE,"E41.filletArc"),sQuery(id+"F2.wireOp",EDGE,"E42.filletArc")])],"isStart":true}),makeQuery(id+"F6.opExtrude","CAP_FACE",FACE,{"disambiguationData":[OSD([sQuery(id+"F4.wireOp",EDGE,"E43"),sQuery(id+"F4.wireOp",EDGE,"E44.0"),sQuery(id+"F4.wireOp",EDGE,"E44.1"),sQuery(id+"F4.wireOp",EDGE,"E44.2"),sQuery(id+"F4.wireOp",EDGE,"E44.3"),sQuery(id+"F4.wireOp",EDGE,"E44.4"),sQuery(id+"F4.wireOp",EDGE,"E44.5")])],"isStart":false})]})],"blendedInto":[makeQuery(id+"F7.opBoolean","MERGE",FACE,{"derivedFrom":[makeQuery(id+"F3.opExtrude","CAP_FACE",FACE,{"disambiguationData":[OSD([sQuery(id+"F2.wireOp",EDGE,"E10.0"),sQuery(id+"F2.wireOp",EDGE,"E10.1"),sQuery(id+"F2.wireOp",EDGE,"E10.2"),sQuery(id+"F2.wireOp",EDGE,"E10.3"),sQuery(id+"F2.wireOp",EDGE,"E10.4"),sQuery(id+"F2.wireOp",EDGE,"E10.5")])],"isStart":true}),makeQuery(id+"F3.opExtrude","CAP_FACE",FACE,{"disambiguationData":[OSD([sQuery(id+"F2.wireOp",EDGE,"E11"),sQuery(id+"F2.wireOp",EDGE,"E12"),sQuery(id+"F2.wireOp",EDGE,"E13"),sQuery(id+"F2.wireOp",EDGE,"E14"),sQuery(id+"F2.wireOp",EDGE,"E15"),sQuery(id+"F2.wireOp",EDGE,"E16"),sQuery(id+"F2.wireOp",EDGE,"E17"),sQuery(id+"F2.wireOp",EDGE,"E18"),sQuery(id+"F2.wireOp",EDGE,"E19"),sQuery(id+"F2.wireOp",EDGE,"E20"),sQuery(id+"F2.wireOp",EDGE,"E21"),sQuery(id+"F2.wireOp",EDGE,"E22"),sQuery(id+"F2.wireOp",EDGE,"E23"),sQuery(id+"F2.wireOp",EDGE,"E24.filletArc"),sQuery(id+"F2.wireOp",EDGE,"E25"),sQuery(id+"F2.wireOp",EDGE,"E26"),sQuery(id+"F2.wireOp",EDGE,"E27.filletArc"),sQuery(id+"F2.wireOp",EDGE,"E28"),subQ0,sQuery(id+"F2.wireOp",EDGE,"E30"),sQuery(id+"F2.wireOp",EDGE,"E31"),sQuery(id+"F2.wireOp",EDGE,"E32"),sQuery(id+"F2.wireOp",EDGE,"E33"),sQuery(id+"F2.wireOp",EDGE,"E34"),sQuery(id+"F2.wireOp",EDGE,"E35"),sQuery(id+"F2.wireOp",EDGE,"E36"),sQuery(id+"F2.wireOp",EDGE,"E37"),sQuery(id+"F2.wireOp",EDGE,"E38"),sQuery(id+"F2.wireOp",EDGE,"E39.filletArc"),sQuery(id+"F2.wireOp",EDGE,"E40.filletArc"),sQuery(id+"F2.wireOp",EDGE,"E41.filletArc"),sQuery(id+"F2.wireOp",EDGE,"E42.filletArc")])],"isStart":true}),makeQuery(id+"F6.opExtrude","CAP_FACE",FACE,{"disambiguationData":[OSD([sQuery(id+"F4.wireOp",EDGE,"E43"),sQuery(id+"F4.wireOp",EDGE,"E44.0"),sQuery(id+"F4.wireOp",EDGE,"E44.1"),sQuery(id+"F4.wireOp",EDGE,"E44.2"),sQuery(id+"F4.wireOp",EDGE,"E44.3"),sQuery(id+"F4.wireOp",EDGE,"E44.4"),sQuery(id+"F4.wireOp",EDGE,"E44.5")])],"isStart":false})]})]});}
            var Q37;
            {var subQ0=sQuery(id+"F2.wireOp",EDGE,"E28");Q37=makeQuery(id+"Fk14XMOrtsRoLGN_1.opChamfer","BLEND_EDGE",EDGE,{"blendedFrom":[makeQuery(id+"F7.opBoolean","INTERSECT",EDGE,{"derivedFrom":[makeQuery(id+"F1.opRevolve","SWEPT_FACE",FACE,{"disambiguationData":[OSD([sQuery(id+"F0.wireOp",EDGE,"E5"),sQuery(id+"F0.wireOp",EDGE,"E6")])]}),makeQuery(id+"F3.opExtrude","SWEPT_FACE",FACE,{"disambiguationData":[OSD([subQ0])]})]}),makeQuery(id+"F7.opBoolean","MERGE",FACE,{"derivedFrom":[makeQuery(id+"F3.opExtrude","CAP_FACE",FACE,{"disambiguationData":[OSD([sQuery(id+"F2.wireOp",EDGE,"E10.0"),sQuery(id+"F2.wireOp",EDGE,"E10.1"),sQuery(id+"F2.wireOp",EDGE,"E10.2"),sQuery(id+"F2.wireOp",EDGE,"E10.3"),sQuery(id+"F2.wireOp",EDGE,"E10.4"),sQuery(id+"F2.wireOp",EDGE,"E10.5")])],"isStart":true}),makeQuery(id+"F3.opExtrude","CAP_FACE",FACE,{"disambiguationData":[OSD([sQuery(id+"F2.wireOp",EDGE,"E11"),sQuery(id+"F2.wireOp",EDGE,"E12"),sQuery(id+"F2.wireOp",EDGE,"E13"),sQuery(id+"F2.wireOp",EDGE,"E14"),sQuery(id+"F2.wireOp",EDGE,"E15"),sQuery(id+"F2.wireOp",EDGE,"E16"),sQuery(id+"F2.wireOp",EDGE,"E17"),sQuery(id+"F2.wireOp",EDGE,"E18"),sQuery(id+"F2.wireOp",EDGE,"E19"),sQuery(id+"F2.wireOp",EDGE,"E20"),sQuery(id+"F2.wireOp",EDGE,"E21"),sQuery(id+"F2.wireOp",EDGE,"E22"),sQuery(id+"F2.wireOp",EDGE,"E23"),sQuery(id+"F2.wireOp",EDGE,"E24.filletArc"),sQuery(id+"F2.wireOp",EDGE,"E25"),sQuery(id+"F2.wireOp",EDGE,"E26"),sQuery(id+"F2.wireOp",EDGE,"E27.filletArc"),subQ0,sQuery(id+"F2.wireOp",EDGE,"E29"),sQuery(id+"F2.wireOp",EDGE,"E30"),sQuery(id+"F2.wireOp",EDGE,"E31"),sQuery(id+"F2.wireOp",EDGE,"E32"),sQuery(id+"F2.wireOp",EDGE,"E33"),sQuery(id+"F2.wireOp",EDGE,"E34"),sQuery(id+"F2.wireOp",EDGE,"E35"),sQuery(id+"F2.wireOp",EDGE,"E36"),sQuery(id+"F2.wireOp",EDGE,"E37"),sQuery(id+"F2.wireOp",EDGE,"E38"),sQuery(id+"F2.wireOp",EDGE,"E39.filletArc"),sQuery(id+"F2.wireOp",EDGE,"E40.filletArc"),sQuery(id+"F2.wireOp",EDGE,"E41.filletArc"),sQuery(id+"F2.wireOp",EDGE,"E42.filletArc")])],"isStart":true}),makeQuery(id+"F6.opExtrude","CAP_FACE",FACE,{"disambiguationData":[OSD([sQuery(id+"F4.wireOp",EDGE,"E43"),sQuery(id+"F4.wireOp",EDGE,"E44.0"),sQuery(id+"F4.wireOp",EDGE,"E44.1"),sQuery(id+"F4.wireOp",EDGE,"E44.2"),sQuery(id+"F4.wireOp",EDGE,"E44.3"),sQuery(id+"F4.wireOp",EDGE,"E44.4"),sQuery(id+"F4.wireOp",EDGE,"E44.5")])],"isStart":false})]})],"blendedInto":[makeQuery(id+"F7.opBoolean","MERGE",FACE,{"derivedFrom":[makeQuery(id+"F3.opExtrude","CAP_FACE",FACE,{"disambiguationData":[OSD([sQuery(id+"F2.wireOp",EDGE,"E10.0"),sQuery(id+"F2.wireOp",EDGE,"E10.1"),sQuery(id+"F2.wireOp",EDGE,"E10.2"),sQuery(id+"F2.wireOp",EDGE,"E10.3"),sQuery(id+"F2.wireOp",EDGE,"E10.4"),sQuery(id+"F2.wireOp",EDGE,"E10.5")])],"isStart":true}),makeQuery(id+"F3.opExtrude","CAP_FACE",FACE,{"disambiguationData":[OSD([sQuery(id+"F2.wireOp",EDGE,"E11"),sQuery(id+"F2.wireOp",EDGE,"E12"),sQuery(id+"F2.wireOp",EDGE,"E13"),sQuery(id+"F2.wireOp",EDGE,"E14"),sQuery(id+"F2.wireOp",EDGE,"E15"),sQuery(id+"F2.wireOp",EDGE,"E16"),sQuery(id+"F2.wireOp",EDGE,"E17"),sQuery(id+"F2.wireOp",EDGE,"E18"),sQuery(id+"F2.wireOp",EDGE,"E19"),sQuery(id+"F2.wireOp",EDGE,"E20"),sQuery(id+"F2.wireOp",EDGE,"E21"),sQuery(id+"F2.wireOp",EDGE,"E22"),sQuery(id+"F2.wireOp",EDGE,"E23"),sQuery(id+"F2.wireOp",EDGE,"E24.filletArc"),sQuery(id+"F2.wireOp",EDGE,"E25"),sQuery(id+"F2.wireOp",EDGE,"E26"),sQuery(id+"F2.wireOp",EDGE,"E27.filletArc"),subQ0,sQuery(id+"F2.wireOp",EDGE,"E29"),sQuery(id+"F2.wireOp",EDGE,"E30"),sQuery(id+"F2.wireOp",EDGE,"E31"),sQuery(id+"F2.wireOp",EDGE,"E32"),sQuery(id+"F2.wireOp",EDGE,"E33"),sQuery(id+"F2.wireOp",EDGE,"E34"),sQuery(id+"F2.wireOp",EDGE,"E35"),sQuery(id+"F2.wireOp",EDGE,"E36"),sQuery(id+"F2.wireOp",EDGE,"E37"),sQuery(id+"F2.wireOp",EDGE,"E38"),sQuery(id+"F2.wireOp",EDGE,"E39.filletArc"),sQuery(id+"F2.wireOp",EDGE,"E40.filletArc"),sQuery(id+"F2.wireOp",EDGE,"E41.filletArc"),sQuery(id+"F2.wireOp",EDGE,"E42.filletArc")])],"isStart":true}),makeQuery(id+"F6.opExtrude","CAP_FACE",FACE,{"disambiguationData":[OSD([sQuery(id+"F4.wireOp",EDGE,"E43"),sQuery(id+"F4.wireOp",EDGE,"E44.0"),sQuery(id+"F4.wireOp",EDGE,"E44.1"),sQuery(id+"F4.wireOp",EDGE,"E44.2"),sQuery(id+"F4.wireOp",EDGE,"E44.3"),sQuery(id+"F4.wireOp",EDGE,"E44.4"),sQuery(id+"F4.wireOp",EDGE,"E44.5")])],"isStart":false})]})]});}
            var Q38;
            {var subQ0=sQuery(id+"F2.wireOp",EDGE,"E14");Q38=makeQuery(id+"Fk14XMOrtsRoLGN_1.opChamfer","BLEND_EDGE",EDGE,{"blendedFrom":[makeQuery(id+"F7.opBoolean","INTERSECT",EDGE,{"derivedFrom":[makeQuery(id+"F1.opRevolve","SWEPT_FACE",FACE,{"disambiguationData":[OSD([sQuery(id+"F0.wireOp",EDGE,"E5"),sQuery(id+"F0.wireOp",EDGE,"E6")])]}),makeQuery(id+"F3.opExtrude","SWEPT_FACE",FACE,{"disambiguationData":[OSD([subQ0])]})]}),makeQuery(id+"F7.opBoolean","MERGE",FACE,{"derivedFrom":[makeQuery(id+"F3.opExtrude","CAP_FACE",FACE,{"disambiguationData":[OSD([sQuery(id+"F2.wireOp",EDGE,"E10.0"),sQuery(id+"F2.wireOp",EDGE,"E10.1"),sQuery(id+"F2.wireOp",EDGE,"E10.2"),sQuery(id+"F2.wireOp",EDGE,"E10.3"),sQuery(id+"F2.wireOp",EDGE,"E10.4"),sQuery(id+"F2.wireOp",EDGE,"E10.5")])],"isStart":true}),makeQuery(id+"F3.opExtrude","CAP_FACE",FACE,{"disambiguationData":[OSD([sQuery(id+"F2.wireOp",EDGE,"E11"),sQuery(id+"F2.wireOp",EDGE,"E12"),sQuery(id+"F2.wireOp",EDGE,"E13"),subQ0,sQuery(id+"F2.wireOp",EDGE,"E15"),sQuery(id+"F2.wireOp",EDGE,"E16"),sQuery(id+"F2.wireOp",EDGE,"E17"),sQuery(id+"F2.wireOp",EDGE,"E18"),sQuery(id+"F2.wireOp",EDGE,"E19"),sQuery(id+"F2.wireOp",EDGE,"E20"),sQuery(id+"F2.wireOp",EDGE,"E21"),sQuery(id+"F2.wireOp",EDGE,"E22"),sQuery(id+"F2.wireOp",EDGE,"E23"),sQuery(id+"F2.wireOp",EDGE,"E24.filletArc"),sQuery(id+"F2.wireOp",EDGE,"E25"),sQuery(id+"F2.wireOp",EDGE,"E26"),sQuery(id+"F2.wireOp",EDGE,"E27.filletArc"),sQuery(id+"F2.wireOp",EDGE,"E28"),sQuery(id+"F2.wireOp",EDGE,"E29"),sQuery(id+"F2.wireOp",EDGE,"E30"),sQuery(id+"F2.wireOp",EDGE,"E31"),sQuery(id+"F2.wireOp",EDGE,"E32"),sQuery(id+"F2.wireOp",EDGE,"E33"),sQuery(id+"F2.wireOp",EDGE,"E34"),sQuery(id+"F2.wireOp",EDGE,"E35"),sQuery(id+"F2.wireOp",EDGE,"E36"),sQuery(id+"F2.wireOp",EDGE,"E37"),sQuery(id+"F2.wireOp",EDGE,"E38"),sQuery(id+"F2.wireOp",EDGE,"E39.filletArc"),sQuery(id+"F2.wireOp",EDGE,"E40.filletArc"),sQuery(id+"F2.wireOp",EDGE,"E41.filletArc"),sQuery(id+"F2.wireOp",EDGE,"E42.filletArc")])],"isStart":true}),makeQuery(id+"F6.opExtrude","CAP_FACE",FACE,{"disambiguationData":[OSD([sQuery(id+"F4.wireOp",EDGE,"E43"),sQuery(id+"F4.wireOp",EDGE,"E44.0"),sQuery(id+"F4.wireOp",EDGE,"E44.1"),sQuery(id+"F4.wireOp",EDGE,"E44.2"),sQuery(id+"F4.wireOp",EDGE,"E44.3"),sQuery(id+"F4.wireOp",EDGE,"E44.4"),sQuery(id+"F4.wireOp",EDGE,"E44.5")])],"isStart":false})]})],"blendedInto":[makeQuery(id+"F7.opBoolean","MERGE",FACE,{"derivedFrom":[makeQuery(id+"F3.opExtrude","CAP_FACE",FACE,{"disambiguationData":[OSD([sQuery(id+"F2.wireOp",EDGE,"E10.0"),sQuery(id+"F2.wireOp",EDGE,"E10.1"),sQuery(id+"F2.wireOp",EDGE,"E10.2"),sQuery(id+"F2.wireOp",EDGE,"E10.3"),sQuery(id+"F2.wireOp",EDGE,"E10.4"),sQuery(id+"F2.wireOp",EDGE,"E10.5")])],"isStart":true}),makeQuery(id+"F3.opExtrude","CAP_FACE",FACE,{"disambiguationData":[OSD([sQuery(id+"F2.wireOp",EDGE,"E11"),sQuery(id+"F2.wireOp",EDGE,"E12"),sQuery(id+"F2.wireOp",EDGE,"E13"),subQ0,sQuery(id+"F2.wireOp",EDGE,"E15"),sQuery(id+"F2.wireOp",EDGE,"E16"),sQuery(id+"F2.wireOp",EDGE,"E17"),sQuery(id+"F2.wireOp",EDGE,"E18"),sQuery(id+"F2.wireOp",EDGE,"E19"),sQuery(id+"F2.wireOp",EDGE,"E20"),sQuery(id+"F2.wireOp",EDGE,"E21"),sQuery(id+"F2.wireOp",EDGE,"E22"),sQuery(id+"F2.wireOp",EDGE,"E23"),sQuery(id+"F2.wireOp",EDGE,"E24.filletArc"),sQuery(id+"F2.wireOp",EDGE,"E25"),sQuery(id+"F2.wireOp",EDGE,"E26"),sQuery(id+"F2.wireOp",EDGE,"E27.filletArc"),sQuery(id+"F2.wireOp",EDGE,"E28"),sQuery(id+"F2.wireOp",EDGE,"E29"),sQuery(id+"F2.wireOp",EDGE,"E30"),sQuery(id+"F2.wireOp",EDGE,"E31"),sQuery(id+"F2.wireOp",EDGE,"E32"),sQuery(id+"F2.wireOp",EDGE,"E33"),sQuery(id+"F2.wireOp",EDGE,"E34"),sQuery(id+"F2.wireOp",EDGE,"E35"),sQuery(id+"F2.wireOp",EDGE,"E36"),sQuery(id+"F2.wireOp",EDGE,"E37"),sQuery(id+"F2.wireOp",EDGE,"E38"),sQuery(id+"F2.wireOp",EDGE,"E39.filletArc"),sQuery(id+"F2.wireOp",EDGE,"E40.filletArc"),sQuery(id+"F2.wireOp",EDGE,"E41.filletArc"),sQuery(id+"F2.wireOp",EDGE,"E42.filletArc")])],"isStart":true}),makeQuery(id+"F6.opExtrude","CAP_FACE",FACE,{"disambiguationData":[OSD([sQuery(id+"F4.wireOp",EDGE,"E43"),sQuery(id+"F4.wireOp",EDGE,"E44.0"),sQuery(id+"F4.wireOp",EDGE,"E44.1"),sQuery(id+"F4.wireOp",EDGE,"E44.2"),sQuery(id+"F4.wireOp",EDGE,"E44.3"),sQuery(id+"F4.wireOp",EDGE,"E44.4"),sQuery(id+"F4.wireOp",EDGE,"E44.5")])],"isStart":false})]})]});}
            var Q39;
            {var subQ0=sQuery(id+"F2.wireOp",EDGE,"E17");Q39=makeQuery(id+"Fk14XMOrtsRoLGN_1.opChamfer","BLEND_EDGE",EDGE,{"blendedFrom":[makeQuery(id+"F7.opBoolean","INTERSECT",EDGE,{"derivedFrom":[makeQuery(id+"F1.opRevolve","SWEPT_FACE",FACE,{"disambiguationData":[OSD([sQuery(id+"F0.wireOp",EDGE,"E5"),sQuery(id+"F0.wireOp",EDGE,"E6")])]}),makeQuery(id+"F3.opExtrude","SWEPT_FACE",FACE,{"disambiguationData":[OSD([subQ0])]})]}),makeQuery(id+"F3.opExtrude","CAP_FACE",FACE,{"disambiguationData":[OSD([sQuery(id+"F2.wireOp",EDGE,"E11"),sQuery(id+"F2.wireOp",EDGE,"E12"),sQuery(id+"F2.wireOp",EDGE,"E13"),sQuery(id+"F2.wireOp",EDGE,"E14"),sQuery(id+"F2.wireOp",EDGE,"E15"),sQuery(id+"F2.wireOp",EDGE,"E16"),subQ0,sQuery(id+"F2.wireOp",EDGE,"E18"),sQuery(id+"F2.wireOp",EDGE,"E19"),sQuery(id+"F2.wireOp",EDGE,"E20"),sQuery(id+"F2.wireOp",EDGE,"E21"),sQuery(id+"F2.wireOp",EDGE,"E22"),sQuery(id+"F2.wireOp",EDGE,"E23"),sQuery(id+"F2.wireOp",EDGE,"E24.filletArc"),sQuery(id+"F2.wireOp",EDGE,"E25"),sQuery(id+"F2.wireOp",EDGE,"E26"),sQuery(id+"F2.wireOp",EDGE,"E27.filletArc"),sQuery(id+"F2.wireOp",EDGE,"E28"),sQuery(id+"F2.wireOp",EDGE,"E29"),sQuery(id+"F2.wireOp",EDGE,"E30"),sQuery(id+"F2.wireOp",EDGE,"E31"),sQuery(id+"F2.wireOp",EDGE,"E32"),sQuery(id+"F2.wireOp",EDGE,"E33"),sQuery(id+"F2.wireOp",EDGE,"E34"),sQuery(id+"F2.wireOp",EDGE,"E35"),sQuery(id+"F2.wireOp",EDGE,"E36"),sQuery(id+"F2.wireOp",EDGE,"E37"),sQuery(id+"F2.wireOp",EDGE,"E38"),sQuery(id+"F2.wireOp",EDGE,"E39.filletArc"),sQuery(id+"F2.wireOp",EDGE,"E40.filletArc"),sQuery(id+"F2.wireOp",EDGE,"E41.filletArc"),sQuery(id+"F2.wireOp",EDGE,"E42.filletArc")])],"isStart":false})],"blendedInto":[makeQuery(id+"F3.opExtrude","CAP_FACE",FACE,{"disambiguationData":[OSD([sQuery(id+"F2.wireOp",EDGE,"E11"),sQuery(id+"F2.wireOp",EDGE,"E12"),sQuery(id+"F2.wireOp",EDGE,"E13"),sQuery(id+"F2.wireOp",EDGE,"E14"),sQuery(id+"F2.wireOp",EDGE,"E15"),sQuery(id+"F2.wireOp",EDGE,"E16"),subQ0,sQuery(id+"F2.wireOp",EDGE,"E18"),sQuery(id+"F2.wireOp",EDGE,"E19"),sQuery(id+"F2.wireOp",EDGE,"E20"),sQuery(id+"F2.wireOp",EDGE,"E21"),sQuery(id+"F2.wireOp",EDGE,"E22"),sQuery(id+"F2.wireOp",EDGE,"E23"),sQuery(id+"F2.wireOp",EDGE,"E24.filletArc"),sQuery(id+"F2.wireOp",EDGE,"E25"),sQuery(id+"F2.wireOp",EDGE,"E26"),sQuery(id+"F2.wireOp",EDGE,"E27.filletArc"),sQuery(id+"F2.wireOp",EDGE,"E28"),sQuery(id+"F2.wireOp",EDGE,"E29"),sQuery(id+"F2.wireOp",EDGE,"E30"),sQuery(id+"F2.wireOp",EDGE,"E31"),sQuery(id+"F2.wireOp",EDGE,"E32"),sQuery(id+"F2.wireOp",EDGE,"E33"),sQuery(id+"F2.wireOp",EDGE,"E34"),sQuery(id+"F2.wireOp",EDGE,"E35"),sQuery(id+"F2.wireOp",EDGE,"E36"),sQuery(id+"F2.wireOp",EDGE,"E37"),sQuery(id+"F2.wireOp",EDGE,"E38"),sQuery(id+"F2.wireOp",EDGE,"E39.filletArc"),sQuery(id+"F2.wireOp",EDGE,"E40.filletArc"),sQuery(id+"F2.wireOp",EDGE,"E41.filletArc"),sQuery(id+"F2.wireOp",EDGE,"E42.filletArc")])],"isStart":false})]});}
            fillet(context, id + "F12", {"entities" : qUnion([Q0, Q1, Q2, Q3, Q4, Q5, Q6, Q7, Q8, Q9, Q10, Q11, Q12, Q13, Q14, Q15, Q16, Q17, Q18, Q19, Q20, Q21, Q22, Q23, Q24, Q25, Q26, Q27, Q28, Q29, Q30, Q31, Q32, Q33, Q34, Q35, Q36, Q37, Q38, Q39]), "radius" : 1.78 * mm, "tangentPropagation" : true, "allowEdgeOverflow" : false});
        }
        {
            var Q0;
            Q0=makeQuery(id+"F1.opRevolve","SWEPT_EDGE",EDGE,{"disambiguationData":[OSD([sQuery(id+"F0.wireOp",EDGE,"E4"),sQuery(id+"F0.wireOp",EDGE,"E6")])]});
            var Q1;
            Q1=makeQuery(id+"F1.opRevolve","SWEPT_EDGE",EDGE,{"disambiguationData":[OSD([sQuery(id+"F0.wireOp",EDGE,"E3"),sQuery(id+"F0.wireOp",EDGE,"E5")])]});
            fillet(context, id + "F13", {"entities" : qUnion([Q0, Q1]), "radius" : 5.08 * mm, "tangentPropagation" : true, "allowEdgeOverflow" : false});
        }
        {
            var Q0;
            Q0=makeQuery(id+"F13.opFillet","BLEND_EDGE",EDGE,{"disambiguationData":[OD(1.0)],"blendedFrom":[makeQuery(id+"F1.opRevolve","SWEPT_EDGE",EDGE,{"disambiguationData":[OSD([sQuery(id+"F0.wireOp",EDGE,"E3"),sQuery(id+"F0.wireOp",EDGE,"E5")])]}),makeQuery(id+"F7.opBoolean","MERGE",FACE,{"derivedFrom":[makeQuery(id+"F3.opExtrude","CAP_FACE",FACE,{"disambiguationData":[OSD([sQuery(id+"F2.wireOp",EDGE,"E10.0"),sQuery(id+"F2.wireOp",EDGE,"E10.1"),sQuery(id+"F2.wireOp",EDGE,"E10.2"),sQuery(id+"F2.wireOp",EDGE,"E10.3"),sQuery(id+"F2.wireOp",EDGE,"E10.4"),sQuery(id+"F2.wireOp",EDGE,"E10.5")])],"isStart":true}),makeQuery(id+"F3.opExtrude","CAP_FACE",FACE,{"disambiguationData":[OSD([sQuery(id+"F2.wireOp",EDGE,"E11"),sQuery(id+"F2.wireOp",EDGE,"E12"),sQuery(id+"F2.wireOp",EDGE,"E13"),sQuery(id+"F2.wireOp",EDGE,"E14"),sQuery(id+"F2.wireOp",EDGE,"E15"),sQuery(id+"F2.wireOp",EDGE,"E16"),sQuery(id+"F2.wireOp",EDGE,"E17"),sQuery(id+"F2.wireOp",EDGE,"E18"),sQuery(id+"F2.wireOp",EDGE,"E19"),sQuery(id+"F2.wireOp",EDGE,"E20"),sQuery(id+"F2.wireOp",EDGE,"E21"),sQuery(id+"F2.wireOp",EDGE,"E22"),sQuery(id+"F2.wireOp",EDGE,"E23"),sQuery(id+"F2.wireOp",EDGE,"E24.filletArc"),sQuery(id+"F2.wireOp",EDGE,"E25"),sQuery(id+"F2.wireOp",EDGE,"E26"),sQuery(id+"F2.wireOp",EDGE,"E27.filletArc"),sQuery(id+"F2.wireOp",EDGE,"E28"),sQuery(id+"F2.wireOp",EDGE,"E29"),sQuery(id+"F2.wireOp",EDGE,"E30"),sQuery(id+"F2.wireOp",EDGE,"E31"),sQuery(id+"F2.wireOp",EDGE,"E32"),sQuery(id+"F2.wireOp",EDGE,"E33"),sQuery(id+"F2.wireOp",EDGE,"E34"),sQuery(id+"F2.wireOp",EDGE,"E35"),sQuery(id+"F2.wireOp",EDGE,"E36"),sQuery(id+"F2.wireOp",EDGE,"E37"),sQuery(id+"F2.wireOp",EDGE,"E38"),sQuery(id+"F2.wireOp",EDGE,"E39.filletArc"),sQuery(id+"F2.wireOp",EDGE,"E40.filletArc"),sQuery(id+"F2.wireOp",EDGE,"E41.filletArc"),sQuery(id+"F2.wireOp",EDGE,"E42.filletArc")])],"isStart":true}),makeQuery(id+"F6.opExtrude","CAP_FACE",FACE,{"disambiguationData":[OSD([sQuery(id+"F4.wireOp",EDGE,"E43"),sQuery(id+"F4.wireOp",EDGE,"E44.0"),sQuery(id+"F4.wireOp",EDGE,"E44.1"),sQuery(id+"F4.wireOp",EDGE,"E44.2"),sQuery(id+"F4.wireOp",EDGE,"E44.3"),sQuery(id+"F4.wireOp",EDGE,"E44.4"),sQuery(id+"F4.wireOp",EDGE,"E44.5")])],"isStart":false})]})],"blendedInto":[makeQuery(id+"F7.opBoolean","MERGE",FACE,{"derivedFrom":[makeQuery(id+"F3.opExtrude","CAP_FACE",FACE,{"disambiguationData":[OSD([sQuery(id+"F2.wireOp",EDGE,"E10.0"),sQuery(id+"F2.wireOp",EDGE,"E10.1"),sQuery(id+"F2.wireOp",EDGE,"E10.2"),sQuery(id+"F2.wireOp",EDGE,"E10.3"),sQuery(id+"F2.wireOp",EDGE,"E10.4"),sQuery(id+"F2.wireOp",EDGE,"E10.5")])],"isStart":true}),makeQuery(id+"F3.opExtrude","CAP_FACE",FACE,{"disambiguationData":[OSD([sQuery(id+"F2.wireOp",EDGE,"E11"),sQuery(id+"F2.wireOp",EDGE,"E12"),sQuery(id+"F2.wireOp",EDGE,"E13"),sQuery(id+"F2.wireOp",EDGE,"E14"),sQuery(id+"F2.wireOp",EDGE,"E15"),sQuery(id+"F2.wireOp",EDGE,"E16"),sQuery(id+"F2.wireOp",EDGE,"E17"),sQuery(id+"F2.wireOp",EDGE,"E18"),sQuery(id+"F2.wireOp",EDGE,"E19"),sQuery(id+"F2.wireOp",EDGE,"E20"),sQuery(id+"F2.wireOp",EDGE,"E21"),sQuery(id+"F2.wireOp",EDGE,"E22"),sQuery(id+"F2.wireOp",EDGE,"E23"),sQuery(id+"F2.wireOp",EDGE,"E24.filletArc"),sQuery(id+"F2.wireOp",EDGE,"E25"),sQuery(id+"F2.wireOp",EDGE,"E26"),sQuery(id+"F2.wireOp",EDGE,"E27.filletArc"),sQuery(id+"F2.wireOp",EDGE,"E28"),sQuery(id+"F2.wireOp",EDGE,"E29"),sQuery(id+"F2.wireOp",EDGE,"E30"),sQuery(id+"F2.wireOp",EDGE,"E31"),sQuery(id+"F2.wireOp",EDGE,"E32"),sQuery(id+"F2.wireOp",EDGE,"E33"),sQuery(id+"F2.wireOp",EDGE,"E34"),sQuery(id+"F2.wireOp",EDGE,"E35"),sQuery(id+"F2.wireOp",EDGE,"E36"),sQuery(id+"F2.wireOp",EDGE,"E37"),sQuery(id+"F2.wireOp",EDGE,"E38"),sQuery(id+"F2.wireOp",EDGE,"E39.filletArc"),sQuery(id+"F2.wireOp",EDGE,"E40.filletArc"),sQuery(id+"F2.wireOp",EDGE,"E41.filletArc"),sQuery(id+"F2.wireOp",EDGE,"E42.filletArc")])],"isStart":true}),makeQuery(id+"F6.opExtrude","CAP_FACE",FACE,{"disambiguationData":[OSD([sQuery(id+"F4.wireOp",EDGE,"E43"),sQuery(id+"F4.wireOp",EDGE,"E44.0"),sQuery(id+"F4.wireOp",EDGE,"E44.1"),sQuery(id+"F4.wireOp",EDGE,"E44.2"),sQuery(id+"F4.wireOp",EDGE,"E44.3"),sQuery(id+"F4.wireOp",EDGE,"E44.4"),sQuery(id+"F4.wireOp",EDGE,"E44.5")])],"isStart":false})]})]});
            var Q1;
            Q1=makeQuery(id+"F13.opFillet","BLEND_EDGE",EDGE,{"disambiguationData":[OD(0.0)],"blendedFrom":[makeQuery(id+"F1.opRevolve","SWEPT_EDGE",EDGE,{"disambiguationData":[OSD([sQuery(id+"F0.wireOp",EDGE,"E3"),sQuery(id+"F0.wireOp",EDGE,"E5")])]}),makeQuery(id+"F7.opBoolean","MERGE",FACE,{"derivedFrom":[makeQuery(id+"F3.opExtrude","CAP_FACE",FACE,{"disambiguationData":[OSD([sQuery(id+"F2.wireOp",EDGE,"E10.0"),sQuery(id+"F2.wireOp",EDGE,"E10.1"),sQuery(id+"F2.wireOp",EDGE,"E10.2"),sQuery(id+"F2.wireOp",EDGE,"E10.3"),sQuery(id+"F2.wireOp",EDGE,"E10.4"),sQuery(id+"F2.wireOp",EDGE,"E10.5")])],"isStart":true}),makeQuery(id+"F3.opExtrude","CAP_FACE",FACE,{"disambiguationData":[OSD([sQuery(id+"F2.wireOp",EDGE,"E11"),sQuery(id+"F2.wireOp",EDGE,"E12"),sQuery(id+"F2.wireOp",EDGE,"E13"),sQuery(id+"F2.wireOp",EDGE,"E14"),sQuery(id+"F2.wireOp",EDGE,"E15"),sQuery(id+"F2.wireOp",EDGE,"E16"),sQuery(id+"F2.wireOp",EDGE,"E17"),sQuery(id+"F2.wireOp",EDGE,"E18"),sQuery(id+"F2.wireOp",EDGE,"E19"),sQuery(id+"F2.wireOp",EDGE,"E20"),sQuery(id+"F2.wireOp",EDGE,"E21"),sQuery(id+"F2.wireOp",EDGE,"E22"),sQuery(id+"F2.wireOp",EDGE,"E23"),sQuery(id+"F2.wireOp",EDGE,"E24.filletArc"),sQuery(id+"F2.wireOp",EDGE,"E25"),sQuery(id+"F2.wireOp",EDGE,"E26"),sQuery(id+"F2.wireOp",EDGE,"E27.filletArc"),sQuery(id+"F2.wireOp",EDGE,"E28"),sQuery(id+"F2.wireOp",EDGE,"E29"),sQuery(id+"F2.wireOp",EDGE,"E30"),sQuery(id+"F2.wireOp",EDGE,"E31"),sQuery(id+"F2.wireOp",EDGE,"E32"),sQuery(id+"F2.wireOp",EDGE,"E33"),sQuery(id+"F2.wireOp",EDGE,"E34"),sQuery(id+"F2.wireOp",EDGE,"E35"),sQuery(id+"F2.wireOp",EDGE,"E36"),sQuery(id+"F2.wireOp",EDGE,"E37"),sQuery(id+"F2.wireOp",EDGE,"E38"),sQuery(id+"F2.wireOp",EDGE,"E39.filletArc"),sQuery(id+"F2.wireOp",EDGE,"E40.filletArc"),sQuery(id+"F2.wireOp",EDGE,"E41.filletArc"),sQuery(id+"F2.wireOp",EDGE,"E42.filletArc")])],"isStart":true}),makeQuery(id+"F6.opExtrude","CAP_FACE",FACE,{"disambiguationData":[OSD([sQuery(id+"F4.wireOp",EDGE,"E43"),sQuery(id+"F4.wireOp",EDGE,"E44.0"),sQuery(id+"F4.wireOp",EDGE,"E44.1"),sQuery(id+"F4.wireOp",EDGE,"E44.2"),sQuery(id+"F4.wireOp",EDGE,"E44.3"),sQuery(id+"F4.wireOp",EDGE,"E44.4"),sQuery(id+"F4.wireOp",EDGE,"E44.5")])],"isStart":false})]})],"blendedInto":[makeQuery(id+"F7.opBoolean","MERGE",FACE,{"derivedFrom":[makeQuery(id+"F3.opExtrude","CAP_FACE",FACE,{"disambiguationData":[OSD([sQuery(id+"F2.wireOp",EDGE,"E10.0"),sQuery(id+"F2.wireOp",EDGE,"E10.1"),sQuery(id+"F2.wireOp",EDGE,"E10.2"),sQuery(id+"F2.wireOp",EDGE,"E10.3"),sQuery(id+"F2.wireOp",EDGE,"E10.4"),sQuery(id+"F2.wireOp",EDGE,"E10.5")])],"isStart":true}),makeQuery(id+"F3.opExtrude","CAP_FACE",FACE,{"disambiguationData":[OSD([sQuery(id+"F2.wireOp",EDGE,"E11"),sQuery(id+"F2.wireOp",EDGE,"E12"),sQuery(id+"F2.wireOp",EDGE,"E13"),sQuery(id+"F2.wireOp",EDGE,"E14"),sQuery(id+"F2.wireOp",EDGE,"E15"),sQuery(id+"F2.wireOp",EDGE,"E16"),sQuery(id+"F2.wireOp",EDGE,"E17"),sQuery(id+"F2.wireOp",EDGE,"E18"),sQuery(id+"F2.wireOp",EDGE,"E19"),sQuery(id+"F2.wireOp",EDGE,"E20"),sQuery(id+"F2.wireOp",EDGE,"E21"),sQuery(id+"F2.wireOp",EDGE,"E22"),sQuery(id+"F2.wireOp",EDGE,"E23"),sQuery(id+"F2.wireOp",EDGE,"E24.filletArc"),sQuery(id+"F2.wireOp",EDGE,"E25"),sQuery(id+"F2.wireOp",EDGE,"E26"),sQuery(id+"F2.wireOp",EDGE,"E27.filletArc"),sQuery(id+"F2.wireOp",EDGE,"E28"),sQuery(id+"F2.wireOp",EDGE,"E29"),sQuery(id+"F2.wireOp",EDGE,"E30"),sQuery(id+"F2.wireOp",EDGE,"E31"),sQuery(id+"F2.wireOp",EDGE,"E32"),sQuery(id+"F2.wireOp",EDGE,"E33"),sQuery(id+"F2.wireOp",EDGE,"E34"),sQuery(id+"F2.wireOp",EDGE,"E35"),sQuery(id+"F2.wireOp",EDGE,"E36"),sQuery(id+"F2.wireOp",EDGE,"E37"),sQuery(id+"F2.wireOp",EDGE,"E38"),sQuery(id+"F2.wireOp",EDGE,"E39.filletArc"),sQuery(id+"F2.wireOp",EDGE,"E40.filletArc"),sQuery(id+"F2.wireOp",EDGE,"E41.filletArc"),sQuery(id+"F2.wireOp",EDGE,"E42.filletArc")])],"isStart":true}),makeQuery(id+"F6.opExtrude","CAP_FACE",FACE,{"disambiguationData":[OSD([sQuery(id+"F4.wireOp",EDGE,"E43"),sQuery(id+"F4.wireOp",EDGE,"E44.0"),sQuery(id+"F4.wireOp",EDGE,"E44.1"),sQuery(id+"F4.wireOp",EDGE,"E44.2"),sQuery(id+"F4.wireOp",EDGE,"E44.3"),sQuery(id+"F4.wireOp",EDGE,"E44.4"),sQuery(id+"F4.wireOp",EDGE,"E44.5")])],"isStart":false})]})]});
            var Q2;
            Q2=makeQuery(id+"F13.opFillet","BLEND_EDGE",EDGE,{"disambiguationData":[OD(2.0)],"blendedFrom":[makeQuery(id+"F1.opRevolve","SWEPT_EDGE",EDGE,{"disambiguationData":[OSD([sQuery(id+"F0.wireOp",EDGE,"E3"),sQuery(id+"F0.wireOp",EDGE,"E5")])]}),makeQuery(id+"F7.opBoolean","MERGE",FACE,{"derivedFrom":[makeQuery(id+"F3.opExtrude","CAP_FACE",FACE,{"disambiguationData":[OSD([sQuery(id+"F2.wireOp",EDGE,"E10.0"),sQuery(id+"F2.wireOp",EDGE,"E10.1"),sQuery(id+"F2.wireOp",EDGE,"E10.2"),sQuery(id+"F2.wireOp",EDGE,"E10.3"),sQuery(id+"F2.wireOp",EDGE,"E10.4"),sQuery(id+"F2.wireOp",EDGE,"E10.5")])],"isStart":true}),makeQuery(id+"F3.opExtrude","CAP_FACE",FACE,{"disambiguationData":[OSD([sQuery(id+"F2.wireOp",EDGE,"E11"),sQuery(id+"F2.wireOp",EDGE,"E12"),sQuery(id+"F2.wireOp",EDGE,"E13"),sQuery(id+"F2.wireOp",EDGE,"E14"),sQuery(id+"F2.wireOp",EDGE,"E15"),sQuery(id+"F2.wireOp",EDGE,"E16"),sQuery(id+"F2.wireOp",EDGE,"E17"),sQuery(id+"F2.wireOp",EDGE,"E18"),sQuery(id+"F2.wireOp",EDGE,"E19"),sQuery(id+"F2.wireOp",EDGE,"E20"),sQuery(id+"F2.wireOp",EDGE,"E21"),sQuery(id+"F2.wireOp",EDGE,"E22"),sQuery(id+"F2.wireOp",EDGE,"E23"),sQuery(id+"F2.wireOp",EDGE,"E24.filletArc"),sQuery(id+"F2.wireOp",EDGE,"E25"),sQuery(id+"F2.wireOp",EDGE,"E26"),sQuery(id+"F2.wireOp",EDGE,"E27.filletArc"),sQuery(id+"F2.wireOp",EDGE,"E28"),sQuery(id+"F2.wireOp",EDGE,"E29"),sQuery(id+"F2.wireOp",EDGE,"E30"),sQuery(id+"F2.wireOp",EDGE,"E31"),sQuery(id+"F2.wireOp",EDGE,"E32"),sQuery(id+"F2.wireOp",EDGE,"E33"),sQuery(id+"F2.wireOp",EDGE,"E34"),sQuery(id+"F2.wireOp",EDGE,"E35"),sQuery(id+"F2.wireOp",EDGE,"E36"),sQuery(id+"F2.wireOp",EDGE,"E37"),sQuery(id+"F2.wireOp",EDGE,"E38"),sQuery(id+"F2.wireOp",EDGE,"E39.filletArc"),sQuery(id+"F2.wireOp",EDGE,"E40.filletArc"),sQuery(id+"F2.wireOp",EDGE,"E41.filletArc"),sQuery(id+"F2.wireOp",EDGE,"E42.filletArc")])],"isStart":true}),makeQuery(id+"F6.opExtrude","CAP_FACE",FACE,{"disambiguationData":[OSD([sQuery(id+"F4.wireOp",EDGE,"E43"),sQuery(id+"F4.wireOp",EDGE,"E44.0"),sQuery(id+"F4.wireOp",EDGE,"E44.1"),sQuery(id+"F4.wireOp",EDGE,"E44.2"),sQuery(id+"F4.wireOp",EDGE,"E44.3"),sQuery(id+"F4.wireOp",EDGE,"E44.4"),sQuery(id+"F4.wireOp",EDGE,"E44.5")])],"isStart":false})]})],"blendedInto":[makeQuery(id+"F7.opBoolean","MERGE",FACE,{"derivedFrom":[makeQuery(id+"F3.opExtrude","CAP_FACE",FACE,{"disambiguationData":[OSD([sQuery(id+"F2.wireOp",EDGE,"E10.0"),sQuery(id+"F2.wireOp",EDGE,"E10.1"),sQuery(id+"F2.wireOp",EDGE,"E10.2"),sQuery(id+"F2.wireOp",EDGE,"E10.3"),sQuery(id+"F2.wireOp",EDGE,"E10.4"),sQuery(id+"F2.wireOp",EDGE,"E10.5")])],"isStart":true}),makeQuery(id+"F3.opExtrude","CAP_FACE",FACE,{"disambiguationData":[OSD([sQuery(id+"F2.wireOp",EDGE,"E11"),sQuery(id+"F2.wireOp",EDGE,"E12"),sQuery(id+"F2.wireOp",EDGE,"E13"),sQuery(id+"F2.wireOp",EDGE,"E14"),sQuery(id+"F2.wireOp",EDGE,"E15"),sQuery(id+"F2.wireOp",EDGE,"E16"),sQuery(id+"F2.wireOp",EDGE,"E17"),sQuery(id+"F2.wireOp",EDGE,"E18"),sQuery(id+"F2.wireOp",EDGE,"E19"),sQuery(id+"F2.wireOp",EDGE,"E20"),sQuery(id+"F2.wireOp",EDGE,"E21"),sQuery(id+"F2.wireOp",EDGE,"E22"),sQuery(id+"F2.wireOp",EDGE,"E23"),sQuery(id+"F2.wireOp",EDGE,"E24.filletArc"),sQuery(id+"F2.wireOp",EDGE,"E25"),sQuery(id+"F2.wireOp",EDGE,"E26"),sQuery(id+"F2.wireOp",EDGE,"E27.filletArc"),sQuery(id+"F2.wireOp",EDGE,"E28"),sQuery(id+"F2.wireOp",EDGE,"E29"),sQuery(id+"F2.wireOp",EDGE,"E30"),sQuery(id+"F2.wireOp",EDGE,"E31"),sQuery(id+"F2.wireOp",EDGE,"E32"),sQuery(id+"F2.wireOp",EDGE,"E33"),sQuery(id+"F2.wireOp",EDGE,"E34"),sQuery(id+"F2.wireOp",EDGE,"E35"),sQuery(id+"F2.wireOp",EDGE,"E36"),sQuery(id+"F2.wireOp",EDGE,"E37"),sQuery(id+"F2.wireOp",EDGE,"E38"),sQuery(id+"F2.wireOp",EDGE,"E39.filletArc"),sQuery(id+"F2.wireOp",EDGE,"E40.filletArc"),sQuery(id+"F2.wireOp",EDGE,"E41.filletArc"),sQuery(id+"F2.wireOp",EDGE,"E42.filletArc")])],"isStart":true}),makeQuery(id+"F6.opExtrude","CAP_FACE",FACE,{"disambiguationData":[OSD([sQuery(id+"F4.wireOp",EDGE,"E43"),sQuery(id+"F4.wireOp",EDGE,"E44.0"),sQuery(id+"F4.wireOp",EDGE,"E44.1"),sQuery(id+"F4.wireOp",EDGE,"E44.2"),sQuery(id+"F4.wireOp",EDGE,"E44.3"),sQuery(id+"F4.wireOp",EDGE,"E44.4"),sQuery(id+"F4.wireOp",EDGE,"E44.5")])],"isStart":false})]})]});
            var Q3;
            Q3=makeQuery(id+"F13.opFillet","BLEND_EDGE",EDGE,{"disambiguationData":[OD(3.0)],"blendedFrom":[makeQuery(id+"F1.opRevolve","SWEPT_EDGE",EDGE,{"disambiguationData":[OSD([sQuery(id+"F0.wireOp",EDGE,"E3"),sQuery(id+"F0.wireOp",EDGE,"E5")])]}),makeQuery(id+"F7.opBoolean","MERGE",FACE,{"derivedFrom":[makeQuery(id+"F3.opExtrude","CAP_FACE",FACE,{"disambiguationData":[OSD([sQuery(id+"F2.wireOp",EDGE,"E10.0"),sQuery(id+"F2.wireOp",EDGE,"E10.1"),sQuery(id+"F2.wireOp",EDGE,"E10.2"),sQuery(id+"F2.wireOp",EDGE,"E10.3"),sQuery(id+"F2.wireOp",EDGE,"E10.4"),sQuery(id+"F2.wireOp",EDGE,"E10.5")])],"isStart":true}),makeQuery(id+"F3.opExtrude","CAP_FACE",FACE,{"disambiguationData":[OSD([sQuery(id+"F2.wireOp",EDGE,"E11"),sQuery(id+"F2.wireOp",EDGE,"E12"),sQuery(id+"F2.wireOp",EDGE,"E13"),sQuery(id+"F2.wireOp",EDGE,"E14"),sQuery(id+"F2.wireOp",EDGE,"E15"),sQuery(id+"F2.wireOp",EDGE,"E16"),sQuery(id+"F2.wireOp",EDGE,"E17"),sQuery(id+"F2.wireOp",EDGE,"E18"),sQuery(id+"F2.wireOp",EDGE,"E19"),sQuery(id+"F2.wireOp",EDGE,"E20"),sQuery(id+"F2.wireOp",EDGE,"E21"),sQuery(id+"F2.wireOp",EDGE,"E22"),sQuery(id+"F2.wireOp",EDGE,"E23"),sQuery(id+"F2.wireOp",EDGE,"E24.filletArc"),sQuery(id+"F2.wireOp",EDGE,"E25"),sQuery(id+"F2.wireOp",EDGE,"E26"),sQuery(id+"F2.wireOp",EDGE,"E27.filletArc"),sQuery(id+"F2.wireOp",EDGE,"E28"),sQuery(id+"F2.wireOp",EDGE,"E29"),sQuery(id+"F2.wireOp",EDGE,"E30"),sQuery(id+"F2.wireOp",EDGE,"E31"),sQuery(id+"F2.wireOp",EDGE,"E32"),sQuery(id+"F2.wireOp",EDGE,"E33"),sQuery(id+"F2.wireOp",EDGE,"E34"),sQuery(id+"F2.wireOp",EDGE,"E35"),sQuery(id+"F2.wireOp",EDGE,"E36"),sQuery(id+"F2.wireOp",EDGE,"E37"),sQuery(id+"F2.wireOp",EDGE,"E38"),sQuery(id+"F2.wireOp",EDGE,"E39.filletArc"),sQuery(id+"F2.wireOp",EDGE,"E40.filletArc"),sQuery(id+"F2.wireOp",EDGE,"E41.filletArc"),sQuery(id+"F2.wireOp",EDGE,"E42.filletArc")])],"isStart":true}),makeQuery(id+"F6.opExtrude","CAP_FACE",FACE,{"disambiguationData":[OSD([sQuery(id+"F4.wireOp",EDGE,"E43"),sQuery(id+"F4.wireOp",EDGE,"E44.0"),sQuery(id+"F4.wireOp",EDGE,"E44.1"),sQuery(id+"F4.wireOp",EDGE,"E44.2"),sQuery(id+"F4.wireOp",EDGE,"E44.3"),sQuery(id+"F4.wireOp",EDGE,"E44.4"),sQuery(id+"F4.wireOp",EDGE,"E44.5")])],"isStart":false})]})],"blendedInto":[makeQuery(id+"F7.opBoolean","MERGE",FACE,{"derivedFrom":[makeQuery(id+"F3.opExtrude","CAP_FACE",FACE,{"disambiguationData":[OSD([sQuery(id+"F2.wireOp",EDGE,"E10.0"),sQuery(id+"F2.wireOp",EDGE,"E10.1"),sQuery(id+"F2.wireOp",EDGE,"E10.2"),sQuery(id+"F2.wireOp",EDGE,"E10.3"),sQuery(id+"F2.wireOp",EDGE,"E10.4"),sQuery(id+"F2.wireOp",EDGE,"E10.5")])],"isStart":true}),makeQuery(id+"F3.opExtrude","CAP_FACE",FACE,{"disambiguationData":[OSD([sQuery(id+"F2.wireOp",EDGE,"E11"),sQuery(id+"F2.wireOp",EDGE,"E12"),sQuery(id+"F2.wireOp",EDGE,"E13"),sQuery(id+"F2.wireOp",EDGE,"E14"),sQuery(id+"F2.wireOp",EDGE,"E15"),sQuery(id+"F2.wireOp",EDGE,"E16"),sQuery(id+"F2.wireOp",EDGE,"E17"),sQuery(id+"F2.wireOp",EDGE,"E18"),sQuery(id+"F2.wireOp",EDGE,"E19"),sQuery(id+"F2.wireOp",EDGE,"E20"),sQuery(id+"F2.wireOp",EDGE,"E21"),sQuery(id+"F2.wireOp",EDGE,"E22"),sQuery(id+"F2.wireOp",EDGE,"E23"),sQuery(id+"F2.wireOp",EDGE,"E24.filletArc"),sQuery(id+"F2.wireOp",EDGE,"E25"),sQuery(id+"F2.wireOp",EDGE,"E26"),sQuery(id+"F2.wireOp",EDGE,"E27.filletArc"),sQuery(id+"F2.wireOp",EDGE,"E28"),sQuery(id+"F2.wireOp",EDGE,"E29"),sQuery(id+"F2.wireOp",EDGE,"E30"),sQuery(id+"F2.wireOp",EDGE,"E31"),sQuery(id+"F2.wireOp",EDGE,"E32"),sQuery(id+"F2.wireOp",EDGE,"E33"),sQuery(id+"F2.wireOp",EDGE,"E34"),sQuery(id+"F2.wireOp",EDGE,"E35"),sQuery(id+"F2.wireOp",EDGE,"E36"),sQuery(id+"F2.wireOp",EDGE,"E37"),sQuery(id+"F2.wireOp",EDGE,"E38"),sQuery(id+"F2.wireOp",EDGE,"E39.filletArc"),sQuery(id+"F2.wireOp",EDGE,"E40.filletArc"),sQuery(id+"F2.wireOp",EDGE,"E41.filletArc"),sQuery(id+"F2.wireOp",EDGE,"E42.filletArc")])],"isStart":true}),makeQuery(id+"F6.opExtrude","CAP_FACE",FACE,{"disambiguationData":[OSD([sQuery(id+"F4.wireOp",EDGE,"E43"),sQuery(id+"F4.wireOp",EDGE,"E44.0"),sQuery(id+"F4.wireOp",EDGE,"E44.1"),sQuery(id+"F4.wireOp",EDGE,"E44.2"),sQuery(id+"F4.wireOp",EDGE,"E44.3"),sQuery(id+"F4.wireOp",EDGE,"E44.4"),sQuery(id+"F4.wireOp",EDGE,"E44.5")])],"isStart":false})]})]});
            var Q4;
            Q4=makeQuery(id+"F13.opFillet","BLEND_EDGE",EDGE,{"disambiguationData":[OD(5.0)],"blendedFrom":[makeQuery(id+"F1.opRevolve","SWEPT_EDGE",EDGE,{"disambiguationData":[OSD([sQuery(id+"F0.wireOp",EDGE,"E3"),sQuery(id+"F0.wireOp",EDGE,"E5")])]}),makeQuery(id+"F7.opBoolean","MERGE",FACE,{"derivedFrom":[makeQuery(id+"F3.opExtrude","CAP_FACE",FACE,{"disambiguationData":[OSD([sQuery(id+"F2.wireOp",EDGE,"E10.0"),sQuery(id+"F2.wireOp",EDGE,"E10.1"),sQuery(id+"F2.wireOp",EDGE,"E10.2"),sQuery(id+"F2.wireOp",EDGE,"E10.3"),sQuery(id+"F2.wireOp",EDGE,"E10.4"),sQuery(id+"F2.wireOp",EDGE,"E10.5")])],"isStart":true}),makeQuery(id+"F3.opExtrude","CAP_FACE",FACE,{"disambiguationData":[OSD([sQuery(id+"F2.wireOp",EDGE,"E11"),sQuery(id+"F2.wireOp",EDGE,"E12"),sQuery(id+"F2.wireOp",EDGE,"E13"),sQuery(id+"F2.wireOp",EDGE,"E14"),sQuery(id+"F2.wireOp",EDGE,"E15"),sQuery(id+"F2.wireOp",EDGE,"E16"),sQuery(id+"F2.wireOp",EDGE,"E17"),sQuery(id+"F2.wireOp",EDGE,"E18"),sQuery(id+"F2.wireOp",EDGE,"E19"),sQuery(id+"F2.wireOp",EDGE,"E20"),sQuery(id+"F2.wireOp",EDGE,"E21"),sQuery(id+"F2.wireOp",EDGE,"E22"),sQuery(id+"F2.wireOp",EDGE,"E23"),sQuery(id+"F2.wireOp",EDGE,"E24.filletArc"),sQuery(id+"F2.wireOp",EDGE,"E25"),sQuery(id+"F2.wireOp",EDGE,"E26"),sQuery(id+"F2.wireOp",EDGE,"E27.filletArc"),sQuery(id+"F2.wireOp",EDGE,"E28"),sQuery(id+"F2.wireOp",EDGE,"E29"),sQuery(id+"F2.wireOp",EDGE,"E30"),sQuery(id+"F2.wireOp",EDGE,"E31"),sQuery(id+"F2.wireOp",EDGE,"E32"),sQuery(id+"F2.wireOp",EDGE,"E33"),sQuery(id+"F2.wireOp",EDGE,"E34"),sQuery(id+"F2.wireOp",EDGE,"E35"),sQuery(id+"F2.wireOp",EDGE,"E36"),sQuery(id+"F2.wireOp",EDGE,"E37"),sQuery(id+"F2.wireOp",EDGE,"E38"),sQuery(id+"F2.wireOp",EDGE,"E39.filletArc"),sQuery(id+"F2.wireOp",EDGE,"E40.filletArc"),sQuery(id+"F2.wireOp",EDGE,"E41.filletArc"),sQuery(id+"F2.wireOp",EDGE,"E42.filletArc")])],"isStart":true}),makeQuery(id+"F6.opExtrude","CAP_FACE",FACE,{"disambiguationData":[OSD([sQuery(id+"F4.wireOp",EDGE,"E43"),sQuery(id+"F4.wireOp",EDGE,"E44.0"),sQuery(id+"F4.wireOp",EDGE,"E44.1"),sQuery(id+"F4.wireOp",EDGE,"E44.2"),sQuery(id+"F4.wireOp",EDGE,"E44.3"),sQuery(id+"F4.wireOp",EDGE,"E44.4"),sQuery(id+"F4.wireOp",EDGE,"E44.5")])],"isStart":false})]})],"blendedInto":[makeQuery(id+"F7.opBoolean","MERGE",FACE,{"derivedFrom":[makeQuery(id+"F3.opExtrude","CAP_FACE",FACE,{"disambiguationData":[OSD([sQuery(id+"F2.wireOp",EDGE,"E10.0"),sQuery(id+"F2.wireOp",EDGE,"E10.1"),sQuery(id+"F2.wireOp",EDGE,"E10.2"),sQuery(id+"F2.wireOp",EDGE,"E10.3"),sQuery(id+"F2.wireOp",EDGE,"E10.4"),sQuery(id+"F2.wireOp",EDGE,"E10.5")])],"isStart":true}),makeQuery(id+"F3.opExtrude","CAP_FACE",FACE,{"disambiguationData":[OSD([sQuery(id+"F2.wireOp",EDGE,"E11"),sQuery(id+"F2.wireOp",EDGE,"E12"),sQuery(id+"F2.wireOp",EDGE,"E13"),sQuery(id+"F2.wireOp",EDGE,"E14"),sQuery(id+"F2.wireOp",EDGE,"E15"),sQuery(id+"F2.wireOp",EDGE,"E16"),sQuery(id+"F2.wireOp",EDGE,"E17"),sQuery(id+"F2.wireOp",EDGE,"E18"),sQuery(id+"F2.wireOp",EDGE,"E19"),sQuery(id+"F2.wireOp",EDGE,"E20"),sQuery(id+"F2.wireOp",EDGE,"E21"),sQuery(id+"F2.wireOp",EDGE,"E22"),sQuery(id+"F2.wireOp",EDGE,"E23"),sQuery(id+"F2.wireOp",EDGE,"E24.filletArc"),sQuery(id+"F2.wireOp",EDGE,"E25"),sQuery(id+"F2.wireOp",EDGE,"E26"),sQuery(id+"F2.wireOp",EDGE,"E27.filletArc"),sQuery(id+"F2.wireOp",EDGE,"E28"),sQuery(id+"F2.wireOp",EDGE,"E29"),sQuery(id+"F2.wireOp",EDGE,"E30"),sQuery(id+"F2.wireOp",EDGE,"E31"),sQuery(id+"F2.wireOp",EDGE,"E32"),sQuery(id+"F2.wireOp",EDGE,"E33"),sQuery(id+"F2.wireOp",EDGE,"E34"),sQuery(id+"F2.wireOp",EDGE,"E35"),sQuery(id+"F2.wireOp",EDGE,"E36"),sQuery(id+"F2.wireOp",EDGE,"E37"),sQuery(id+"F2.wireOp",EDGE,"E38"),sQuery(id+"F2.wireOp",EDGE,"E39.filletArc"),sQuery(id+"F2.wireOp",EDGE,"E40.filletArc"),sQuery(id+"F2.wireOp",EDGE,"E41.filletArc"),sQuery(id+"F2.wireOp",EDGE,"E42.filletArc")])],"isStart":true}),makeQuery(id+"F6.opExtrude","CAP_FACE",FACE,{"disambiguationData":[OSD([sQuery(id+"F4.wireOp",EDGE,"E43"),sQuery(id+"F4.wireOp",EDGE,"E44.0"),sQuery(id+"F4.wireOp",EDGE,"E44.1"),sQuery(id+"F4.wireOp",EDGE,"E44.2"),sQuery(id+"F4.wireOp",EDGE,"E44.3"),sQuery(id+"F4.wireOp",EDGE,"E44.4"),sQuery(id+"F4.wireOp",EDGE,"E44.5")])],"isStart":false})]})]});
            var Q5;
            Q5=makeQuery(id+"F13.opFillet","BLEND_EDGE",EDGE,{"disambiguationData":[OD(1.0)],"blendedFrom":[makeQuery(id+"F1.opRevolve","SWEPT_EDGE",EDGE,{"disambiguationData":[OSD([sQuery(id+"F0.wireOp",EDGE,"E4"),sQuery(id+"F0.wireOp",EDGE,"E6")])]}),makeQuery(id+"F3.opExtrude","CAP_FACE",FACE,{"disambiguationData":[OSD([sQuery(id+"F2.wireOp",EDGE,"E11"),sQuery(id+"F2.wireOp",EDGE,"E12"),sQuery(id+"F2.wireOp",EDGE,"E13"),sQuery(id+"F2.wireOp",EDGE,"E14"),sQuery(id+"F2.wireOp",EDGE,"E15"),sQuery(id+"F2.wireOp",EDGE,"E16"),sQuery(id+"F2.wireOp",EDGE,"E17"),sQuery(id+"F2.wireOp",EDGE,"E18"),sQuery(id+"F2.wireOp",EDGE,"E19"),sQuery(id+"F2.wireOp",EDGE,"E20"),sQuery(id+"F2.wireOp",EDGE,"E21"),sQuery(id+"F2.wireOp",EDGE,"E22"),sQuery(id+"F2.wireOp",EDGE,"E23"),sQuery(id+"F2.wireOp",EDGE,"E24.filletArc"),sQuery(id+"F2.wireOp",EDGE,"E25"),sQuery(id+"F2.wireOp",EDGE,"E26"),sQuery(id+"F2.wireOp",EDGE,"E27.filletArc"),sQuery(id+"F2.wireOp",EDGE,"E28"),sQuery(id+"F2.wireOp",EDGE,"E29"),sQuery(id+"F2.wireOp",EDGE,"E30"),sQuery(id+"F2.wireOp",EDGE,"E31"),sQuery(id+"F2.wireOp",EDGE,"E32"),sQuery(id+"F2.wireOp",EDGE,"E33"),sQuery(id+"F2.wireOp",EDGE,"E34"),sQuery(id+"F2.wireOp",EDGE,"E35"),sQuery(id+"F2.wireOp",EDGE,"E36"),sQuery(id+"F2.wireOp",EDGE,"E37"),sQuery(id+"F2.wireOp",EDGE,"E38"),sQuery(id+"F2.wireOp",EDGE,"E39.filletArc"),sQuery(id+"F2.wireOp",EDGE,"E40.filletArc"),sQuery(id+"F2.wireOp",EDGE,"E41.filletArc"),sQuery(id+"F2.wireOp",EDGE,"E42.filletArc")])],"isStart":false})],"blendedInto":[makeQuery(id+"F3.opExtrude","CAP_FACE",FACE,{"disambiguationData":[OSD([sQuery(id+"F2.wireOp",EDGE,"E11"),sQuery(id+"F2.wireOp",EDGE,"E12"),sQuery(id+"F2.wireOp",EDGE,"E13"),sQuery(id+"F2.wireOp",EDGE,"E14"),sQuery(id+"F2.wireOp",EDGE,"E15"),sQuery(id+"F2.wireOp",EDGE,"E16"),sQuery(id+"F2.wireOp",EDGE,"E17"),sQuery(id+"F2.wireOp",EDGE,"E18"),sQuery(id+"F2.wireOp",EDGE,"E19"),sQuery(id+"F2.wireOp",EDGE,"E20"),sQuery(id+"F2.wireOp",EDGE,"E21"),sQuery(id+"F2.wireOp",EDGE,"E22"),sQuery(id+"F2.wireOp",EDGE,"E23"),sQuery(id+"F2.wireOp",EDGE,"E24.filletArc"),sQuery(id+"F2.wireOp",EDGE,"E25"),sQuery(id+"F2.wireOp",EDGE,"E26"),sQuery(id+"F2.wireOp",EDGE,"E27.filletArc"),sQuery(id+"F2.wireOp",EDGE,"E28"),sQuery(id+"F2.wireOp",EDGE,"E29"),sQuery(id+"F2.wireOp",EDGE,"E30"),sQuery(id+"F2.wireOp",EDGE,"E31"),sQuery(id+"F2.wireOp",EDGE,"E32"),sQuery(id+"F2.wireOp",EDGE,"E33"),sQuery(id+"F2.wireOp",EDGE,"E34"),sQuery(id+"F2.wireOp",EDGE,"E35"),sQuery(id+"F2.wireOp",EDGE,"E36"),sQuery(id+"F2.wireOp",EDGE,"E37"),sQuery(id+"F2.wireOp",EDGE,"E38"),sQuery(id+"F2.wireOp",EDGE,"E39.filletArc"),sQuery(id+"F2.wireOp",EDGE,"E40.filletArc"),sQuery(id+"F2.wireOp",EDGE,"E41.filletArc"),sQuery(id+"F2.wireOp",EDGE,"E42.filletArc")])],"isStart":false})]});
            var Q6;
            Q6=makeQuery(id+"F13.opFillet","BLEND_EDGE",EDGE,{"disambiguationData":[OD(4.0)],"blendedFrom":[makeQuery(id+"F1.opRevolve","SWEPT_EDGE",EDGE,{"disambiguationData":[OSD([sQuery(id+"F0.wireOp",EDGE,"E3"),sQuery(id+"F0.wireOp",EDGE,"E5")])]}),makeQuery(id+"F7.opBoolean","MERGE",FACE,{"derivedFrom":[makeQuery(id+"F3.opExtrude","CAP_FACE",FACE,{"disambiguationData":[OSD([sQuery(id+"F2.wireOp",EDGE,"E10.0"),sQuery(id+"F2.wireOp",EDGE,"E10.1"),sQuery(id+"F2.wireOp",EDGE,"E10.2"),sQuery(id+"F2.wireOp",EDGE,"E10.3"),sQuery(id+"F2.wireOp",EDGE,"E10.4"),sQuery(id+"F2.wireOp",EDGE,"E10.5")])],"isStart":true}),makeQuery(id+"F3.opExtrude","CAP_FACE",FACE,{"disambiguationData":[OSD([sQuery(id+"F2.wireOp",EDGE,"E11"),sQuery(id+"F2.wireOp",EDGE,"E12"),sQuery(id+"F2.wireOp",EDGE,"E13"),sQuery(id+"F2.wireOp",EDGE,"E14"),sQuery(id+"F2.wireOp",EDGE,"E15"),sQuery(id+"F2.wireOp",EDGE,"E16"),sQuery(id+"F2.wireOp",EDGE,"E17"),sQuery(id+"F2.wireOp",EDGE,"E18"),sQuery(id+"F2.wireOp",EDGE,"E19"),sQuery(id+"F2.wireOp",EDGE,"E20"),sQuery(id+"F2.wireOp",EDGE,"E21"),sQuery(id+"F2.wireOp",EDGE,"E22"),sQuery(id+"F2.wireOp",EDGE,"E23"),sQuery(id+"F2.wireOp",EDGE,"E24.filletArc"),sQuery(id+"F2.wireOp",EDGE,"E25"),sQuery(id+"F2.wireOp",EDGE,"E26"),sQuery(id+"F2.wireOp",EDGE,"E27.filletArc"),sQuery(id+"F2.wireOp",EDGE,"E28"),sQuery(id+"F2.wireOp",EDGE,"E29"),sQuery(id+"F2.wireOp",EDGE,"E30"),sQuery(id+"F2.wireOp",EDGE,"E31"),sQuery(id+"F2.wireOp",EDGE,"E32"),sQuery(id+"F2.wireOp",EDGE,"E33"),sQuery(id+"F2.wireOp",EDGE,"E34"),sQuery(id+"F2.wireOp",EDGE,"E35"),sQuery(id+"F2.wireOp",EDGE,"E36"),sQuery(id+"F2.wireOp",EDGE,"E37"),sQuery(id+"F2.wireOp",EDGE,"E38"),sQuery(id+"F2.wireOp",EDGE,"E39.filletArc"),sQuery(id+"F2.wireOp",EDGE,"E40.filletArc"),sQuery(id+"F2.wireOp",EDGE,"E41.filletArc"),sQuery(id+"F2.wireOp",EDGE,"E42.filletArc")])],"isStart":true}),makeQuery(id+"F6.opExtrude","CAP_FACE",FACE,{"disambiguationData":[OSD([sQuery(id+"F4.wireOp",EDGE,"E43"),sQuery(id+"F4.wireOp",EDGE,"E44.0"),sQuery(id+"F4.wireOp",EDGE,"E44.1"),sQuery(id+"F4.wireOp",EDGE,"E44.2"),sQuery(id+"F4.wireOp",EDGE,"E44.3"),sQuery(id+"F4.wireOp",EDGE,"E44.4"),sQuery(id+"F4.wireOp",EDGE,"E44.5")])],"isStart":false})]})],"blendedInto":[makeQuery(id+"F7.opBoolean","MERGE",FACE,{"derivedFrom":[makeQuery(id+"F3.opExtrude","CAP_FACE",FACE,{"disambiguationData":[OSD([sQuery(id+"F2.wireOp",EDGE,"E10.0"),sQuery(id+"F2.wireOp",EDGE,"E10.1"),sQuery(id+"F2.wireOp",EDGE,"E10.2"),sQuery(id+"F2.wireOp",EDGE,"E10.3"),sQuery(id+"F2.wireOp",EDGE,"E10.4"),sQuery(id+"F2.wireOp",EDGE,"E10.5")])],"isStart":true}),makeQuery(id+"F3.opExtrude","CAP_FACE",FACE,{"disambiguationData":[OSD([sQuery(id+"F2.wireOp",EDGE,"E11"),sQuery(id+"F2.wireOp",EDGE,"E12"),sQuery(id+"F2.wireOp",EDGE,"E13"),sQuery(id+"F2.wireOp",EDGE,"E14"),sQuery(id+"F2.wireOp",EDGE,"E15"),sQuery(id+"F2.wireOp",EDGE,"E16"),sQuery(id+"F2.wireOp",EDGE,"E17"),sQuery(id+"F2.wireOp",EDGE,"E18"),sQuery(id+"F2.wireOp",EDGE,"E19"),sQuery(id+"F2.wireOp",EDGE,"E20"),sQuery(id+"F2.wireOp",EDGE,"E21"),sQuery(id+"F2.wireOp",EDGE,"E22"),sQuery(id+"F2.wireOp",EDGE,"E23"),sQuery(id+"F2.wireOp",EDGE,"E24.filletArc"),sQuery(id+"F2.wireOp",EDGE,"E25"),sQuery(id+"F2.wireOp",EDGE,"E26"),sQuery(id+"F2.wireOp",EDGE,"E27.filletArc"),sQuery(id+"F2.wireOp",EDGE,"E28"),sQuery(id+"F2.wireOp",EDGE,"E29"),sQuery(id+"F2.wireOp",EDGE,"E30"),sQuery(id+"F2.wireOp",EDGE,"E31"),sQuery(id+"F2.wireOp",EDGE,"E32"),sQuery(id+"F2.wireOp",EDGE,"E33"),sQuery(id+"F2.wireOp",EDGE,"E34"),sQuery(id+"F2.wireOp",EDGE,"E35"),sQuery(id+"F2.wireOp",EDGE,"E36"),sQuery(id+"F2.wireOp",EDGE,"E37"),sQuery(id+"F2.wireOp",EDGE,"E38"),sQuery(id+"F2.wireOp",EDGE,"E39.filletArc"),sQuery(id+"F2.wireOp",EDGE,"E40.filletArc"),sQuery(id+"F2.wireOp",EDGE,"E41.filletArc"),sQuery(id+"F2.wireOp",EDGE,"E42.filletArc")])],"isStart":true}),makeQuery(id+"F6.opExtrude","CAP_FACE",FACE,{"disambiguationData":[OSD([sQuery(id+"F4.wireOp",EDGE,"E43"),sQuery(id+"F4.wireOp",EDGE,"E44.0"),sQuery(id+"F4.wireOp",EDGE,"E44.1"),sQuery(id+"F4.wireOp",EDGE,"E44.2"),sQuery(id+"F4.wireOp",EDGE,"E44.3"),sQuery(id+"F4.wireOp",EDGE,"E44.4"),sQuery(id+"F4.wireOp",EDGE,"E44.5")])],"isStart":false})]})]});
            var Q7;
            Q7=makeQuery(id+"F13.opFillet","BLEND_EDGE",EDGE,{"disambiguationData":[OD(4.0)],"blendedFrom":[makeQuery(id+"F1.opRevolve","SWEPT_EDGE",EDGE,{"disambiguationData":[OSD([sQuery(id+"F0.wireOp",EDGE,"E4"),sQuery(id+"F0.wireOp",EDGE,"E6")])]}),makeQuery(id+"F3.opExtrude","CAP_FACE",FACE,{"disambiguationData":[OSD([sQuery(id+"F2.wireOp",EDGE,"E11"),sQuery(id+"F2.wireOp",EDGE,"E12"),sQuery(id+"F2.wireOp",EDGE,"E13"),sQuery(id+"F2.wireOp",EDGE,"E14"),sQuery(id+"F2.wireOp",EDGE,"E15"),sQuery(id+"F2.wireOp",EDGE,"E16"),sQuery(id+"F2.wireOp",EDGE,"E17"),sQuery(id+"F2.wireOp",EDGE,"E18"),sQuery(id+"F2.wireOp",EDGE,"E19"),sQuery(id+"F2.wireOp",EDGE,"E20"),sQuery(id+"F2.wireOp",EDGE,"E21"),sQuery(id+"F2.wireOp",EDGE,"E22"),sQuery(id+"F2.wireOp",EDGE,"E23"),sQuery(id+"F2.wireOp",EDGE,"E24.filletArc"),sQuery(id+"F2.wireOp",EDGE,"E25"),sQuery(id+"F2.wireOp",EDGE,"E26"),sQuery(id+"F2.wireOp",EDGE,"E27.filletArc"),sQuery(id+"F2.wireOp",EDGE,"E28"),sQuery(id+"F2.wireOp",EDGE,"E29"),sQuery(id+"F2.wireOp",EDGE,"E30"),sQuery(id+"F2.wireOp",EDGE,"E31"),sQuery(id+"F2.wireOp",EDGE,"E32"),sQuery(id+"F2.wireOp",EDGE,"E33"),sQuery(id+"F2.wireOp",EDGE,"E34"),sQuery(id+"F2.wireOp",EDGE,"E35"),sQuery(id+"F2.wireOp",EDGE,"E36"),sQuery(id+"F2.wireOp",EDGE,"E37"),sQuery(id+"F2.wireOp",EDGE,"E38"),sQuery(id+"F2.wireOp",EDGE,"E39.filletArc"),sQuery(id+"F2.wireOp",EDGE,"E40.filletArc"),sQuery(id+"F2.wireOp",EDGE,"E41.filletArc"),sQuery(id+"F2.wireOp",EDGE,"E42.filletArc")])],"isStart":false})],"blendedInto":[makeQuery(id+"F3.opExtrude","CAP_FACE",FACE,{"disambiguationData":[OSD([sQuery(id+"F2.wireOp",EDGE,"E11"),sQuery(id+"F2.wireOp",EDGE,"E12"),sQuery(id+"F2.wireOp",EDGE,"E13"),sQuery(id+"F2.wireOp",EDGE,"E14"),sQuery(id+"F2.wireOp",EDGE,"E15"),sQuery(id+"F2.wireOp",EDGE,"E16"),sQuery(id+"F2.wireOp",EDGE,"E17"),sQuery(id+"F2.wireOp",EDGE,"E18"),sQuery(id+"F2.wireOp",EDGE,"E19"),sQuery(id+"F2.wireOp",EDGE,"E20"),sQuery(id+"F2.wireOp",EDGE,"E21"),sQuery(id+"F2.wireOp",EDGE,"E22"),sQuery(id+"F2.wireOp",EDGE,"E23"),sQuery(id+"F2.wireOp",EDGE,"E24.filletArc"),sQuery(id+"F2.wireOp",EDGE,"E25"),sQuery(id+"F2.wireOp",EDGE,"E26"),sQuery(id+"F2.wireOp",EDGE,"E27.filletArc"),sQuery(id+"F2.wireOp",EDGE,"E28"),sQuery(id+"F2.wireOp",EDGE,"E29"),sQuery(id+"F2.wireOp",EDGE,"E30"),sQuery(id+"F2.wireOp",EDGE,"E31"),sQuery(id+"F2.wireOp",EDGE,"E32"),sQuery(id+"F2.wireOp",EDGE,"E33"),sQuery(id+"F2.wireOp",EDGE,"E34"),sQuery(id+"F2.wireOp",EDGE,"E35"),sQuery(id+"F2.wireOp",EDGE,"E36"),sQuery(id+"F2.wireOp",EDGE,"E37"),sQuery(id+"F2.wireOp",EDGE,"E38"),sQuery(id+"F2.wireOp",EDGE,"E39.filletArc"),sQuery(id+"F2.wireOp",EDGE,"E40.filletArc"),sQuery(id+"F2.wireOp",EDGE,"E41.filletArc"),sQuery(id+"F2.wireOp",EDGE,"E42.filletArc")])],"isStart":false})]});
            var Q8;
            Q8=makeQuery(id+"F13.opFillet","BLEND_EDGE",EDGE,{"disambiguationData":[OD(5.0)],"blendedFrom":[makeQuery(id+"F1.opRevolve","SWEPT_EDGE",EDGE,{"disambiguationData":[OSD([sQuery(id+"F0.wireOp",EDGE,"E4"),sQuery(id+"F0.wireOp",EDGE,"E6")])]}),makeQuery(id+"F3.opExtrude","CAP_FACE",FACE,{"disambiguationData":[OSD([sQuery(id+"F2.wireOp",EDGE,"E11"),sQuery(id+"F2.wireOp",EDGE,"E12"),sQuery(id+"F2.wireOp",EDGE,"E13"),sQuery(id+"F2.wireOp",EDGE,"E14"),sQuery(id+"F2.wireOp",EDGE,"E15"),sQuery(id+"F2.wireOp",EDGE,"E16"),sQuery(id+"F2.wireOp",EDGE,"E17"),sQuery(id+"F2.wireOp",EDGE,"E18"),sQuery(id+"F2.wireOp",EDGE,"E19"),sQuery(id+"F2.wireOp",EDGE,"E20"),sQuery(id+"F2.wireOp",EDGE,"E21"),sQuery(id+"F2.wireOp",EDGE,"E22"),sQuery(id+"F2.wireOp",EDGE,"E23"),sQuery(id+"F2.wireOp",EDGE,"E24.filletArc"),sQuery(id+"F2.wireOp",EDGE,"E25"),sQuery(id+"F2.wireOp",EDGE,"E26"),sQuery(id+"F2.wireOp",EDGE,"E27.filletArc"),sQuery(id+"F2.wireOp",EDGE,"E28"),sQuery(id+"F2.wireOp",EDGE,"E29"),sQuery(id+"F2.wireOp",EDGE,"E30"),sQuery(id+"F2.wireOp",EDGE,"E31"),sQuery(id+"F2.wireOp",EDGE,"E32"),sQuery(id+"F2.wireOp",EDGE,"E33"),sQuery(id+"F2.wireOp",EDGE,"E34"),sQuery(id+"F2.wireOp",EDGE,"E35"),sQuery(id+"F2.wireOp",EDGE,"E36"),sQuery(id+"F2.wireOp",EDGE,"E37"),sQuery(id+"F2.wireOp",EDGE,"E38"),sQuery(id+"F2.wireOp",EDGE,"E39.filletArc"),sQuery(id+"F2.wireOp",EDGE,"E40.filletArc"),sQuery(id+"F2.wireOp",EDGE,"E41.filletArc"),sQuery(id+"F2.wireOp",EDGE,"E42.filletArc")])],"isStart":false})],"blendedInto":[makeQuery(id+"F3.opExtrude","CAP_FACE",FACE,{"disambiguationData":[OSD([sQuery(id+"F2.wireOp",EDGE,"E11"),sQuery(id+"F2.wireOp",EDGE,"E12"),sQuery(id+"F2.wireOp",EDGE,"E13"),sQuery(id+"F2.wireOp",EDGE,"E14"),sQuery(id+"F2.wireOp",EDGE,"E15"),sQuery(id+"F2.wireOp",EDGE,"E16"),sQuery(id+"F2.wireOp",EDGE,"E17"),sQuery(id+"F2.wireOp",EDGE,"E18"),sQuery(id+"F2.wireOp",EDGE,"E19"),sQuery(id+"F2.wireOp",EDGE,"E20"),sQuery(id+"F2.wireOp",EDGE,"E21"),sQuery(id+"F2.wireOp",EDGE,"E22"),sQuery(id+"F2.wireOp",EDGE,"E23"),sQuery(id+"F2.wireOp",EDGE,"E24.filletArc"),sQuery(id+"F2.wireOp",EDGE,"E25"),sQuery(id+"F2.wireOp",EDGE,"E26"),sQuery(id+"F2.wireOp",EDGE,"E27.filletArc"),sQuery(id+"F2.wireOp",EDGE,"E28"),sQuery(id+"F2.wireOp",EDGE,"E29"),sQuery(id+"F2.wireOp",EDGE,"E30"),sQuery(id+"F2.wireOp",EDGE,"E31"),sQuery(id+"F2.wireOp",EDGE,"E32"),sQuery(id+"F2.wireOp",EDGE,"E33"),sQuery(id+"F2.wireOp",EDGE,"E34"),sQuery(id+"F2.wireOp",EDGE,"E35"),sQuery(id+"F2.wireOp",EDGE,"E36"),sQuery(id+"F2.wireOp",EDGE,"E37"),sQuery(id+"F2.wireOp",EDGE,"E38"),sQuery(id+"F2.wireOp",EDGE,"E39.filletArc"),sQuery(id+"F2.wireOp",EDGE,"E40.filletArc"),sQuery(id+"F2.wireOp",EDGE,"E41.filletArc"),sQuery(id+"F2.wireOp",EDGE,"E42.filletArc")])],"isStart":false})]});
            var Q9;
            Q9=makeQuery(id+"F13.opFillet","BLEND_EDGE",EDGE,{"disambiguationData":[OD(3.0)],"blendedFrom":[makeQuery(id+"F1.opRevolve","SWEPT_EDGE",EDGE,{"disambiguationData":[OSD([sQuery(id+"F0.wireOp",EDGE,"E4"),sQuery(id+"F0.wireOp",EDGE,"E6")])]}),makeQuery(id+"F3.opExtrude","CAP_FACE",FACE,{"disambiguationData":[OSD([sQuery(id+"F2.wireOp",EDGE,"E11"),sQuery(id+"F2.wireOp",EDGE,"E12"),sQuery(id+"F2.wireOp",EDGE,"E13"),sQuery(id+"F2.wireOp",EDGE,"E14"),sQuery(id+"F2.wireOp",EDGE,"E15"),sQuery(id+"F2.wireOp",EDGE,"E16"),sQuery(id+"F2.wireOp",EDGE,"E17"),sQuery(id+"F2.wireOp",EDGE,"E18"),sQuery(id+"F2.wireOp",EDGE,"E19"),sQuery(id+"F2.wireOp",EDGE,"E20"),sQuery(id+"F2.wireOp",EDGE,"E21"),sQuery(id+"F2.wireOp",EDGE,"E22"),sQuery(id+"F2.wireOp",EDGE,"E23"),sQuery(id+"F2.wireOp",EDGE,"E24.filletArc"),sQuery(id+"F2.wireOp",EDGE,"E25"),sQuery(id+"F2.wireOp",EDGE,"E26"),sQuery(id+"F2.wireOp",EDGE,"E27.filletArc"),sQuery(id+"F2.wireOp",EDGE,"E28"),sQuery(id+"F2.wireOp",EDGE,"E29"),sQuery(id+"F2.wireOp",EDGE,"E30"),sQuery(id+"F2.wireOp",EDGE,"E31"),sQuery(id+"F2.wireOp",EDGE,"E32"),sQuery(id+"F2.wireOp",EDGE,"E33"),sQuery(id+"F2.wireOp",EDGE,"E34"),sQuery(id+"F2.wireOp",EDGE,"E35"),sQuery(id+"F2.wireOp",EDGE,"E36"),sQuery(id+"F2.wireOp",EDGE,"E37"),sQuery(id+"F2.wireOp",EDGE,"E38"),sQuery(id+"F2.wireOp",EDGE,"E39.filletArc"),sQuery(id+"F2.wireOp",EDGE,"E40.filletArc"),sQuery(id+"F2.wireOp",EDGE,"E41.filletArc"),sQuery(id+"F2.wireOp",EDGE,"E42.filletArc")])],"isStart":false})],"blendedInto":[makeQuery(id+"F3.opExtrude","CAP_FACE",FACE,{"disambiguationData":[OSD([sQuery(id+"F2.wireOp",EDGE,"E11"),sQuery(id+"F2.wireOp",EDGE,"E12"),sQuery(id+"F2.wireOp",EDGE,"E13"),sQuery(id+"F2.wireOp",EDGE,"E14"),sQuery(id+"F2.wireOp",EDGE,"E15"),sQuery(id+"F2.wireOp",EDGE,"E16"),sQuery(id+"F2.wireOp",EDGE,"E17"),sQuery(id+"F2.wireOp",EDGE,"E18"),sQuery(id+"F2.wireOp",EDGE,"E19"),sQuery(id+"F2.wireOp",EDGE,"E20"),sQuery(id+"F2.wireOp",EDGE,"E21"),sQuery(id+"F2.wireOp",EDGE,"E22"),sQuery(id+"F2.wireOp",EDGE,"E23"),sQuery(id+"F2.wireOp",EDGE,"E24.filletArc"),sQuery(id+"F2.wireOp",EDGE,"E25"),sQuery(id+"F2.wireOp",EDGE,"E26"),sQuery(id+"F2.wireOp",EDGE,"E27.filletArc"),sQuery(id+"F2.wireOp",EDGE,"E28"),sQuery(id+"F2.wireOp",EDGE,"E29"),sQuery(id+"F2.wireOp",EDGE,"E30"),sQuery(id+"F2.wireOp",EDGE,"E31"),sQuery(id+"F2.wireOp",EDGE,"E32"),sQuery(id+"F2.wireOp",EDGE,"E33"),sQuery(id+"F2.wireOp",EDGE,"E34"),sQuery(id+"F2.wireOp",EDGE,"E35"),sQuery(id+"F2.wireOp",EDGE,"E36"),sQuery(id+"F2.wireOp",EDGE,"E37"),sQuery(id+"F2.wireOp",EDGE,"E38"),sQuery(id+"F2.wireOp",EDGE,"E39.filletArc"),sQuery(id+"F2.wireOp",EDGE,"E40.filletArc"),sQuery(id+"F2.wireOp",EDGE,"E41.filletArc"),sQuery(id+"F2.wireOp",EDGE,"E42.filletArc")])],"isStart":false})]});
            var Q10;
            Q10=makeQuery(id+"F13.opFillet","BLEND_EDGE",EDGE,{"disambiguationData":[OD(2.0)],"blendedFrom":[makeQuery(id+"F1.opRevolve","SWEPT_EDGE",EDGE,{"disambiguationData":[OSD([sQuery(id+"F0.wireOp",EDGE,"E4"),sQuery(id+"F0.wireOp",EDGE,"E6")])]}),makeQuery(id+"F3.opExtrude","CAP_FACE",FACE,{"disambiguationData":[OSD([sQuery(id+"F2.wireOp",EDGE,"E11"),sQuery(id+"F2.wireOp",EDGE,"E12"),sQuery(id+"F2.wireOp",EDGE,"E13"),sQuery(id+"F2.wireOp",EDGE,"E14"),sQuery(id+"F2.wireOp",EDGE,"E15"),sQuery(id+"F2.wireOp",EDGE,"E16"),sQuery(id+"F2.wireOp",EDGE,"E17"),sQuery(id+"F2.wireOp",EDGE,"E18"),sQuery(id+"F2.wireOp",EDGE,"E19"),sQuery(id+"F2.wireOp",EDGE,"E20"),sQuery(id+"F2.wireOp",EDGE,"E21"),sQuery(id+"F2.wireOp",EDGE,"E22"),sQuery(id+"F2.wireOp",EDGE,"E23"),sQuery(id+"F2.wireOp",EDGE,"E24.filletArc"),sQuery(id+"F2.wireOp",EDGE,"E25"),sQuery(id+"F2.wireOp",EDGE,"E26"),sQuery(id+"F2.wireOp",EDGE,"E27.filletArc"),sQuery(id+"F2.wireOp",EDGE,"E28"),sQuery(id+"F2.wireOp",EDGE,"E29"),sQuery(id+"F2.wireOp",EDGE,"E30"),sQuery(id+"F2.wireOp",EDGE,"E31"),sQuery(id+"F2.wireOp",EDGE,"E32"),sQuery(id+"F2.wireOp",EDGE,"E33"),sQuery(id+"F2.wireOp",EDGE,"E34"),sQuery(id+"F2.wireOp",EDGE,"E35"),sQuery(id+"F2.wireOp",EDGE,"E36"),sQuery(id+"F2.wireOp",EDGE,"E37"),sQuery(id+"F2.wireOp",EDGE,"E38"),sQuery(id+"F2.wireOp",EDGE,"E39.filletArc"),sQuery(id+"F2.wireOp",EDGE,"E40.filletArc"),sQuery(id+"F2.wireOp",EDGE,"E41.filletArc"),sQuery(id+"F2.wireOp",EDGE,"E42.filletArc")])],"isStart":false})],"blendedInto":[makeQuery(id+"F3.opExtrude","CAP_FACE",FACE,{"disambiguationData":[OSD([sQuery(id+"F2.wireOp",EDGE,"E11"),sQuery(id+"F2.wireOp",EDGE,"E12"),sQuery(id+"F2.wireOp",EDGE,"E13"),sQuery(id+"F2.wireOp",EDGE,"E14"),sQuery(id+"F2.wireOp",EDGE,"E15"),sQuery(id+"F2.wireOp",EDGE,"E16"),sQuery(id+"F2.wireOp",EDGE,"E17"),sQuery(id+"F2.wireOp",EDGE,"E18"),sQuery(id+"F2.wireOp",EDGE,"E19"),sQuery(id+"F2.wireOp",EDGE,"E20"),sQuery(id+"F2.wireOp",EDGE,"E21"),sQuery(id+"F2.wireOp",EDGE,"E22"),sQuery(id+"F2.wireOp",EDGE,"E23"),sQuery(id+"F2.wireOp",EDGE,"E24.filletArc"),sQuery(id+"F2.wireOp",EDGE,"E25"),sQuery(id+"F2.wireOp",EDGE,"E26"),sQuery(id+"F2.wireOp",EDGE,"E27.filletArc"),sQuery(id+"F2.wireOp",EDGE,"E28"),sQuery(id+"F2.wireOp",EDGE,"E29"),sQuery(id+"F2.wireOp",EDGE,"E30"),sQuery(id+"F2.wireOp",EDGE,"E31"),sQuery(id+"F2.wireOp",EDGE,"E32"),sQuery(id+"F2.wireOp",EDGE,"E33"),sQuery(id+"F2.wireOp",EDGE,"E34"),sQuery(id+"F2.wireOp",EDGE,"E35"),sQuery(id+"F2.wireOp",EDGE,"E36"),sQuery(id+"F2.wireOp",EDGE,"E37"),sQuery(id+"F2.wireOp",EDGE,"E38"),sQuery(id+"F2.wireOp",EDGE,"E39.filletArc"),sQuery(id+"F2.wireOp",EDGE,"E40.filletArc"),sQuery(id+"F2.wireOp",EDGE,"E41.filletArc"),sQuery(id+"F2.wireOp",EDGE,"E42.filletArc")])],"isStart":false})]});
            var Q11;
            Q11=makeQuery(id+"F13.opFillet","BLEND_EDGE",EDGE,{"disambiguationData":[OD(0.0)],"blendedFrom":[makeQuery(id+"F1.opRevolve","SWEPT_EDGE",EDGE,{"disambiguationData":[OSD([sQuery(id+"F0.wireOp",EDGE,"E4"),sQuery(id+"F0.wireOp",EDGE,"E6")])]}),makeQuery(id+"F3.opExtrude","CAP_FACE",FACE,{"disambiguationData":[OSD([sQuery(id+"F2.wireOp",EDGE,"E11"),sQuery(id+"F2.wireOp",EDGE,"E12"),sQuery(id+"F2.wireOp",EDGE,"E13"),sQuery(id+"F2.wireOp",EDGE,"E14"),sQuery(id+"F2.wireOp",EDGE,"E15"),sQuery(id+"F2.wireOp",EDGE,"E16"),sQuery(id+"F2.wireOp",EDGE,"E17"),sQuery(id+"F2.wireOp",EDGE,"E18"),sQuery(id+"F2.wireOp",EDGE,"E19"),sQuery(id+"F2.wireOp",EDGE,"E20"),sQuery(id+"F2.wireOp",EDGE,"E21"),sQuery(id+"F2.wireOp",EDGE,"E22"),sQuery(id+"F2.wireOp",EDGE,"E23"),sQuery(id+"F2.wireOp",EDGE,"E24.filletArc"),sQuery(id+"F2.wireOp",EDGE,"E25"),sQuery(id+"F2.wireOp",EDGE,"E26"),sQuery(id+"F2.wireOp",EDGE,"E27.filletArc"),sQuery(id+"F2.wireOp",EDGE,"E28"),sQuery(id+"F2.wireOp",EDGE,"E29"),sQuery(id+"F2.wireOp",EDGE,"E30"),sQuery(id+"F2.wireOp",EDGE,"E31"),sQuery(id+"F2.wireOp",EDGE,"E32"),sQuery(id+"F2.wireOp",EDGE,"E33"),sQuery(id+"F2.wireOp",EDGE,"E34"),sQuery(id+"F2.wireOp",EDGE,"E35"),sQuery(id+"F2.wireOp",EDGE,"E36"),sQuery(id+"F2.wireOp",EDGE,"E37"),sQuery(id+"F2.wireOp",EDGE,"E38"),sQuery(id+"F2.wireOp",EDGE,"E39.filletArc"),sQuery(id+"F2.wireOp",EDGE,"E40.filletArc"),sQuery(id+"F2.wireOp",EDGE,"E41.filletArc"),sQuery(id+"F2.wireOp",EDGE,"E42.filletArc")])],"isStart":false})],"blendedInto":[makeQuery(id+"F3.opExtrude","CAP_FACE",FACE,{"disambiguationData":[OSD([sQuery(id+"F2.wireOp",EDGE,"E11"),sQuery(id+"F2.wireOp",EDGE,"E12"),sQuery(id+"F2.wireOp",EDGE,"E13"),sQuery(id+"F2.wireOp",EDGE,"E14"),sQuery(id+"F2.wireOp",EDGE,"E15"),sQuery(id+"F2.wireOp",EDGE,"E16"),sQuery(id+"F2.wireOp",EDGE,"E17"),sQuery(id+"F2.wireOp",EDGE,"E18"),sQuery(id+"F2.wireOp",EDGE,"E19"),sQuery(id+"F2.wireOp",EDGE,"E20"),sQuery(id+"F2.wireOp",EDGE,"E21"),sQuery(id+"F2.wireOp",EDGE,"E22"),sQuery(id+"F2.wireOp",EDGE,"E23"),sQuery(id+"F2.wireOp",EDGE,"E24.filletArc"),sQuery(id+"F2.wireOp",EDGE,"E25"),sQuery(id+"F2.wireOp",EDGE,"E26"),sQuery(id+"F2.wireOp",EDGE,"E27.filletArc"),sQuery(id+"F2.wireOp",EDGE,"E28"),sQuery(id+"F2.wireOp",EDGE,"E29"),sQuery(id+"F2.wireOp",EDGE,"E30"),sQuery(id+"F2.wireOp",EDGE,"E31"),sQuery(id+"F2.wireOp",EDGE,"E32"),sQuery(id+"F2.wireOp",EDGE,"E33"),sQuery(id+"F2.wireOp",EDGE,"E34"),sQuery(id+"F2.wireOp",EDGE,"E35"),sQuery(id+"F2.wireOp",EDGE,"E36"),sQuery(id+"F2.wireOp",EDGE,"E37"),sQuery(id+"F2.wireOp",EDGE,"E38"),sQuery(id+"F2.wireOp",EDGE,"E39.filletArc"),sQuery(id+"F2.wireOp",EDGE,"E40.filletArc"),sQuery(id+"F2.wireOp",EDGE,"E41.filletArc"),sQuery(id+"F2.wireOp",EDGE,"E42.filletArc")])],"isStart":false})]});
            chamfer(context, id + "F14", {"entities" : qUnion([Q0, Q1, Q2, Q3, Q4, Q5, Q6, Q7, Q8, Q9, Q10, Q11]), "width" : 0.76 * mm, "tangentPropagation" : true});
        }
    });
